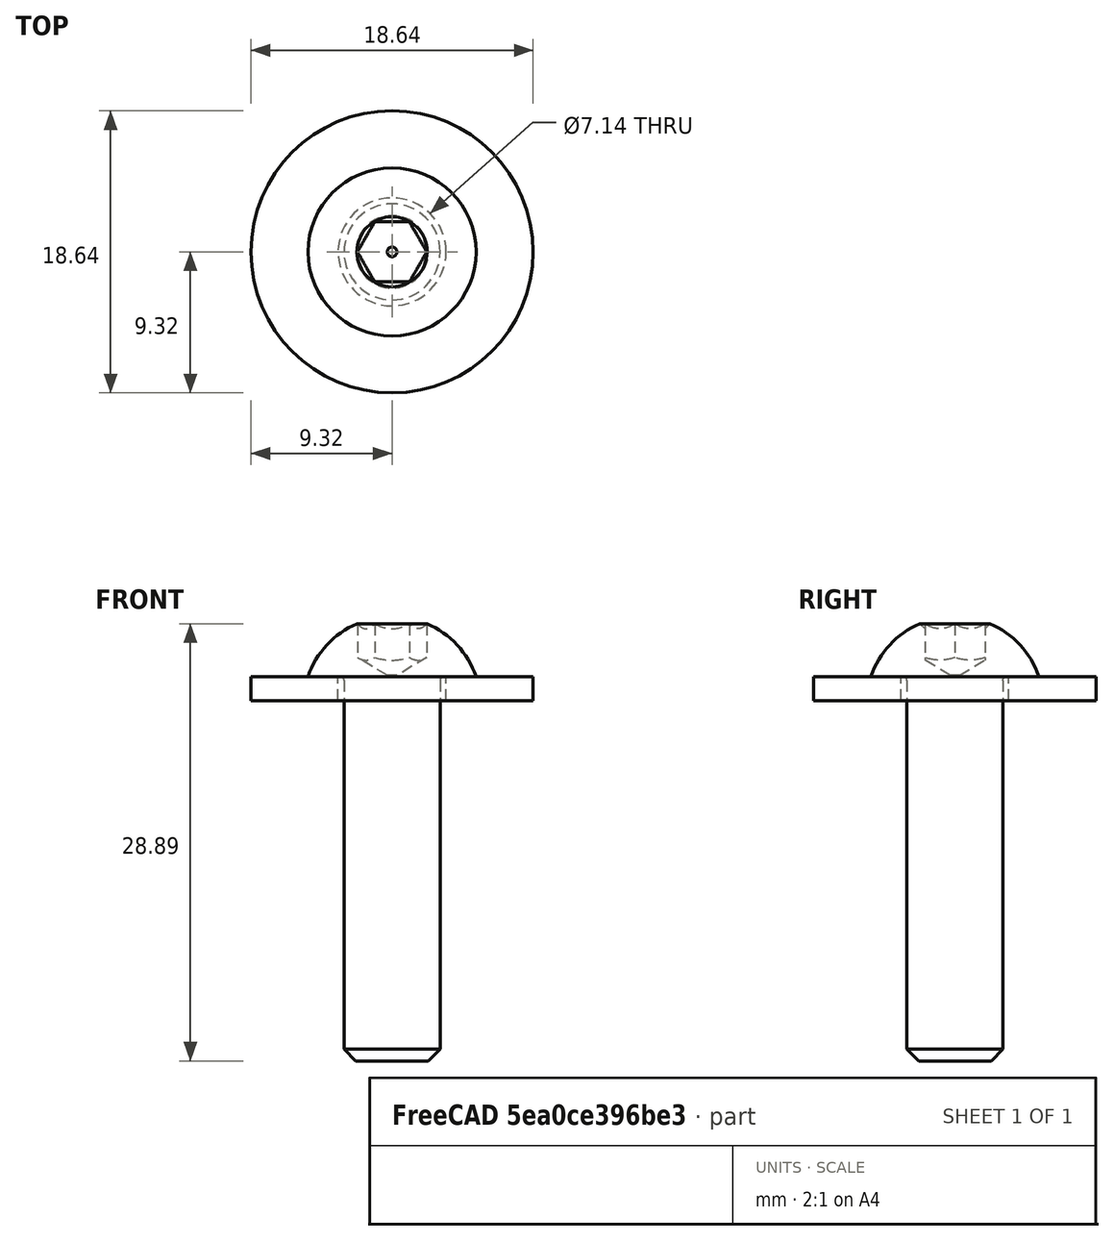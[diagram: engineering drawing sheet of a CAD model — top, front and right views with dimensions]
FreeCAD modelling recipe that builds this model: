
FCSTD DOCUMENT  (FreeCAD 2021.717R24301 +3842 (Git))
Label: Y-axis
License: Creative Commons Attribution
LicenseURL: http://creativecommons.org/licenses/by/4.0/
objects: App::FeaturePython×191, Part::FeaturePython×144, App::LinkElement×32, App::Link×30, App::DocumentObjectGroup×1
note: 139 computed .brp shape members not serialized (recipe doc carries the construction recipe); baked Part::Feature solids carry a one-line shape summary decoded from their .brp
EXTERNAL_REF file=parts/Extrusion.FCStd obj=Body003
EXTERNAL_REF file=parts/Extrusion.FCStd obj=Body005
EXTERNAL_REF file=parts/HGR20.FCStd obj=Assembly002
EXTERNAL_REF file=parts/Ballscrew.FCStd obj=Assembly004
EXTERNAL_REF file=parts/Y axis plates.FCStd obj=Assembly003
EXTERNAL_REF file=parts/Y axis plates.FCStd obj=Assembly002
EXTERNAL_REF file=parts/Y axis plates.FCStd obj=Assembly001
EXTERNAL_REF file=parts/Y axis plates.FCStd obj=Assembly
EXTERNAL_REF file=parts/NEMA23-76.FCStd obj=Assembly001
EXTERNAL_REF file=parts/NEMA23-76.FCStd obj=Assembly
EXTERNAL_REF file=parts/Y axis plates.FCStd obj=Assembly004
EXTERNAL_REF file=parts/Y axis plates.FCStd obj=Assembly005
EXTERNAL_REF file=parts/Table.FCStd obj=Assembly
EXTERNAL_REF file=parts/Y axis plates.FCStd obj=Assembly006
EXTERNAL_REF file=parts/Y axis plates.FCStd obj=Assembly007
EXTERNAL_REF file=parts/LimitSensor.FCStd obj=Assembly

FEATURE [App::Link] Link001  label="Link001(Cross member 2x2)"
  AutoLinkLabel = true
  AutoPlacement = true
  LinkPlacement = pos=(259,-5.77867e-05,-25) rot=(0,0,-1;1.5708rad)
  LinkedObject = -> <external parts/Extrusion.FCStd>#Body003
  Placement = pos=(259,-5.77867e-05,-25) rot=(0,0,-1;1.5708rad)
  SyncGroupVisibility = false
  _LinkVersion = 1
FEATURE [Part::FeaturePython] Parts002  # WARN: FeaturePython — macro-defined, semantics opaque (R4)
  Group = -> [Link001]
  GroupMode = 0
  _LinkVersion = 1
FEATURE [App::Link] Link003  label="Front"
  AutoLinkLabel = true
  AutoPlacement = true
  LinkPlacement = pos=(-9.60009,-389.6,-0.400015) rot=(0,0,1;0rad)
  LinkedObject = -> Assembly002
  Placement = pos=(-9.60009,-389.6,-0.400015) rot=(0,0,1;0rad)
  SyncGroupVisibility = false
  _LinkVersion = 1
FEATURE [App::Link] Link004  label="Cross1"
  AutoLinkLabel = true
  AutoPlacement = true
  LinkPlacement = pos=(-9.60009,-129.867,-0.400015) rot=(0,0,1;0rad)
  LinkedObject = -> Link003
  Placement = pos=(-9.60009,-129.867,-0.400015) rot=(0,0,1;0rad)
  SyncGroupVisibility = false
  _LinkVersion = 1
FEATURE [App::Link] Link005  label="Cross2"
  AutoLinkLabel = true
  AutoPlacement = true
  LinkPlacement = pos=(-9.60009,129.867,-0.400015) rot=(0,0,1;0rad)
  LinkedObject = -> Link003
  Placement = pos=(-9.60009,129.867,-0.400015) rot=(0,0,1;0rad)
  SyncGroupVisibility = false
  _LinkVersion = 1
FEATURE [App::Link] Link006  label="Back"
  AutoLinkLabel = true
  AutoPlacement = true
  LinkPlacement = pos=(-9.60009,389.6,-0.400015) rot=(0,0,1;0rad)
  LinkedObject = -> Link003
  Placement = pos=(-9.60009,389.6,-0.400015) rot=(0,0,1;0rad)
  SyncGroupVisibility = false
  _LinkVersion = 1
FEATURE [App::Link] Link  label="Link(Y-beam 2x4)"
  AutoLinkLabel = true
  AutoPlacement = true
  LinkedObject = -> <external parts/Extrusion.FCStd>#Body005
  SyncGroupVisibility = false
  _LinkVersion = 1
FEATURE [App::Link] Link008  label="Link008(Y-beam 2x4)"
  AutoLinkLabel = true
  AutoPlacement = true
  LinkPlacement = pos=(-9.58364e-05,49,0) rot=(0,0,1;3.14159rad)
  LinkedObject = -> <external parts/Extrusion.FCStd>#Body005
  Placement = pos=(-9.58364e-05,49,0) rot=(0,0,1;3.14159rad)
  SyncGroupVisibility = false
  _LinkVersion = 1
FEATURE [App::Link] Link009  label="Left beam"
  AutoLinkLabel = true
  AutoPlacement = true
  LinkedObject = -> Assembly001
  SyncGroupVisibility = false
  _LinkVersion = 1
FEATURE [App::Link] Link010  label="Right beam"
  AutoLinkLabel = true
  AutoPlacement = true
  LinkPlacement = pos=(498.8,-49,1.208e-13) rot=(0,0,1;6.28318rad)
  LinkedObject = -> Assembly003
  Placement = pos=(498.8,-49,1.208e-13) rot=(0,0,1;6.28318rad)
  SyncGroupVisibility = false
  _LinkVersion = 1
FEATURE [App::Link] Link011  label="HGR20 Left"
  AutoLinkLabel = true
  AutoPlacement = true
  LinkPlacement = pos=(-25.4,2.8e-15,38.1) rot=(-0.707107,0,0.707107;3.14159rad)
  LinkedObject = -> <external parts/HGR20.FCStd>#Assembly002
  Placement = pos=(-25.4,2.8e-15,38.1) rot=(-0.707107,0,0.707107;3.14159rad)
  SyncGroupVisibility = false
  _LinkVersion = 1
FEATURE [App::Link] Link012  label="HGR20 Right"
  AutoLinkLabel = true
  AutoPlacement = true
  LinkPlacement = pos=(524.2,-1.208e-13,38.1) rot=(0,-1,0;4.71239rad)
  LinkedObject = -> <external parts/HGR20.FCStd>#Assembly002
  Placement = pos=(524.2,-1.208e-13,38.1) rot=(0,-1,0;4.71239rad)
  SyncGroupVisibility = false
  _LinkVersion = 1
FEATURE [App::Link] Link013  label="Ballscrew Left"
  AutoLinkLabel = true
  AutoPlacement = true
  LinkPlacement = pos=(-30.1231,403.1,-15.0731) rot=(0,-1,0;1.5708rad)
  LinkedObject = -> <external parts/Ballscrew.FCStd>#Assembly004
  Placement = pos=(-30.1231,403.1,-15.0731) rot=(0,-1,0;1.5708rad)
  SyncGroupVisibility = false
  _LinkVersion = 1
FEATURE [App::Link] Link014  label="Ballscrew Right"
  AutoLinkLabel = true
  AutoPlacement = true
  LinkPlacement = pos=(528.923,403.1,-15.1269) rot=(0,1,0;1.5708rad)
  LinkedObject = -> <external parts/Ballscrew.FCStd>#Assembly004
  Placement = pos=(528.923,403.1,-15.1269) rot=(0,1,0;1.5708rad)
  SyncGroupVisibility = false
  _LinkVersion = 1
FEATURE [App::Link] Link015  label="BF12R plate"
  AutoLinkLabel = true
  AutoPlacement = true
  LinkPlacement = pos=(524.2,-445,-15.1) rot=(0,0,1;0rad)
  LinkedObject = -> <external parts/Y axis plates.FCStd>#Assembly003
  Placement = pos=(524.2,-445,-15.1) rot=(0,0,1;0rad)
  SyncGroupVisibility = false
  _LinkVersion = 1
FEATURE [App::Link] Link016  label="BF12L plate"
  AutoLinkLabel = true
  AutoPlacement = true
  LinkPlacement = pos=(-30.4,-445,-15.1) rot=(0,0,1;0rad)
  LinkedObject = -> <external parts/Y axis plates.FCStd>#Assembly002
  Placement = pos=(-30.4,-445,-15.1) rot=(0,0,1;0rad)
  SyncGroupVisibility = false
  _LinkVersion = 1
FEATURE [App::Link] Link017  label="BK12L plate"
  AutoLinkLabel = true
  AutoPlacement = true
  LinkPlacement = pos=(-30.4,347.1,-15.1) rot=(0,0,1;0rad)
  LinkedObject = -> <external parts/Y axis plates.FCStd>#Assembly001
  Placement = pos=(-30.4,347.1,-15.1) rot=(0,0,1;0rad)
  SyncGroupVisibility = false
  _LinkVersion = 1
FEATURE [App::Link] Link018  label="BK12R plate"
  AutoLinkLabel = true
  AutoPlacement = true
  LinkPlacement = pos=(524.2,347.1,-15.1) rot=(0,0,1;0rad)
  LinkedObject = -> <external parts/Y axis plates.FCStd>#Assembly
  Placement = pos=(524.2,347.1,-15.1) rot=(0,0,1;0rad)
  SyncGroupVisibility = false
  _LinkVersion = 1
FEATURE [App::Link] Link019  label="Coupling-L"
  AutoLinkLabel = true
  AutoPlacement = true
  LinkPlacement = pos=(-55.4,393.45,-15.1) rot=(0.57735,-0.57735,0.57735;2.0944rad)
  LinkedObject = -> <external parts/NEMA23-76.FCStd>#Assembly001
  Placement = pos=(-55.4,393.45,-15.1) rot=(0.57735,-0.57735,0.57735;2.0944rad)
  SyncGroupVisibility = false
  _LinkVersion = 1
FEATURE [App::Link] Link020  label="Coupling-R"
  AutoLinkLabel = true
  AutoPlacement = true
  LinkPlacement = pos=(554.2,393.45,-15.1) rot=(0.57735,0.57735,-0.57735;2.0944rad)
  LinkedObject = -> <external parts/NEMA23-76.FCStd>#Assembly001
  Placement = pos=(554.2,393.45,-15.1) rot=(0.57735,0.57735,-0.57735;2.0944rad)
  SyncGroupVisibility = false
  _LinkVersion = 1
FEATURE [App::Link] Link021  label="NEMA23-L"
  AutoLinkLabel = true
  AutoPlacement = true
  LinkPlacement = pos=(-55.4,421.35,-15.1) rot=(-0.57735,-0.57735,-0.57735;2.0944rad)
  LinkedObject = -> <external parts/NEMA23-76.FCStd>#Assembly
  Placement = pos=(-55.4,421.35,-15.1) rot=(-0.57735,-0.57735,-0.57735;2.0944rad)
  SyncGroupVisibility = false
  _LinkVersion = 1
FEATURE [App::Link] Link022  label="NEMA23-R"
  AutoLinkLabel = true
  AutoPlacement = true
  LinkPlacement = pos=(554.2,421.35,-15.1) rot=(0.57735,-0.57735,-0.57735;4.18879rad)
  LinkedObject = -> <external parts/NEMA23-76.FCStd>#Assembly
  Placement = pos=(554.2,421.35,-15.1) rot=(0.57735,-0.57735,-0.57735;4.18879rad)
  SyncGroupVisibility = false
  _LinkVersion = 1
FEATURE [App::Link] Link023  label="Motor plate R"
  AutoLinkLabel = true
  AutoPlacement = true
  LinkPlacement = pos=(530.9,415,-2.167e-13) rot=(0,0,-1;3.14159rad)
  LinkedObject = -> <external parts/Y axis plates.FCStd>#Assembly004
  Placement = pos=(530.9,415,-2.167e-13) rot=(0,0,-1;3.14159rad)
  SyncGroupVisibility = false
  _LinkVersion = 1
FEATURE [App::Link] Link024  label="Motor plate L"
  AutoLinkLabel = true
  AutoPlacement = true
  LinkPlacement = pos=(-32.1,414.35,1.5117e-12) rot=(0,0,1;3.14159rad)
  LinkedObject = -> <external parts/Y axis plates.FCStd>#Assembly005
  Placement = pos=(-32.1,414.35,1.5117e-12) rot=(0,0,1;3.14159rad)
  SyncGroupVisibility = false
  _LinkVersion = 1
FEATURE [App::Link] Link025  label="PP Table"
  AutoLinkLabel = true
  AutoPlacement = true
  LinkPlacement = pos=(249.4,-1.137e-13,-2.013e-13) rot=(0,0,1;0rad)
  LinkedObject = -> <external parts/Table.FCStd>#Assembly
  Placement = pos=(249.4,-1.137e-13,-2.013e-13) rot=(0,0,1;0rad)
  SyncGroupVisibility = false
  _LinkVersion = 1
FEATURE [Part::FeaturePython] Screw  label="1/4inx1in-Screw"  # Fasteners workbench fastener (typed FeaturePython)
  diameter = 11
  invert = false
  length = 6
  lengthCustom = 25.4
  matchOuter = false
  offset = 0
  thread = false
  type = 4
FEATURE [Part::FeaturePython] Washer  label="1/4in-Washer"  # Fasteners workbench fastener (typed FeaturePython)
  Placement = pos=(0,0,-1.6002) rot=(0,0,1;0rad)
  diameter = 11
  invert = false
  matchOuter = false
  offset = 0
  type = 1
FEATURE [Part::FeaturePython] Parts004  # WARN: FeaturePython — macro-defined, semantics opaque (R4)
  Group = -> [Washer,Screw]
  GroupMode = 0
  _LinkVersion = 1
FEATURE [App::LinkElement] Link026_i0
  LinkPlacement = pos=(21.5898,-402.3,-12.7) rot=(0,-1,0;1.5708rad)
  LinkedObject = -> Assembly004
  Placement = pos=(21.5898,-402.3,-12.7) rot=(0,-1,0;1.5708rad)
  _LinkVersion = 1
FEATURE [App::LinkElement] Link026_i1
  LinkPlacement = pos=(21.5898,-376.9,-12.7) rot=(0,-1,0;1.5708rad)
  LinkedObject = -> Assembly004
  Placement = pos=(21.5898,-376.9,-12.7) rot=(0,-1,0;1.5708rad)
  _LinkVersion = 1
FEATURE [App::LinkElement] Link026_i2
  LinkPlacement = pos=(21.5898,-402.3,-38.1) rot=(0,-1,0;1.5708rad)
  LinkedObject = -> Assembly004
  Placement = pos=(21.5898,-402.3,-38.1) rot=(0,-1,0;1.5708rad)
  _LinkVersion = 1
FEATURE [App::LinkElement] Link026_i3
  LinkPlacement = pos=(21.5898,-376.9,-38.1) rot=(0,-1,0;1.5708rad)
  LinkedObject = -> Assembly004
  Placement = pos=(21.5898,-376.9,-38.1) rot=(0,-1,0;1.5708rad)
  _LinkVersion = 1
FEATURE [App::LinkElement] Link026_i4
  LinkPlacement = pos=(21.5898,-142.567,-12.7) rot=(0,-1,0;1.5708rad)
  LinkedObject = -> Assembly004
  Placement = pos=(21.5898,-142.567,-12.7) rot=(0,-1,0;1.5708rad)
  _LinkVersion = 1
FEATURE [App::LinkElement] Link026_i5
  LinkPlacement = pos=(21.5898,-117.167,-12.7) rot=(0,-1,0;1.5708rad)
  LinkedObject = -> Assembly004
  Placement = pos=(21.5898,-117.167,-12.7) rot=(0,-1,0;1.5708rad)
  _LinkVersion = 1
FEATURE [App::LinkElement] Link026_i6
  LinkPlacement = pos=(21.5898,-142.567,-38.1) rot=(0,-1,0;1.5708rad)
  LinkedObject = -> Assembly004
  Placement = pos=(21.5898,-142.567,-38.1) rot=(0,-1,0;1.5708rad)
  _LinkVersion = 1
FEATURE [App::LinkElement] Link026_i7
  LinkPlacement = pos=(21.5898,-117.167,-38.1) rot=(0,-1,0;1.5708rad)
  LinkedObject = -> Assembly004
  Placement = pos=(21.5898,-117.167,-38.1) rot=(0,-1,0;1.5708rad)
  _LinkVersion = 1
FEATURE [App::LinkElement] Link026_i8
  LinkPlacement = pos=(21.5898,142.567,-12.7) rot=(0,-1,0;1.5708rad)
  LinkedObject = -> Assembly004
  Placement = pos=(21.5898,142.567,-12.7) rot=(0,-1,0;1.5708rad)
  _LinkVersion = 1
FEATURE [App::LinkElement] Link026_i9
  LinkPlacement = pos=(21.5898,117.167,-12.7) rot=(0,-1,0;1.5708rad)
  LinkedObject = -> Assembly004
  Placement = pos=(21.5898,117.167,-12.7) rot=(0,-1,0;1.5708rad)
  _LinkVersion = 1
FEATURE [App::LinkElement] Link026_i10
  LinkPlacement = pos=(21.5898,117.167,-38.1) rot=(0,-1,0;1.5708rad)
  LinkedObject = -> Assembly004
  Placement = pos=(21.5898,117.167,-38.1) rot=(0,-1,0;1.5708rad)
  _LinkVersion = 1
FEATURE [App::LinkElement] Link026_i11
  LinkPlacement = pos=(21.5898,142.567,-38.1) rot=(0,-1,0;1.5708rad)
  LinkedObject = -> Assembly004
  Placement = pos=(21.5898,142.567,-38.1) rot=(0,-1,0;1.5708rad)
  _LinkVersion = 1
FEATURE [App::LinkElement] Link026_i12
  LinkPlacement = pos=(21.5898,376.9,-12.7) rot=(0,-1,0;1.5708rad)
  LinkedObject = -> Assembly004
  Placement = pos=(21.5898,376.9,-12.7) rot=(0,-1,0;1.5708rad)
  _LinkVersion = 1
FEATURE [App::LinkElement] Link026_i13
  LinkPlacement = pos=(21.5898,402.3,-12.7) rot=(0,-1,0;1.5708rad)
  LinkedObject = -> Assembly004
  Placement = pos=(21.5898,402.3,-12.7) rot=(0,-1,0;1.5708rad)
  _LinkVersion = 1
FEATURE [App::LinkElement] Link026_i14
  LinkPlacement = pos=(21.5898,376.9,-38.1) rot=(0,-1,0;1.5708rad)
  LinkedObject = -> Assembly004
  Placement = pos=(21.5898,376.9,-38.1) rot=(0,-1,0;1.5708rad)
  _LinkVersion = 1
FEATURE [App::LinkElement] Link026_i15
  LinkPlacement = pos=(21.5898,402.3,-38.1) rot=(0,-1,0;1.5708rad)
  LinkedObject = -> Assembly004
  Placement = pos=(21.5898,402.3,-38.1) rot=(0,-1,0;1.5708rad)
  _LinkVersion = 1
FEATURE [App::Link] Link026  label="1/4x1 screw and washer 16ct"
  AutoLinkLabel = true
  AutoPlacement = true
  ElementCount = 16
  ElementList = -> [Link026_i0,Link026_i1,Link026_i2,Link026_i3,Link026_i4,Link026_i5,Link026_i6,Link026_i7,Link026_i8,Link026_i9,Link026_i10,Link026_i11,Link026_i12,Link026_i13,Link026_i14,Link026_i15]
  LinkedObject = -> Assembly004
  SyncGroupVisibility = false
  _LinkVersion = 1
FEATURE [Part::FeaturePython] Parts001  # WARN: FeaturePython — macro-defined, semantics opaque (R4)
  Group = -> [Link,Link026]
  GroupMode = 0
  _LinkVersion = 1
FEATURE [App::LinkElement] Link027_i0
  LinkPlacement = pos=(200.7,-55.4102,-38.1) rot=(0.57735,-0.57735,0.57735;2.0944rad)
  LinkedObject = -> Assembly004
  Placement = pos=(200.7,-55.4102,-38.1) rot=(0.57735,-0.57735,0.57735;2.0944rad)
  _LinkVersion = 1
FEATURE [App::LinkElement] Link027_i1
  LinkPlacement = pos=(226.1,-55.4103,-38.1) rot=(0.57735,-0.57735,0.57735;2.0944rad)
  LinkedObject = -> Assembly004
  Placement = pos=(226.1,-55.4103,-38.1) rot=(0.57735,-0.57735,0.57735;2.0944rad)
  _LinkVersion = 1
FEATURE [App::LinkElement] Link027_i2
  LinkPlacement = pos=(200.7,-55.4102,-12.7) rot=(0.57735,-0.57735,0.57735;2.0944rad)
  LinkedObject = -> Assembly004
  Placement = pos=(200.7,-55.4102,-12.7) rot=(0.57735,-0.57735,0.57735;2.0944rad)
  _LinkVersion = 1
FEATURE [App::LinkElement] Link027_i3
  LinkPlacement = pos=(226.1,-55.4103,-12.7) rot=(0.57735,-0.57735,0.57735;2.0944rad)
  LinkedObject = -> Assembly004
  Placement = pos=(226.1,-55.4103,-12.7) rot=(0.57735,-0.57735,0.57735;2.0944rad)
  _LinkVersion = 1
FEATURE [App::LinkElement] Link027_i4
  LinkPlacement = pos=(460.433,-55.4103,-38.1) rot=(0.57735,-0.57735,0.57735;2.0944rad)
  LinkedObject = -> Assembly004
  Placement = pos=(460.433,-55.4103,-38.1) rot=(0.57735,-0.57735,0.57735;2.0944rad)
  _LinkVersion = 1
FEATURE [App::LinkElement] Link027_i5
  LinkPlacement = pos=(485.833,-55.4103,-38.1) rot=(0.57735,-0.57735,0.57735;2.0944rad)
  LinkedObject = -> Assembly004
  Placement = pos=(485.833,-55.4103,-38.1) rot=(0.57735,-0.57735,0.57735;2.0944rad)
  _LinkVersion = 1
FEATURE [App::LinkElement] Link027_i6
  LinkPlacement = pos=(460.433,-55.4103,-12.7) rot=(0.57735,-0.57735,0.57735;2.0944rad)
  LinkedObject = -> Assembly004
  Placement = pos=(460.433,-55.4103,-12.7) rot=(0.57735,-0.57735,0.57735;2.0944rad)
  _LinkVersion = 1
FEATURE [App::LinkElement] Link027_i7
  LinkPlacement = pos=(485.833,-55.4103,-12.7) rot=(0.57735,-0.57735,0.57735;2.0944rad)
  LinkedObject = -> Assembly004
  Placement = pos=(485.833,-55.4103,-12.7) rot=(0.57735,-0.57735,0.57735;2.0944rad)
  _LinkVersion = 1
FEATURE [App::LinkElement] Link027_i8
  LinkPlacement = pos=(720.166,-55.4103,-38.1) rot=(0.57735,-0.57735,0.57735;2.0944rad)
  LinkedObject = -> Assembly004
  Placement = pos=(720.166,-55.4103,-38.1) rot=(0.57735,-0.57735,0.57735;2.0944rad)
  _LinkVersion = 1
FEATURE [App::LinkElement] Link027_i9
  LinkPlacement = pos=(745.566,-55.4103,-38.1) rot=(0.57735,-0.57735,0.57735;2.0944rad)
  LinkedObject = -> Assembly004
  Placement = pos=(745.566,-55.4103,-38.1) rot=(0.57735,-0.57735,0.57735;2.0944rad)
  _LinkVersion = 1
FEATURE [App::LinkElement] Link027_i10
  LinkPlacement = pos=(720.166,-55.4103,-12.7) rot=(0.57735,-0.57735,0.57735;2.0944rad)
  LinkedObject = -> Assembly004
  Placement = pos=(720.166,-55.4103,-12.7) rot=(0.57735,-0.57735,0.57735;2.0944rad)
  _LinkVersion = 1
FEATURE [App::LinkElement] Link027_i11
  LinkPlacement = pos=(745.566,-55.4103,-12.7) rot=(0.57735,-0.57735,0.57735;2.0944rad)
  LinkedObject = -> Assembly004
  Placement = pos=(745.566,-55.4103,-12.7) rot=(0.57735,-0.57735,0.57735;2.0944rad)
  _LinkVersion = 1
FEATURE [App::LinkElement] Link027_i12
  LinkPlacement = pos=(979.9,-55.4103,-38.1) rot=(0.57735,-0.57735,0.57735;2.0944rad)
  LinkedObject = -> Assembly004
  Placement = pos=(979.9,-55.4103,-38.1) rot=(0.57735,-0.57735,0.57735;2.0944rad)
  _LinkVersion = 1
FEATURE [App::LinkElement] Link027_i13
  LinkPlacement = pos=(1005.3,-55.4103,-38.1) rot=(0.57735,-0.57735,0.57735;2.0944rad)
  LinkedObject = -> Assembly004
  Placement = pos=(1005.3,-55.4103,-38.1) rot=(0.57735,-0.57735,0.57735;2.0944rad)
  _LinkVersion = 1
FEATURE [App::LinkElement] Link027_i14
  LinkPlacement = pos=(979.9,-55.4103,-12.7) rot=(0.57735,-0.57735,0.57735;2.0944rad)
  LinkedObject = -> Assembly004
  Placement = pos=(979.9,-55.4103,-12.7) rot=(0.57735,-0.57735,0.57735;2.0944rad)
  _LinkVersion = 1
FEATURE [App::LinkElement] Link027_i15
  LinkPlacement = pos=(1005.3,-55.4103,-12.7) rot=(0.57735,-0.57735,0.57735;2.0944rad)
  LinkedObject = -> Assembly004
  Placement = pos=(1005.3,-55.4103,-12.7) rot=(0.57735,-0.57735,0.57735;2.0944rad)
  _LinkVersion = 1
FEATURE [App::Link] Link027  label="1/4x1 screw and washer 16ct "
  AutoLinkLabel = true
  AutoPlacement = true
  ElementCount = 16
  ElementList = -> [Link027_i0,Link027_i1,Link027_i2,Link027_i3,Link027_i4,Link027_i5,Link027_i6,Link027_i7,Link027_i8,Link027_i9,Link027_i10,Link027_i11,Link027_i12,Link027_i13,Link027_i14,Link027_i15]
  LinkPlacement = pos=(-77.0001,-554,0) rot=(0,0,1;1.5708rad)
  LinkedObject = -> Assembly004
  Placement = pos=(-77.0001,-554,0) rot=(0,0,1;1.5708rad)
  SyncGroupVisibility = false
  _LinkVersion = 1
FEATURE [Part::FeaturePython] Parts003  # WARN: FeaturePython — macro-defined, semantics opaque (R4)
  Group = -> [Link008,Link027]
  GroupMode = 0
  _LinkVersion = 1
FEATURE [App::Link] Link028  label="Front plate L"
  AutoLinkLabel = true
  AutoPlacement = true
  LinkPlacement = pos=(-32.1,-415,3.855e-13) rot=(0,0,1;0rad)
  LinkedObject = -> <external parts/Y axis plates.FCStd>#Assembly006
  Placement = pos=(-32.1,-415,3.855e-13) rot=(0,0,1;0rad)
  SyncGroupVisibility = false
  _LinkVersion = 1
FEATURE [App::Link] Link029  label="Front plate R"
  AutoLinkLabel = true
  AutoPlacement = true
  LinkPlacement = pos=(530.9,-421.35,-4.388e-13) rot=(0,0,-1;3.14159rad)
  LinkedObject = -> <external parts/Y axis plates.FCStd>#Assembly007
  Placement = pos=(530.9,-421.35,-4.388e-13) rot=(0,0,-1;3.14159rad)
  SyncGroupVisibility = false
  _LinkVersion = 1
FEATURE [App::Link] Link030  label="Limit sensor R"
  AutoLinkLabel = true
  AutoPlacement = true
  LinkPlacement = pos=(555.9,415,38.1) rot=(0,-1,0;1.5708rad)
  LinkedObject = -> <external parts/LimitSensor.FCStd>#Assembly
  Placement = pos=(555.9,415,38.1) rot=(0,-1,0;1.5708rad)
  SyncGroupVisibility = false
  _LinkVersion = 1
FEATURE [App::Link] Link031  label="Limit sensor L"
  AutoLinkLabel = true
  AutoPlacement = true
  LinkPlacement = pos=(-57.1,415,38.1) rot=(0,1,0;1.5708rad)
  LinkedObject = -> <external parts/LimitSensor.FCStd>#Assembly
  Placement = pos=(-57.1,415,38.1) rot=(0,1,0;1.5708rad)
  SyncGroupVisibility = false
  _LinkVersion = 1
FEATURE [Part::FeaturePython] Parts  # WARN: FeaturePython — macro-defined, semantics opaque (R4)
  Group = -> [Link003,Link004,Link005,Link006,Link009,Link010,Link011,Link012,Link013,Link014,Link016,Link015,Link017,Link018,Link019,Link020,Link021,Link022,Link024,Link023,Link025,Link028,Link029,Link030,Link031]
  GroupMode = 0
  _LinkVersion = 1
FEATURE [Part::FeaturePython] Assembly  label="Base Assembly"  # WARN: FeaturePython — macro-defined, semantics opaque (R4)
  AutoRelax = true
  BuildShape = 0
  Freeze = false
  Group = -> [Constraints,Elements,Parts]
  Verbose = false
  _LinkVersion = 1
  _SolverType = 1
  _Version = 1
FEATURE [App::FeaturePython] Constraints  # WARN: FeaturePython — macro-defined, semantics opaque (R4)
  Group = -> [Constraint002,Constraint003,Constraint004,Constraint005,Constraint006,Constraint007,Constraint009,Constraint010,Constraint011,Constraint012,Constraint013,Constraint014,Constraint015,Constraint016,Constraint017,Constraint018,Constraint019,Constraint020,Constraint021,Constraint022,Constraint023,Constraint058,Constraint059,Constraint060,Constraint061]
  _LinkVersion = 1
  _Version = 1
FEATURE [App::FeaturePython] Elements  # WARN: FeaturePython — macro-defined, semantics opaque (R4)
  Group = -> [Element010,Element011,Element012,Element013,Element018,Element020,Element021,Element022,Element023,Element024,Element025,Element026,Element029,Element030,Element031,Element032,Element033,Element036,Element037,Element038,Element039,Element040,Element041,Element042,Element043,Element044,Element045,Element046,Element047,Element048,Element049,Element050,Element051,Element052,Element053,Element054,+15 more]
  _LinkVersion = 1
FEATURE [Part::FeaturePython] Assembly001  label="Left beam Assembly"  # WARN: FeaturePython — macro-defined, semantics opaque (R4)
  AutoRelax = true
  BuildShape = 0
  Freeze = false
  Group = -> [Constraints001,Elements001,Parts001]
  Verbose = false
  _LinkVersion = 1
  _SolverType = 1
  _Version = 1
FEATURE [App::FeaturePython] Constraints001  # WARN: FeaturePython — macro-defined, semantics opaque (R4)
  Group = -> [Constraint001,Constraint026,Constraint027,Constraint028,Constraint029,Constraint030,Constraint031,Constraint032,Constraint033,Constraint034,Constraint035,Constraint036,Constraint037,Constraint038,Constraint039,Constraint040,Constraint041]
  _LinkVersion = 1
  _Version = 1
FEATURE [App::FeaturePython] Elements001  # WARN: FeaturePython — macro-defined, semantics opaque (R4)
  Group = -> [Element,Element001,Element002,Element003,Element027,Element035,_Element002,_Element003,_Element004,_Element005,_Element006,_Element007,_Element008,_Element009,_Element010,_Element011,_Element012,_Element013,_Element014,_Element015,_Element016,_Element017,_Element018,_Element019,_Element020,_Element021,_Element022,_Element023,_Element024,_Element025,_Element026,_Element027,_Element028,_Element029,+5 more]
  _LinkVersion = 1
FEATURE [Part::FeaturePython] Element  label="1"  # link proxy (typed FeaturePython)
  Detach = false
  LinkTransform = true
  LinkedObject = -> Link [Pocket005.Sketch009.Edge13]
  _LinkVersion = 1
  _Parent = -> Elements001
FEATURE [Part::FeaturePython] Element001  label="2"  # link proxy (typed FeaturePython)
  Detach = false
  LinkTransform = true
  LinkedObject = -> Link [Pocket005.Sketch009.Edge12]
  _LinkVersion = 1
  _Parent = -> Elements001
FEATURE [Part::FeaturePython] Element002  label="3"  # link proxy (typed FeaturePython)
  Detach = false
  LinkTransform = true
  LinkedObject = -> Link [Pocket005.Sketch009.Edge6]
  _LinkVersion = 1
  _Parent = -> Elements001
FEATURE [Part::FeaturePython] Element003  label="4"  # link proxy (typed FeaturePython)
  Detach = false
  LinkTransform = true
  LinkedObject = -> Link [Pocket005.Sketch009.Edge2]
  _LinkVersion = 1
  _Parent = -> Elements001
FEATURE [Part::FeaturePython] Assembly002  label="Cross beam Assembly"  # WARN: FeaturePython — macro-defined, semantics opaque (R4)
  AutoRelax = true
  BuildShape = 0
  Freeze = false
  Group = -> [Constraints002,Elements002,Parts002]
  Verbose = false
  _LinkVersion = 1
  _SolverType = 1
  _Version = 1
FEATURE [App::FeaturePython] Constraints002  # WARN: FeaturePython — macro-defined, semantics opaque (R4)
  Group = -> [Constraint]
  _LinkVersion = 1
  _Version = 1
FEATURE [App::FeaturePython] Elements002  # WARN: FeaturePython — macro-defined, semantics opaque (R4)
  Group = -> [Element004,Element005,Element063]
  _LinkVersion = 1
FEATURE [Part::FeaturePython] Element004  label="right"  # link proxy (typed FeaturePython)
  Detach = false
  LinkTransform = true
  LinkedObject = -> Link001 [Pad003.Edge512]
  _LinkVersion = 1
  _Parent = -> Elements002
FEATURE [Part::FeaturePython] Element005  label="left"  # link proxy (typed FeaturePython)
  Detach = false
  LinkTransform = true
  LinkedObject = -> Link001 [Pad003.Edge513]
  _LinkVersion = 1
  _Parent = -> Elements002
FEATURE [App::FeaturePython] Constraint  label="Locked"  # WARN: FeaturePython — macro-defined, semantics opaque (R4)
  Disabled = false
  Group = -> [ElementLink]
  _ConstraintType = 0
  _LinkVersion = 1
  _Parent = -> Constraints002
FEATURE [App::FeaturePython] ElementLink  label="left"  # link proxy (typed FeaturePython)
  LinkTransform = true
  LinkedObject = -> Element005
  _LinkVersion = 1
  _Parent = -> Constraint
FEATURE [App::FeaturePython] Constraint001  label="Locked001"  # WARN: FeaturePython — macro-defined, semantics opaque (R4)
  Disabled = false
  Group = -> [ElementLink001]
  _ConstraintType = 0
  _LinkVersion = 1
  _Parent = -> Constraints001
FEATURE [App::FeaturePython] ElementLink001  label="1"  # link proxy (typed FeaturePython)
  LinkTransform = true
  LinkedObject = -> Element
  _LinkVersion = 1
  _Parent = -> Constraint001
FEATURE [Part::FeaturePython] Element010  label="F-L@Cross beam Assembly"  # link proxy (typed FeaturePython)
  Detach = false
  LinkTransform = true
  LinkedObject = -> Link003 [1.$left.]
  _LinkVersion = 1
  _Parent = -> Elements
FEATURE [App::FeaturePython] Constraint002  label="Locked002"  # WARN: FeaturePython — macro-defined, semantics opaque (R4)
  Disabled = false
  Group = -> [ElementLink002]
  _ConstraintType = 0
  _LinkVersion = 1
  _Parent = -> Constraints
FEATURE [App::FeaturePython] ElementLink002  label="1@Left beam Assembly"  # link proxy (typed FeaturePython)
  LinkTransform = true
  LinkedObject = -> Element020
  _LinkVersion = 1
  _Parent = -> Constraint002
FEATURE [App::FeaturePython] Constraint003  label="Attachment-F-L"  # WARN: FeaturePython — macro-defined, semantics opaque (R4)
  Cascade = false
  Disabled = false
  Group = -> [ElementLink003,ElementLink004]
  Multiply = false
  _ConstraintType = 45
  _LinkVersion = 1
  _Parent = -> Constraints
FEATURE [App::FeaturePython] ElementLink003  label="1@Left beam Assembly"  # link proxy (typed FeaturePython)
  LinkTransform = true
  LinkedObject = -> Element020
  Offset = pos=(0,0,0) rot=(1,0,0;3.14159rad)
  Placement = pos=(46.38,-804.6,-1.688e-13) rot=(0,0,1;3.14159rad)
  _LinkVersion = 1
  _Parent = -> Constraint003
FEATURE [App::FeaturePython] ElementLink004  label="F-L@Cross beam Assembly"  # link proxy (typed FeaturePython)
  LinkTransform = true
  LinkedObject = -> Element010
  Offset = pos=(0,0,2.21) rot=(0,0,1;1.5708rad)
  Placement = pos=(-2.21,-389.6,-415) rot=(-1,0,0;1.5708rad)
  _LinkVersion = 1
  _Parent = -> Constraint003
FEATURE [App::DocumentObjectGroup] Group001  label="Sub Assemblies"
  ExportMode = 1
  Group = -> [Assembly001,Assembly002,Assembly003,Assembly004]
  _GroupVersion = 1
FEATURE [Part::FeaturePython] Element011  label="C1-L@Cross beam Assembly"  # link proxy (typed FeaturePython)
  Detach = false
  LinkTransform = true
  LinkedObject = -> Link004 [1.$left.]
  _LinkVersion = 1
  _Parent = -> Elements
FEATURE [Part::FeaturePython] Element012  label="C2-L@Cross beam Assembly"  # link proxy (typed FeaturePython)
  Detach = false
  LinkTransform = true
  LinkedObject = -> Link005 [1.$left.]
  _LinkVersion = 1
  _Parent = -> Elements
FEATURE [Part::FeaturePython] Element013  label="B-L@Cross beam Assembly"  # link proxy (typed FeaturePython)
  Detach = false
  LinkTransform = true
  LinkedObject = -> Link006 [1.$left.]
  _LinkVersion = 1
  _Parent = -> Elements
FEATURE [App::FeaturePython] Constraint004  label="Attachment-C1-L"  # WARN: FeaturePython — macro-defined, semantics opaque (R4)
  Cascade = false
  Disabled = false
  Group = -> [ElementLink005,ElementLink006]
  Multiply = false
  _ConstraintType = 45
  _LinkVersion = 1
  _Parent = -> Constraints
FEATURE [App::FeaturePython] ElementLink005  label="2@Left beam Assembly"  # link proxy (typed FeaturePython)
  LinkTransform = true
  LinkedObject = -> Element021
  Offset = pos=(0,0,0) rot=(0,0,1;1.5708rad)
  Placement = pos=(0,-155.267,129.867) rot=(1,0,0;1.5708rad)
  _LinkVersion = 1
  _Parent = -> Constraint004
FEATURE [App::FeaturePython] ElementLink006  label="C1-L@Cross beam Assembly"  # link proxy (typed FeaturePython)
  LinkTransform = true
  LinkedObject = -> Element011
  Offset = pos=(0,0,2.21) rot=(1,0,0;3.14159rad)
  Placement = pos=(48.59,0,-25.4) rot=(0,1,0;3.14159rad)
  _LinkVersion = 1
  _Parent = -> Constraint004
FEATURE [App::FeaturePython] Constraint005  label="Attachment-C2-L"  # WARN: FeaturePython — macro-defined, semantics opaque (R4)
  Cascade = false
  Disabled = false
  Group = -> [ElementLink007,ElementLink008]
  Multiply = false
  _ConstraintType = 45
  _LinkVersion = 1
  _Parent = -> Constraints
FEATURE [App::FeaturePython] ElementLink007  label="C2-L@Cross beam Assembly"  # link proxy (typed FeaturePython)
  LinkTransform = true
  LinkedObject = -> Element012
  Offset = pos=(0,0,0) rot=(0,0,1;1.5708rad)
  Placement = pos=(5.68e-14,129.867,104.467) rot=(-1,0,0;1.5708rad)
  _LinkVersion = 1
  _Parent = -> Constraint005
FEATURE [App::FeaturePython] ElementLink008  label="3@Left beam Assembly"  # link proxy (typed FeaturePython)
  LinkTransform = true
  LinkedObject = -> Element022
  Offset = pos=(0,0,2.21) rot=(1,0,0;3.14159rad)
  Placement = pos=(48.59,234.333,6.22e-14) rot=(0,0,1;3.14159rad)
  _LinkVersion = 1
  _Parent = -> Constraint005
FEATURE [App::FeaturePython] Constraint006  label="Attachment-B-L"  # WARN: FeaturePython — macro-defined, semantics opaque (R4)
  Cascade = false
  Disabled = false
  Group = -> [ElementLink009,ElementLink010]
  Multiply = false
  _ConstraintType = 45
  _LinkVersion = 1
  _Parent = -> Constraints
FEATURE [App::FeaturePython] ElementLink009  label="B-L@Cross beam Assembly"  # link proxy (typed FeaturePython)
  LinkTransform = true
  LinkedObject = -> Element013
  Offset = pos=(0,0,0) rot=(0,0,1;1.5708rad)
  Placement = pos=(5.68e-14,389.6,364.2) rot=(-1,0,0;1.5708rad)
  _LinkVersion = 1
  _Parent = -> Constraint006
FEATURE [App::FeaturePython] ElementLink010  label="4@Left beam Assembly"  # link proxy (typed FeaturePython)
  LinkTransform = true
  LinkedObject = -> Element023
  Offset = pos=(0,0,2.21) rot=(1,0,0;3.14159rad)
  Placement = pos=(48.59,753.8,1.776e-13) rot=(0,0,1;3.14159rad)
  _LinkVersion = 1
  _Parent = -> Constraint006
FEATURE [Part::FeaturePython] Element018  label="F-R@Cross beam Assembly"  # link proxy (typed FeaturePython)
  Detach = false
  LinkTransform = true
  LinkedObject = -> Link003 [1.$right.]
  _LinkVersion = 1
  _Parent = -> Elements
FEATURE [App::FeaturePython] Constraint007  label="Attachment-F-R"  # WARN: FeaturePython — macro-defined, semantics opaque (R4)
  Cascade = false
  Disabled = false
  Group = -> [ElementLink011,ElementLink012]
  Multiply = false
  _ConstraintType = 45
  _LinkVersion = 1
  _Parent = -> Constraints
FEATURE [App::FeaturePython] ElementLink011  label="F-R@Cross beam Assembly"  # link proxy (typed FeaturePython)
  LinkTransform = true
  LinkedObject = -> Element018
  Offset = pos=(0,0,-2.21) rot=(0,0,1;0rad)
  Placement = pos=(2.21,-5.68e-14,1.8e-15) rot=(0,0,1;0rad)
  _LinkVersion = 1
  _Parent = -> Constraint007
FEATURE [App::FeaturePython] ElementLink012  label="1@Right beam Assembly"  # link proxy (typed FeaturePython)
  LinkTransform = true
  LinkedObject = -> Element024
  Offset = pos=(0,0,0) rot=(0,0,1;4.71239rad)
  Placement = pos=(1.29857e-06,-415,389.6) rot=(1,0,0;1.5708rad)
  _LinkVersion = 1
  _Parent = -> Constraint007
FEATURE [Part::FeaturePython] Assembly003  label="Right beam Assembly"  # WARN: FeaturePython — macro-defined, semantics opaque (R4)
  AutoRelax = true
  BuildShape = 0
  Freeze = false
  Group = -> [Constraints003,Elements003,Parts003]
  Placement = pos=(423,-5.04255e-05,0) rot=(0,0,1;0rad)
  Verbose = false
  _LinkVersion = 1
  _SolverType = 1
  _Version = 1
FEATURE [App::FeaturePython] Constraints003  # WARN: FeaturePython — macro-defined, semantics opaque (R4)
  Group = -> [Constraint008,Constraint042,Constraint043,Constraint044,Constraint045,Constraint046,Constraint047,Constraint048,Constraint049,Constraint050,Constraint051,Constraint052,Constraint053,Constraint054,Constraint055,Constraint056,Constraint057]
  _LinkVersion = 1
  _Version = 1
FEATURE [App::FeaturePython] Elements003  # WARN: FeaturePython — macro-defined, semantics opaque (R4)
  Group = -> [Element019,Element028,Element034,_Element034,_Element035,_Element036,_Element037,_Element038,_Element039,_Element040,_Element041,_Element042,_Element043,_Element044,_Element045,_Element046,_Element047,_Element048,_Element049,_Element050,_Element051,_Element052,_Element053,_Element054,_Element055,_Element056,_Element057,_Element058,_Element059,_Element060,_Element061,_Element062,_Element063,+3 more]
  _LinkVersion = 1
FEATURE [Part::FeaturePython] Element019  label="1"  # link proxy (typed FeaturePython)
  Detach = false
  LinkTransform = true
  LinkedObject = -> Link008 [Pocket005.Sketch009.Edge1]
  _LinkVersion = 1
  _Parent = -> Elements003
FEATURE [App::FeaturePython] Constraint008  label="Locked003"  # WARN: FeaturePython — macro-defined, semantics opaque (R4)
  Disabled = false
  Group = -> [ElementLink013]
  _ConstraintType = 0
  _LinkVersion = 1
  _Parent = -> Constraints003
FEATURE [App::FeaturePython] ElementLink013  label="1"  # link proxy (typed FeaturePython)
  LinkTransform = true
  LinkedObject = -> Element019
  _LinkVersion = 1
  _Parent = -> Constraint008
FEATURE [Part::FeaturePython] Element020  label="1@Left beam Assembly"  # link proxy (typed FeaturePython)
  Detach = false
  LinkTransform = true
  LinkedObject = -> Link009 [1.$1.]
  _LinkVersion = 1
  _Parent = -> Elements
FEATURE [Part::FeaturePython] Element021  label="2@Left beam Assembly"  # link proxy (typed FeaturePython)
  Detach = false
  LinkTransform = true
  LinkedObject = -> Link009 [1.$2.]
  _LinkVersion = 1
  _Parent = -> Elements
FEATURE [Part::FeaturePython] Element022  label="3@Left beam Assembly"  # link proxy (typed FeaturePython)
  Detach = false
  LinkTransform = true
  LinkedObject = -> Link009 [1.$3.]
  _LinkVersion = 1
  _Parent = -> Elements
FEATURE [Part::FeaturePython] Element023  label="4@Left beam Assembly"  # link proxy (typed FeaturePython)
  Detach = false
  LinkTransform = true
  LinkedObject = -> Link009 [1.$4.]
  _LinkVersion = 1
  _Parent = -> Elements
FEATURE [Part::FeaturePython] Element024  label="1@Right beam Assembly"  # link proxy (typed FeaturePython)
  Detach = false
  LinkTransform = true
  LinkedObject = -> Link010 [1.$1.]
  _LinkVersion = 1
  _Parent = -> Elements
FEATURE [Part::FeaturePython] Element025  label="center-mate-L@HGR20-800 Assembly"  # link proxy (typed FeaturePython)
  Detach = false
  LinkTransform = true
  LinkedObject = -> Link011 [1.$center-mate.]
  _LinkVersion = 1
  _Parent = -> Elements
FEATURE [Part::FeaturePython] Element026  label="center-mate-R@HGR20-800 Assembly"  # link proxy (typed FeaturePython)
  Detach = false
  LinkTransform = true
  LinkedObject = -> Link012 [1.$center-mate.]
  _LinkVersion = 1
  _Parent = -> Elements
FEATURE [Part::FeaturePython] Element027  label="rail-mate"  # link proxy (typed FeaturePython)
  Detach = false
  LinkTransform = true
  LinkedObject = -> Link [Sketch008.Edge1]
  _LinkVersion = 1
  _Parent = -> Elements001
FEATURE [Part::FeaturePython] Element028  label="rail-mate"  # link proxy (typed FeaturePython)
  Detach = false
  LinkTransform = true
  LinkedObject = -> Link008 [Sketch008.Edge1]
  _LinkVersion = 1
  _Parent = -> Elements003
FEATURE [Part::FeaturePython] Element029  label="rail-mate@Left beam Assembly"  # link proxy (typed FeaturePython)
  Detach = false
  LinkTransform = true
  LinkedObject = -> Link009 [1.$rail-mate.]
  _LinkVersion = 1
  _Parent = -> Elements
FEATURE [Part::FeaturePython] Element030  label="rail-mate@Right beam Assembly"  # link proxy (typed FeaturePython)
  Detach = false
  LinkTransform = true
  LinkedObject = -> Link010 [1.$rail-mate.]
  _LinkVersion = 1
  _Parent = -> Elements
FEATURE [App::FeaturePython] Constraint009  label="Attachment-Rail-R"  # WARN: FeaturePython — macro-defined, semantics opaque (R4)
  Cascade = false
  Disabled = false
  Group = -> [ElementLink014,ElementLink015]
  Multiply = false
  _ConstraintType = 45
  _LinkVersion = 1
  _Parent = -> Constraints
FEATURE [App::FeaturePython] ElementLink014  label="rail-mate@Right beam Assembly"  # link proxy (typed FeaturePython)
  LinkTransform = true
  LinkedObject = -> Element030
  _LinkVersion = 1
  _Parent = -> Constraint009
FEATURE [App::FeaturePython] ElementLink015  label="center-mate-R@HGR20-800 Assembly"  # link proxy (typed FeaturePython)
  LinkTransform = true
  LinkedObject = -> Element026
  _LinkVersion = 1
  _Parent = -> Constraint009
FEATURE [App::FeaturePython] Constraint010  label="Attachment-Rail-L"  # WARN: FeaturePython — macro-defined, semantics opaque (R4)
  Cascade = false
  Disabled = false
  Group = -> [ElementLink016,ElementLink017]
  Multiply = false
  _ConstraintType = 45
  _LinkVersion = 1
  _Parent = -> Constraints
FEATURE [App::FeaturePython] ElementLink016  label="rail-mate@Left beam Assembly"  # link proxy (typed FeaturePython)
  LinkTransform = true
  LinkedObject = -> Element029
  _LinkVersion = 1
  _Parent = -> Constraint010
FEATURE [App::FeaturePython] ElementLink017  label="center-mate-L@HGR20-800 Assembly"  # link proxy (typed FeaturePython)
  LinkTransform = true
  LinkedObject = -> Element025
  _LinkVersion = 1
  _Parent = -> Constraint010
FEATURE [Part::FeaturePython] Element031  label="side@HGR20-800 Assembly"  # link proxy (typed FeaturePython)
  Detach = false
  LinkTransform = true
  LinkedObject = -> Link012 [1.$side2.]
  _LinkVersion = 1
  _Parent = -> Elements
FEATURE [Part::FeaturePython] Element032  label="top-mate@HGR20-800 Assembly"  # link proxy (typed FeaturePython)
  Detach = false
  LinkTransform = true
  LinkedObject = -> Link012 [1.$top-mate.]
  _LinkVersion = 1
  _Parent = -> Elements
FEATURE [Part::FeaturePython] Element033  label="point@HGR20-800 Assembly"  # link proxy (typed FeaturePython)
  Detach = false
  LinkTransform = true
  LinkedObject = -> Link012 [1.$point.]
  _LinkVersion = 1
  _Parent = -> Elements
FEATURE [Part::FeaturePython] Element034  label="bf12-mate"  # link proxy (typed FeaturePython)
  Detach = false
  LinkTransform = true
  LinkedObject = -> Link008 [Sketch010.Edge1]
  _LinkVersion = 1
  _Parent = -> Elements003
FEATURE [Part::FeaturePython] Element035  label="bf12-mate"  # link proxy (typed FeaturePython)
  Detach = false
  LinkTransform = true
  LinkedObject = -> Link [Sketch010.Edge2]
  _LinkVersion = 1
  _Parent = -> Elements001
FEATURE [Part::FeaturePython] Element036  label="bf12-plate-mate@Left beam Assembly"  # link proxy (typed FeaturePython)
  Detach = false
  LinkTransform = true
  LinkedObject = -> Link009 [1.$bf12-mate.]
  _LinkVersion = 1
  _Parent = -> Elements
FEATURE [Part::FeaturePython] Element037  label="bf12-plate-mate@Right beam Assembly"  # link proxy (typed FeaturePython)
  Detach = false
  LinkTransform = true
  LinkedObject = -> Link010 [1.$bf12-mate.]
  _LinkVersion = 1
  _Parent = -> Elements
FEATURE [Part::FeaturePython] Element038  label="beam-bottom-mate@BF12L Assembly"  # link proxy (typed FeaturePython)
  Detach = false
  LinkTransform = true
  LinkedObject = -> Link016 [1.$beam-bottom-mate.]
  _LinkVersion = 1
  _Parent = -> Elements
FEATURE [Part::FeaturePython] Element039  label="beam-bottom-mate@BF12R Assembly"  # link proxy (typed FeaturePython)
  Detach = false
  LinkTransform = true
  LinkedObject = -> Link015 [1.$beam-bottom-mate.]
  _LinkVersion = 1
  _Parent = -> Elements
FEATURE [App::FeaturePython] Constraint011  label="Attachment-bf-plate-R"  # WARN: FeaturePython — macro-defined, semantics opaque (R4)
  Cascade = false
  Disabled = false
  Group = -> [ElementLink018,ElementLink019]
  Multiply = false
  _ConstraintType = 45
  _LinkVersion = 1
  _Parent = -> Constraints
FEATURE [App::FeaturePython] ElementLink018  label="beam-bottom-mate@BF12R Assembly"  # link proxy (typed FeaturePython)
  LinkTransform = true
  LinkedObject = -> Element039
  Offset = pos=(0,0,0) rot=(0,0,1;4.71239rad)
  Placement = pos=(0,-366.9,-443.1) rot=(-1,0,0;1.5708rad)
  _LinkVersion = 1
  _Parent = -> Constraint011
FEATURE [App::FeaturePython] ElementLink019  label="bf12-plate-mate@Right beam Assembly"  # link proxy (typed FeaturePython)
  LinkTransform = true
  LinkedObject = -> Element037
  _LinkVersion = 1
  _Parent = -> Constraint011
FEATURE [App::FeaturePython] Constraint012  label="Attachment-bf-plate-L"  # WARN: FeaturePython — macro-defined, semantics opaque (R4)
  Cascade = false
  Disabled = false
  Group = -> [ElementLink020,ElementLink021]
  Multiply = false
  _ConstraintType = 45
  _LinkVersion = 1
  _Parent = -> Constraints
FEATURE [App::FeaturePython] ElementLink020  label="beam-bottom-mate@BF12L Assembly"  # link proxy (typed FeaturePython)
  LinkTransform = true
  LinkedObject = -> Element038
  Offset = pos=(0,0,0) rot=(0,0,1;4.71239rad)
  Placement = pos=(1.78e-14,-366.9,-443.1) rot=(-1,0,0;1.5708rad)
  _LinkVersion = 1
  _Parent = -> Constraint012
FEATURE [App::FeaturePython] ElementLink021  label="bf12-plate-mate@Left beam Assembly"  # link proxy (typed FeaturePython)
  LinkTransform = true
  LinkedObject = -> Element036
  Offset = pos=(0,0,0) rot=(1,0,0;3.14159rad)
  Placement = pos=(-50.8,-810,-1.705e-13) rot=(0,0,1;3.14159rad)
  _LinkVersion = 1
  _Parent = -> Constraint012
FEATURE [Part::FeaturePython] Element040  label="bf12-mount@Ballscrew-800-Assembly"  # link proxy (typed FeaturePython)
  Detach = false
  LinkTransform = true
  LinkedObject = -> Link014 [1.$mount2@BF12-Assembly.]
  _LinkVersion = 1
  _Parent = -> Elements
FEATURE [Part::FeaturePython] Element041  label="BF-top-mate@BF12R Assembly"  # link proxy (typed FeaturePython)
  Detach = false
  LinkTransform = true
  LinkedObject = -> Link015 [1.$BF-top-mate.]
  _LinkVersion = 1
  _Parent = -> Elements
FEATURE [App::FeaturePython] Constraint013  label="Attachment-screw-R"  # WARN: FeaturePython — macro-defined, semantics opaque (R4)
  Cascade = false
  Disabled = false
  Group = -> [ElementLink022,ElementLink023]
  Multiply = false
  _ConstraintType = 45
  _LinkVersion = 1
  _Parent = -> Constraints
FEATURE [App::FeaturePython] ElementLink022  label="BF-top-mate@BF12R Assembly"  # link proxy (typed FeaturePython)
  LinkTransform = true
  LinkedObject = -> Element041
  Offset = pos=(0,0,0) rot=(1,0,0;3.14159rad)
  Placement = pos=(1058.4,-3.979e-13,15.8) rot=(0,1,0;3.14159rad)
  _LinkVersion = 1
  _Parent = -> Constraint013
FEATURE [App::FeaturePython] ElementLink023  label="bf12-mount@Ballscrew-800-Assembly"  # link proxy (typed FeaturePython)
  LinkTransform = true
  LinkedObject = -> Element040
  Offset = pos=(0,0,0) rot=(0,0,1;-1.5708rad)
  Placement = pos=(1.24256e-06,-397.1,412.9) rot=(1,0,0;1.5708rad)
  _LinkVersion = 1
  _Parent = -> Constraint013
FEATURE [Part::FeaturePython] Element042  label="BF-top-mate@BF12L Assembly"  # link proxy (typed FeaturePython)
  Detach = false
  LinkTransform = true
  LinkedObject = -> Link016 [1.$BF-top-mate.]
  _LinkVersion = 1
  _Parent = -> Elements
FEATURE [Part::FeaturePython] Element043  label="bf12-mount@Ballscrew-800-Assembly001"  # link proxy (typed FeaturePython)
  Detach = false
  LinkTransform = true
  LinkedObject = -> Link013 [1.$mount1@BF12-Assembly.]
  _LinkVersion = 1
  _Parent = -> Elements
FEATURE [App::FeaturePython] Constraint014  label="Attachment-screw-L"  # WARN: FeaturePython — macro-defined, semantics opaque (R4)
  Cascade = false
  Disabled = false
  Group = -> [ElementLink024,ElementLink025]
  Multiply = false
  _ConstraintType = 45
  _LinkVersion = 1
  _Parent = -> Constraints
FEATURE [App::FeaturePython] ElementLink024  label="bf12-mount@Ballscrew-800-Assembly001"  # link proxy (typed FeaturePython)
  LinkTransform = true
  LinkedObject = -> Element043
  _LinkVersion = 1
  _Parent = -> Constraint014
FEATURE [App::FeaturePython] ElementLink025  label="BF-top-mate@BF12L Assembly"  # link proxy (typed FeaturePython)
  LinkTransform = true
  LinkedObject = -> Element042
  Offset = pos=(0,0,0) rot=(0,0,1;-1.5708rad)
  Placement = pos=(2.84e-14,-412.9,-397.1) rot=(-1,0,0;1.5708rad)
  _LinkVersion = 1
  _Parent = -> Constraint014
FEATURE [Part::FeaturePython] Element044  label="BK-tr-mate@BK12R Assembly"  # link proxy (typed FeaturePython)
  Detach = false
  LinkTransform = true
  LinkedObject = -> Link018 [1.$BK-tr-mate.]
  _LinkVersion = 1
  _Parent = -> Elements
FEATURE [Part::FeaturePython] Element045  label="BK-tr-mate@BK12L Assembly"  # link proxy (typed FeaturePython)
  Detach = false
  LinkTransform = true
  LinkedObject = -> Link017 [1.$BK-tr-mate.]
  _LinkVersion = 1
  _Parent = -> Elements
FEATURE [Part::FeaturePython] Element046  label="bk12-mount@Ballscrew-800-Assembly"  # link proxy (typed FeaturePython)
  Detach = false
  LinkTransform = true
  LinkedObject = -> Link014 [1.$mount1@BK12-Assembly.]
  _LinkVersion = 1
  _Parent = -> Elements
FEATURE [App::FeaturePython] Constraint015  label="Attachment-BK-plate-R"  # WARN: FeaturePython — macro-defined, semantics opaque (R4)
  Cascade = false
  Disabled = false
  Group = -> [ElementLink026,ElementLink027]
  Multiply = false
  _ConstraintType = 45
  _LinkVersion = 1
  _Parent = -> Constraints
FEATURE [App::FeaturePython] ElementLink026  label="BK-tr-mate@BK12R Assembly"  # link proxy (typed FeaturePython)
  LinkTransform = true
  LinkedObject = -> Element044
  Offset = pos=(0,0,0) rot=(1,0,0;3.14159rad)
  Placement = pos=(1058.4,-3.31182e-06,15.8) rot=(0,1,0;3.14159rad)
  _LinkVersion = 1
  _Parent = -> Constraint015
FEATURE [App::FeaturePython] ElementLink027  label="bk12-mount@Ballscrew-800-Assembly"  # link proxy (typed FeaturePython)
  LinkTransform = true
  LinkedObject = -> Element046
  Offset = pos=(0,0,0) rot=(0,0,1;1.5708rad)
  Placement = pos=(-1.08172e-06,345.7,361.5) rot=(-1,0,0;1.5708rad)
  _LinkVersion = 1
  _Parent = -> Constraint015
FEATURE [Part::FeaturePython] Element047  label="bk12-mount@Ballscrew-800-Assembly001"  # link proxy (typed FeaturePython)
  Detach = false
  LinkTransform = true
  LinkedObject = -> Link013 [1.$mount2@BK12-Assembly.]
  _LinkVersion = 1
  _Parent = -> Elements
FEATURE [App::FeaturePython] Constraint016  label="Attachment-BK-plate-L"  # WARN: FeaturePython — macro-defined, semantics opaque (R4)
  Cascade = false
  Disabled = false
  Group = -> [ElementLink028,ElementLink029]
  Multiply = false
  _ConstraintType = 45
  _LinkVersion = 1
  _Parent = -> Constraints
FEATURE [App::FeaturePython] ElementLink028  label="BK-tr-mate@BK12L Assembly"  # link proxy (typed FeaturePython)
  LinkTransform = true
  LinkedObject = -> Element045
  _LinkVersion = 1
  _Parent = -> Constraint016
FEATURE [App::FeaturePython] ElementLink029  label="bk12-mount@Ballscrew-800-Assembly001"  # link proxy (typed FeaturePython)
  LinkTransform = true
  LinkedObject = -> Element047
  Offset = pos=(0,0,0) rot=(0,0,1;-1.5708rad)
  Placement = pos=(4.761e-13,332.7,348.5) rot=(-1,0,0;1.5708rad)
  _LinkVersion = 1
  _Parent = -> Constraint016
FEATURE [Part::FeaturePython] Element048  label="screw-mate@Coupling-Assembly"  # link proxy (typed FeaturePython)
  Detach = false
  LinkTransform = true
  LinkedObject = -> Link020 [1.$screw-mate.]
  _LinkVersion = 1
  _Parent = -> Elements
FEATURE [Part::FeaturePython] Element049  label="motor-mate@Coupling-Assembly"  # link proxy (typed FeaturePython)
  Detach = false
  LinkTransform = true
  LinkedObject = -> Link020 [1.$motor-mate.]
  _LinkVersion = 1
  _Parent = -> Elements
FEATURE [Part::FeaturePython] Element050  label="motor-mate@Coupling-Assembly-L"  # link proxy (typed FeaturePython)
  Detach = false
  LinkTransform = true
  LinkedObject = -> Link019 [1.$motor-mate.]
  _LinkVersion = 1
  _Parent = -> Elements
FEATURE [Part::FeaturePython] Element051  label="screw-mate@Coupling-Assembly-L"  # link proxy (typed FeaturePython)
  Detach = false
  LinkTransform = true
  LinkedObject = -> Link019 [1.$screw-mate.]
  _LinkVersion = 1
  _Parent = -> Elements
FEATURE [Part::FeaturePython] Element052  label="coupling-mate@Ballscrew-800-Assembly"  # link proxy (typed FeaturePython)
  Detach = false
  LinkTransform = true
  LinkedObject = -> Link014 [1.$coupling-mate.]
  _LinkVersion = 1
  _Parent = -> Elements
FEATURE [Part::FeaturePython] Element053  label="coupling-mate@Ballscrew-800-Assembly-L"  # link proxy (typed FeaturePython)
  Detach = false
  LinkTransform = true
  LinkedObject = -> Link013 [1.$coupling-mate.]
  _LinkVersion = 1
  _Parent = -> Elements
FEATURE [App::FeaturePython] Constraint017  label="Attachment-screw-coupling-R"  # WARN: FeaturePython — macro-defined, semantics opaque (R4)
  Cascade = false
  Disabled = false
  Group = -> [ElementLink030,ElementLink031]
  Multiply = false
  _ConstraintType = 45
  _LinkVersion = 1
  _Parent = -> Constraints
FEATURE [App::FeaturePython] ElementLink030  label="coupling-mate@Ballscrew-800-Assembly"  # link proxy (typed FeaturePython)
  LinkTransform = true
  LinkedObject = -> Element052
  Offset = pos=(0,0,0.35) rot=(1,0,0;3.14159rad)
  Placement = pos=(1108.4,776.55,-2.8493e-12) rot=(0,0,1;3.14159rad)
  _LinkVersion = 1
  _Parent = -> Constraint017
FEATURE [App::FeaturePython] ElementLink031  label="screw-mate@Coupling-Assembly"  # link proxy (typed FeaturePython)
  LinkTransform = true
  LinkedObject = -> Element048
  _LinkVersion = 1
  _Parent = -> Constraint017
FEATURE [App::FeaturePython] Constraint018  label="Attachment-screw-coupling-L"  # WARN: FeaturePython — macro-defined, semantics opaque (R4)
  Cascade = false
  Disabled = false
  Group = -> [ElementLink032,ElementLink033]
  Multiply = false
  _ConstraintType = 45
  _LinkVersion = 1
  _Parent = -> Constraints
FEATURE [App::FeaturePython] ElementLink032  label="coupling-mate@Ballscrew-800-Assembly-L"  # link proxy (typed FeaturePython)
  LinkTransform = true
  LinkedObject = -> Element053
  Offset = pos=(0,0,0.35) rot=(1,0,0;3.14159rad)
  Placement = pos=(-110.8,776.55,2.2435e-12) rot=(0,0,1;3.14159rad)
  _LinkVersion = 1
  _Parent = -> Constraint018
FEATURE [App::FeaturePython] ElementLink033  label="screw-mate@Coupling-Assembly-L"  # link proxy (typed FeaturePython)
  LinkTransform = true
  LinkedObject = -> Element051
  _LinkVersion = 1
  _Parent = -> Constraint018
FEATURE [Part::FeaturePython] Element054  label="coupling-mate@NEMA23-76-Assembly-L"  # link proxy (typed FeaturePython)
  Detach = false
  LinkTransform = true
  LinkedObject = -> Link021 [1.$coupling-mate.]
  _LinkVersion = 1
  _Parent = -> Elements
FEATURE [Part::FeaturePython] Element055  label="coupling-mate@NEMA23-76-Assembly-R"  # link proxy (typed FeaturePython)
  Detach = false
  LinkTransform = true
  LinkedObject = -> Link022 [1.$coupling-mate.]
  _LinkVersion = 1
  _Parent = -> Elements
FEATURE [App::FeaturePython] Constraint019  label="Attachment-motor-L"  # WARN: FeaturePython — macro-defined, semantics opaque (R4)
  Cascade = false
  Disabled = false
  Group = -> [ElementLink034,ElementLink035]
  Multiply = false
  _ConstraintType = 45
  _LinkVersion = 1
  _Parent = -> Constraints
FEATURE [App::FeaturePython] ElementLink034  label="coupling-mate@NEMA23-76-Assembly-L"  # link proxy (typed FeaturePython)
  LinkTransform = true
  LinkedObject = -> Element054
  Offset = pos=(0,0,0.3) rot=(0,0,1;0rad)
  Placement = pos=(-7.1e-15,-0.3,-1.8e-15) rot=(0,0,1;0rad)
  _LinkVersion = 1
  _Parent = -> Constraint019
FEATURE [App::FeaturePython] ElementLink035  label="motor-mate@Coupling-Assembly-L"  # link proxy (typed FeaturePython)
  LinkTransform = true
  LinkedObject = -> Element050
  _LinkVersion = 1
  _Parent = -> Constraint019
FEATURE [App::FeaturePython] Constraint020  label="Attachment-motor-R"  # WARN: FeaturePython — macro-defined, semantics opaque (R4)
  Cascade = false
  Disabled = false
  Group = -> [ElementLink036,ElementLink037]
  Multiply = false
  _ConstraintType = 45
  _LinkVersion = 1
  _Parent = -> Constraints
FEATURE [App::FeaturePython] ElementLink036  label="coupling-mate@NEMA23-76-Assembly-R"  # link proxy (typed FeaturePython)
  LinkTransform = true
  LinkedObject = -> Element055
  Offset = pos=(0,0,0.3) rot=(0,0,1;0rad)
  Placement = pos=(0,-0.3,3.6e-15) rot=(0,0,1;0rad)
  _LinkVersion = 1
  _Parent = -> Constraint020
FEATURE [App::FeaturePython] ElementLink037  label="motor-mate@Coupling-Assembly"  # link proxy (typed FeaturePython)
  LinkTransform = true
  LinkedObject = -> Element049
  _LinkVersion = 1
  _Parent = -> Constraint020
FEATURE [Part::FeaturePython] Element058  label="bracket-mate-L@NEMA23-76-Assembly"  # link proxy (typed FeaturePython)
  Detach = false
  LinkTransform = true
  LinkedObject = -> Link021 [1.$bracket-mate.]
  _LinkVersion = 1
  _Parent = -> Elements
FEATURE [Part::FeaturePython] Element059  label="bracket-mate-R@NEMA23-76-Assembly"  # link proxy (typed FeaturePython)
  Detach = false
  LinkTransform = true
  LinkedObject = -> Link022 [1.$bracket-mate.]
  _LinkVersion = 1
  _Parent = -> Elements
FEATURE [Part::FeaturePython] Element060  label="motor mate@Motor plate L Assembly"  # link proxy (typed FeaturePython)
  Detach = false
  LinkTransform = true
  LinkedObject = -> Link024 [1.$motor mate.]
  _LinkVersion = 1
  _Parent = -> Elements
FEATURE [Part::FeaturePython] Element061  label="motor mate@Motor plate R Assembly"  # link proxy (typed FeaturePython)
  Detach = false
  LinkTransform = true
  LinkedObject = -> Link023 [1.$motor mate.]
  _LinkVersion = 1
  _Parent = -> Elements
FEATURE [App::FeaturePython] Constraint021  label="Attachment-motor Right"  # WARN: FeaturePython — macro-defined, semantics opaque (R4)
  Cascade = false
  Disabled = false
  Group = -> [ElementLink038,ElementLink039]
  Multiply = false
  _ConstraintType = 45
  _LinkVersion = 1
  _Parent = -> Constraints
FEATURE [App::FeaturePython] ElementLink038  label="motor mate@Motor plate R Assembly"  # link proxy (typed FeaturePython)
  LinkTransform = true
  LinkedObject = -> Element061
  Offset = pos=(0,0,0) rot=(0,0,1;4.71239rad)
  Placement = pos=(539.1,1.68689e-06,-569.3) rot=(0,-1,0;1.5708rad)
  _LinkVersion = 1
  _Parent = -> Constraint021
FEATURE [App::FeaturePython] ElementLink039  label="bracket-mate-R@NEMA23-76-Assembly"  # link proxy (typed FeaturePython)
  LinkTransform = true
  LinkedObject = -> Element059
  Offset = pos=(0,0,0) rot=(1,0,0;3.14159rad)
  Placement = pos=(1108.4,842.7,-4.782e-12) rot=(0,0,1;3.14159rad)
  _LinkVersion = 1
  _Parent = -> Constraint021
FEATURE [App::FeaturePython] Constraint022  label="Attachment-motor Left"  # WARN: FeaturePython — macro-defined, semantics opaque (R4)
  Cascade = false
  Disabled = false
  Group = -> [ElementLink040,ElementLink041]
  Multiply = false
  _ConstraintType = 45
  _LinkVersion = 1
  _Parent = -> Constraints
FEATURE [App::FeaturePython] ElementLink040  label="motor mate@Motor plate L Assembly"  # link proxy (typed FeaturePython)
  LinkTransform = true
  LinkedObject = -> Element060
  Offset = pos=(0,0,0) rot=(0,0,1;1.5708rad)
  Placement = pos=(-70.5,-5.68e-14,40.3) rot=(0,-1,0;1.5708rad)
  _LinkVersion = 1
  _Parent = -> Constraint022
FEATURE [App::FeaturePython] ElementLink041  label="bracket-mate-L@NEMA23-76-Assembly"  # link proxy (typed FeaturePython)
  LinkTransform = true
  LinkedObject = -> Element058
  _LinkVersion = 1
  _Parent = -> Constraint022
FEATURE [Part::FeaturePython] Element062  label="frame mate@Table Assembly"  # link proxy (typed FeaturePython)
  Detach = false
  LinkTransform = true
  LinkedObject = -> Link025 [1.$frame mate.]
  _LinkVersion = 1
  _Parent = -> Elements
FEATURE [Part::FeaturePython] Element063  # link proxy (typed FeaturePython)
  Detach = false
  LinkTransform = true
  LinkedObject = -> Link001 [Sketch011.Edge1]
  _LinkVersion = 1
  _Parent = -> Elements002
FEATURE [Part::FeaturePython] Element064  label="table-mate"  # link proxy (typed FeaturePython)
  Detach = false
  LinkTransform = true
  LinkedObject = -> Link003 [1.$Element063.]
  _LinkVersion = 1
  _Parent = -> Elements
FEATURE [App::FeaturePython] Constraint023  label="Attachment-table"  # WARN: FeaturePython — macro-defined, semantics opaque (R4)
  Cascade = false
  Disabled = false
  Group = -> [ElementLink042,ElementLink043]
  Multiply = false
  _ConstraintType = 45
  _LinkVersion = 1
  _Parent = -> Constraints
FEATURE [App::FeaturePython] ElementLink042  label="table-mate"  # link proxy (typed FeaturePython)
  LinkTransform = true
  LinkedObject = -> Element064
  Offset = pos=(0,0,0) rot=(0.707107,-0.707107,0;3.14159rad)
  Placement = pos=(438.8,-438.8,-6.687e-13) rot=(0.707107,0.707107,0;3.14159rad)
  _LinkVersion = 1
  _Parent = -> Constraint023
FEATURE [App::FeaturePython] ElementLink043  label="frame mate@Table Assembly"  # link proxy (typed FeaturePython)
  LinkTransform = true
  LinkedObject = -> Element062
  Offset = pos=(0,0,0) rot=(0,0,1;3.14159rad)
  Placement = pos=(123.8,-753.8,2.202e-13) rot=(0,0,1;3.14159rad)
  _LinkVersion = 1
  _Parent = -> Constraint023
FEATURE [Part::FeaturePython] Assembly004  label="1/4x1 screw and washer Assembly"  # WARN: FeaturePython — macro-defined, semantics opaque (R4)
  AutoRelax = true
  BuildShape = 0
  Freeze = false
  Group = -> [Constraints004,Elements004,Parts004]
  Verbose = false
  _LinkVersion = 1
  _SolverType = 1
  _Version = 1
FEATURE [App::FeaturePython] Constraints004  # WARN: FeaturePython — macro-defined, semantics opaque (R4)
  Group = -> [Constraint024,Constraint025]
  _LinkVersion = 1
  _Version = 1
FEATURE [App::FeaturePython] Elements004  # WARN: FeaturePython — macro-defined, semantics opaque (R4)
  Group = -> [_Element,_Element001,Element065]
  _LinkVersion = 1
FEATURE [App::FeaturePython] Constraint024  label="Locked004"  # WARN: FeaturePython — macro-defined, semantics opaque (R4)
  Disabled = false
  Group = -> [ElementLink044]
  _ConstraintType = 0
  _LinkVersion = 1
  _Parent = -> Constraints004
FEATURE [App::FeaturePython] ElementLink044  label="_Element"  # link proxy (typed FeaturePython)
  LinkTransform = true
  LinkedObject = -> _Element
  _LinkVersion = 1
  _Parent = -> Constraint024
FEATURE [Part::FeaturePython] _Element  # link proxy (typed FeaturePython)
  Detach = false
  LinkTransform = true
  LinkedObject = -> Screw [Edge4]
  _LinkVersion = 1
  _Parent = -> Elements004
FEATURE [App::FeaturePython] Constraint025  label="Attachment"  # WARN: FeaturePython — macro-defined, semantics opaque (R4)
  Cascade = false
  Disabled = false
  Group = -> [ElementLink045,ElementLink046]
  Multiply = false
  _ConstraintType = 45
  _LinkVersion = 1
  _Parent = -> Constraints004
FEATURE [App::FeaturePython] ElementLink045  label="_Element001"  # link proxy (typed FeaturePython)
  LinkTransform = true
  LinkedObject = -> _Element001
  _LinkVersion = 1
  _Parent = -> Constraint025
FEATURE [Part::FeaturePython] _Element001  # link proxy (typed FeaturePython)
  Detach = false
  LinkTransform = true
  LinkedObject = -> Washer [Edge1]
  _LinkVersion = 1
  _Parent = -> Elements004
FEATURE [App::FeaturePython] ElementLink046  label="_Element"  # link proxy (typed FeaturePython)
  LinkTransform = true
  LinkedObject = -> _Element
  _LinkVersion = 1
  _Parent = -> Constraint025
FEATURE [Part::FeaturePython] Element065  label="mate"  # link proxy (typed FeaturePython)
  Detach = false
  LinkTransform = true
  LinkedObject = -> Washer [Edge5]
  Offset = pos=(0,0,0) rot=(1,0,0;3.14159rad)
  Placement = pos=(0,-2e-16,-3.2004) rot=(1,0,0;3.14159rad)
  _LinkVersion = 1
  _Parent = -> Elements004
FEATURE [App::FeaturePython] Constraint026  label="Attachment001"  # WARN: FeaturePython — macro-defined, semantics opaque (R4)
  Cascade = false
  Disabled = false
  Group = -> [ElementLink047,ElementLink048]
  Multiply = false
  _ConstraintType = 45
  _LinkVersion = 1
  _Parent = -> Constraints001
FEATURE [App::FeaturePython] ElementLink047  label="_Element002"  # link proxy (typed FeaturePython)
  LinkTransform = true
  LinkedObject = -> _Element002
  Placement = pos=(9.95e-14,0,-1.8e-15) rot=(0,0,1;0rad)
  _LinkVersion = 1
  _Parent = -> Constraint026
FEATURE [Part::FeaturePython] _Element002  # link proxy (typed FeaturePython)
  Detach = false
  LinkTransform = true
  LinkedObject = -> Link [Sketch009.Edge13]
  _LinkVersion = 1
  _Parent = -> Elements001
FEATURE [App::FeaturePython] ElementLink048  label="_Element003"  # link proxy (typed FeaturePython)
  LinkTransform = true
  LinkedObject = -> _Element003
  _LinkVersion = 1
  _Parent = -> Constraint026
FEATURE [Part::FeaturePython] _Element003  # link proxy (typed FeaturePython)
  Detach = false
  LinkTransform = true
  LinkedObject = -> Link026 [Link026_i0.1.$mate.]
  _LinkVersion = 1
  _Parent = -> Elements001
FEATURE [App::FeaturePython] Constraint027  label="Attachment002"  # WARN: FeaturePython — macro-defined, semantics opaque (R4)
  Cascade = false
  Disabled = false
  Group = -> [ElementLink049,ElementLink050]
  Multiply = false
  _ConstraintType = 45
  _LinkVersion = 1
  _Parent = -> Constraints001
FEATURE [App::FeaturePython] ElementLink049  label="_Element004"  # link proxy (typed FeaturePython)
  LinkTransform = true
  LinkedObject = -> _Element004
  Placement = pos=(8.88e-14,5.68e-14,0) rot=(0,0,1;0rad)
  _LinkVersion = 1
  _Parent = -> Constraint027
FEATURE [Part::FeaturePython] _Element004  # link proxy (typed FeaturePython)
  Detach = false
  LinkTransform = true
  LinkedObject = -> Link026 [Link026_i1.1.$mate.]
  _LinkVersion = 1
  _Parent = -> Elements001
FEATURE [App::FeaturePython] ElementLink050  label="_Element005"  # link proxy (typed FeaturePython)
  LinkTransform = true
  LinkedObject = -> _Element005
  _LinkVersion = 1
  _Parent = -> Constraint027
FEATURE [Part::FeaturePython] _Element005  # link proxy (typed FeaturePython)
  Detach = false
  LinkTransform = true
  LinkedObject = -> Link [Sketch009.Edge15]
  _LinkVersion = 1
  _Parent = -> Elements001
FEATURE [App::FeaturePython] Constraint028  label="Attachment003"  # WARN: FeaturePython — macro-defined, semantics opaque (R4)
  Cascade = false
  Disabled = false
  Group = -> [ElementLink051,ElementLink052]
  Multiply = false
  _ConstraintType = 45
  _LinkVersion = 1
  _Parent = -> Constraints001
FEATURE [App::FeaturePython] ElementLink051  label="_Element006"  # link proxy (typed FeaturePython)
  LinkTransform = true
  LinkedObject = -> _Element006
  Placement = pos=(9.59e-14,0,0) rot=(0,0,1;0rad)
  _LinkVersion = 1
  _Parent = -> Constraint028
FEATURE [Part::FeaturePython] _Element006  # link proxy (typed FeaturePython)
  Detach = false
  LinkTransform = true
  LinkedObject = -> Link [Sketch009.Edge14]
  _LinkVersion = 1
  _Parent = -> Elements001
FEATURE [App::FeaturePython] ElementLink052  label="_Element007"  # link proxy (typed FeaturePython)
  LinkTransform = true
  LinkedObject = -> _Element007
  _LinkVersion = 1
  _Parent = -> Constraint028
FEATURE [Part::FeaturePython] _Element007  # link proxy (typed FeaturePython)
  Detach = false
  LinkTransform = true
  LinkedObject = -> Link026 [Link026_i2.1.$mate.]
  _LinkVersion = 1
  _Parent = -> Elements001
FEATURE [App::FeaturePython] Constraint029  label="Attachment004"  # WARN: FeaturePython — macro-defined, semantics opaque (R4)
  Cascade = false
  Disabled = false
  Group = -> [ElementLink053,ElementLink054]
  Multiply = false
  _ConstraintType = 45
  _LinkVersion = 1
  _Parent = -> Constraints001
FEATURE [App::FeaturePython] ElementLink053  label="_Element008"  # link proxy (typed FeaturePython)
  LinkTransform = true
  LinkedObject = -> _Element008
  Placement = pos=(8.88e-14,5.68e-14,0) rot=(0,0,1;0rad)
  _LinkVersion = 1
  _Parent = -> Constraint029
FEATURE [Part::FeaturePython] _Element008  # link proxy (typed FeaturePython)
  Detach = false
  LinkTransform = true
  LinkedObject = -> Link026 [Link026_i3.1.$mate.]
  _LinkVersion = 1
  _Parent = -> Elements001
FEATURE [App::FeaturePython] ElementLink054  label="_Element009"  # link proxy (typed FeaturePython)
  LinkTransform = true
  LinkedObject = -> _Element009
  _LinkVersion = 1
  _Parent = -> Constraint029
FEATURE [Part::FeaturePython] _Element009  # link proxy (typed FeaturePython)
  Detach = false
  LinkTransform = true
  LinkedObject = -> Link [Sketch009.Edge16]
  _LinkVersion = 1
  _Parent = -> Elements001
FEATURE [App::FeaturePython] Constraint030  label="Attachment005"  # WARN: FeaturePython — macro-defined, semantics opaque (R4)
  Cascade = false
  Disabled = false
  Group = -> [ElementLink055,ElementLink056]
  Multiply = false
  _ConstraintType = 45
  _LinkVersion = 1
  _Parent = -> Constraints001
FEATURE [App::FeaturePython] ElementLink055  label="_Element010"  # link proxy (typed FeaturePython)
  LinkTransform = true
  LinkedObject = -> _Element010
  Placement = pos=(3.55e-14,2.84e-14,1.8e-15) rot=(0,0,1;0rad)
  _LinkVersion = 1
  _Parent = -> Constraint030
FEATURE [Part::FeaturePython] _Element010  # link proxy (typed FeaturePython)
  Detach = false
  LinkTransform = true
  LinkedObject = -> Link026 [Link026_i4.1.$mate.]
  _LinkVersion = 1
  _Parent = -> Elements001
FEATURE [App::FeaturePython] ElementLink056  label="_Element011"  # link proxy (typed FeaturePython)
  LinkTransform = true
  LinkedObject = -> _Element011
  _LinkVersion = 1
  _Parent = -> Constraint030
FEATURE [Part::FeaturePython] _Element011  # link proxy (typed FeaturePython)
  Detach = false
  LinkTransform = true
  LinkedObject = -> Link [Sketch009.Edge12]
  _LinkVersion = 1
  _Parent = -> Elements001
FEATURE [App::FeaturePython] Constraint031  label="Attachment006"  # WARN: FeaturePython — macro-defined, semantics opaque (R4)
  Cascade = false
  Disabled = false
  Group = -> [ElementLink057,ElementLink058]
  Multiply = false
  _ConstraintType = 45
  _LinkVersion = 1
  _Parent = -> Constraints001
FEATURE [App::FeaturePython] ElementLink057  label="_Element012"  # link proxy (typed FeaturePython)
  LinkTransform = true
  LinkedObject = -> _Element012
  Placement = pos=(2.84e-14,1.42e-14,0) rot=(0,0,1;0rad)
  _LinkVersion = 1
  _Parent = -> Constraint031
FEATURE [Part::FeaturePython] _Element012  # link proxy (typed FeaturePython)
  Detach = false
  LinkTransform = true
  LinkedObject = -> Link026 [Link026_i5.1.$mate.]
  _LinkVersion = 1
  _Parent = -> Elements001
FEATURE [App::FeaturePython] ElementLink058  label="_Element013"  # link proxy (typed FeaturePython)
  LinkTransform = true
  LinkedObject = -> _Element013
  _LinkVersion = 1
  _Parent = -> Constraint031
FEATURE [Part::FeaturePython] _Element013  # link proxy (typed FeaturePython)
  Detach = false
  LinkTransform = true
  LinkedObject = -> Link [Sketch009.Edge10]
  _LinkVersion = 1
  _Parent = -> Elements001
FEATURE [App::FeaturePython] Constraint032  label="Attachment007"  # WARN: FeaturePython — macro-defined, semantics opaque (R4)
  Cascade = false
  Disabled = false
  Group = -> [ElementLink059,ElementLink060]
  Multiply = false
  _ConstraintType = 45
  _LinkVersion = 1
  _Parent = -> Constraints001
FEATURE [App::FeaturePython] ElementLink059  label="_Element014"  # link proxy (typed FeaturePython)
  LinkTransform = true
  LinkedObject = -> _Element014
  Placement = pos=(3.55e-14,2.84e-14,7.1e-15) rot=(0,0,1;0rad)
  _LinkVersion = 1
  _Parent = -> Constraint032
FEATURE [Part::FeaturePython] _Element014  # link proxy (typed FeaturePython)
  Detach = false
  LinkTransform = true
  LinkedObject = -> Link026 [Link026_i6.1.$mate.]
  _LinkVersion = 1
  _Parent = -> Elements001
FEATURE [App::FeaturePython] ElementLink060  label="_Element015"  # link proxy (typed FeaturePython)
  LinkTransform = true
  LinkedObject = -> _Element015
  _LinkVersion = 1
  _Parent = -> Constraint032
FEATURE [Part::FeaturePython] _Element015  # link proxy (typed FeaturePython)
  Detach = false
  LinkTransform = true
  LinkedObject = -> Link [Sketch009.Edge11]
  _LinkVersion = 1
  _Parent = -> Elements001
FEATURE [App::FeaturePython] Constraint033  label="Attachment008"  # WARN: FeaturePython — macro-defined, semantics opaque (R4)
  Cascade = false
  Disabled = false
  Group = -> [ElementLink061,ElementLink062]
  Multiply = false
  _ConstraintType = 45
  _LinkVersion = 1
  _Parent = -> Constraints001
FEATURE [App::FeaturePython] ElementLink061  label="_Element016"  # link proxy (typed FeaturePython)
  LinkTransform = true
  LinkedObject = -> _Element016
  Placement = pos=(2.84e-14,-1.42e-14,7.1e-15) rot=(0,0,1;0rad)
  _LinkVersion = 1
  _Parent = -> Constraint033
FEATURE [Part::FeaturePython] _Element016  # link proxy (typed FeaturePython)
  Detach = false
  LinkTransform = true
  LinkedObject = -> Link026 [Link026_i7.1.$mate.]
  _LinkVersion = 1
  _Parent = -> Elements001
FEATURE [App::FeaturePython] ElementLink062  label="_Element017"  # link proxy (typed FeaturePython)
  LinkTransform = true
  LinkedObject = -> _Element017
  _LinkVersion = 1
  _Parent = -> Constraint033
FEATURE [Part::FeaturePython] _Element017  # link proxy (typed FeaturePython)
  Detach = false
  LinkTransform = true
  LinkedObject = -> Link [Sketch009.Edge9]
  _LinkVersion = 1
  _Parent = -> Elements001
FEATURE [App::FeaturePython] Constraint034  label="Attachment009"  # WARN: FeaturePython — macro-defined, semantics opaque (R4)
  Cascade = false
  Disabled = false
  Group = -> [ElementLink063,ElementLink064]
  Multiply = false
  _ConstraintType = 45
  _LinkVersion = 1
  _Parent = -> Constraints001
FEATURE [App::FeaturePython] ElementLink063  label="_Element018"  # link proxy (typed FeaturePython)
  LinkTransform = true
  LinkedObject = -> _Element018
  Placement = pos=(-3.55e-14,-2.84e-14,1.8e-15) rot=(0,0,1;0rad)
  _LinkVersion = 1
  _Parent = -> Constraint034
FEATURE [Part::FeaturePython] _Element018  # link proxy (typed FeaturePython)
  Detach = false
  LinkTransform = true
  LinkedObject = -> Link026 [Link026_i8.1.$mate.]
  _LinkVersion = 1
  _Parent = -> Elements001
FEATURE [App::FeaturePython] ElementLink064  label="_Element019"  # link proxy (typed FeaturePython)
  LinkTransform = true
  LinkedObject = -> _Element019
  _LinkVersion = 1
  _Parent = -> Constraint034
FEATURE [Part::FeaturePython] _Element019  # link proxy (typed FeaturePython)
  Detach = false
  LinkTransform = true
  LinkedObject = -> Link [Sketch009.Edge5]
  _LinkVersion = 1
  _Parent = -> Elements001
FEATURE [App::FeaturePython] Constraint035  label="Attachment010"  # WARN: FeaturePython — macro-defined, semantics opaque (R4)
  Cascade = false
  Disabled = false
  Group = -> [ElementLink065,ElementLink066]
  Multiply = false
  _ConstraintType = 45
  _LinkVersion = 1
  _Parent = -> Constraints001
FEATURE [App::FeaturePython] ElementLink065  label="_Element020"  # link proxy (typed FeaturePython)
  LinkTransform = true
  LinkedObject = -> _Element020
  Placement = pos=(-2.84e-14,1.42e-14,0) rot=(0,0,1;0rad)
  _LinkVersion = 1
  _Parent = -> Constraint035
FEATURE [Part::FeaturePython] _Element020  # link proxy (typed FeaturePython)
  Detach = false
  LinkTransform = true
  LinkedObject = -> Link026 [Link026_i9.1.$mate.]
  _LinkVersion = 1
  _Parent = -> Elements001
FEATURE [App::FeaturePython] ElementLink066  label="_Element021"  # link proxy (typed FeaturePython)
  LinkTransform = true
  LinkedObject = -> _Element021
  _LinkVersion = 1
  _Parent = -> Constraint035
FEATURE [Part::FeaturePython] _Element021  # link proxy (typed FeaturePython)
  Detach = false
  LinkTransform = true
  LinkedObject = -> Link [Sketch009.Edge6]
  _LinkVersion = 1
  _Parent = -> Elements001
FEATURE [App::FeaturePython] Constraint036  label="Attachment011"  # WARN: FeaturePython — macro-defined, semantics opaque (R4)
  Cascade = false
  Disabled = false
  Group = -> [ElementLink067,ElementLink068]
  Multiply = false
  _ConstraintType = 45
  _LinkVersion = 1
  _Parent = -> Constraints001
FEATURE [App::FeaturePython] ElementLink067  label="_Element022"  # link proxy (typed FeaturePython)
  LinkTransform = true
  LinkedObject = -> _Element022
  Placement = pos=(-3.2e-14,-1.42e-14,7.1e-15) rot=(0,0,1;0rad)
  _LinkVersion = 1
  _Parent = -> Constraint036
FEATURE [Part::FeaturePython] _Element022  # link proxy (typed FeaturePython)
  Detach = false
  LinkTransform = true
  LinkedObject = -> Link026 [Link026_i10.1.$mate.]
  _LinkVersion = 1
  _Parent = -> Elements001
FEATURE [App::FeaturePython] ElementLink068  label="_Element023"  # link proxy (typed FeaturePython)
  LinkTransform = true
  LinkedObject = -> _Element023
  _LinkVersion = 1
  _Parent = -> Constraint036
FEATURE [Part::FeaturePython] _Element023  # link proxy (typed FeaturePython)
  Detach = false
  LinkTransform = true
  LinkedObject = -> Link [Sketch009.Edge8]
  _LinkVersion = 1
  _Parent = -> Elements001
FEATURE [App::FeaturePython] Constraint037  label="Attachment012"  # WARN: FeaturePython — macro-defined, semantics opaque (R4)
  Cascade = false
  Disabled = false
  Group = -> [ElementLink069,ElementLink070]
  Multiply = false
  _ConstraintType = 45
  _LinkVersion = 1
  _Parent = -> Constraints001
FEATURE [App::FeaturePython] ElementLink069  label="_Element024"  # link proxy (typed FeaturePython)
  LinkTransform = true
  LinkedObject = -> _Element024
  Placement = pos=(-3.91e-14,0,0) rot=(0,0,1;0rad)
  _LinkVersion = 1
  _Parent = -> Constraint037
FEATURE [Part::FeaturePython] _Element024  # link proxy (typed FeaturePython)
  Detach = false
  LinkTransform = true
  LinkedObject = -> Link026 [Link026_i11.1.$mate.]
  _LinkVersion = 1
  _Parent = -> Elements001
FEATURE [App::FeaturePython] ElementLink070  label="_Element025"  # link proxy (typed FeaturePython)
  LinkTransform = true
  LinkedObject = -> _Element025
  _LinkVersion = 1
  _Parent = -> Constraint037
FEATURE [Part::FeaturePython] _Element025  # link proxy (typed FeaturePython)
  Detach = false
  LinkTransform = true
  LinkedObject = -> Link [Sketch009.Edge7]
  _LinkVersion = 1
  _Parent = -> Elements001
FEATURE [App::FeaturePython] Constraint038  label="Attachment013"  # WARN: FeaturePython — macro-defined, semantics opaque (R4)
  Cascade = false
  Disabled = false
  Group = -> [ElementLink071,ElementLink072]
  Multiply = false
  _ConstraintType = 45
  _LinkVersion = 1
  _Parent = -> Constraints001
FEATURE [App::FeaturePython] ElementLink071  label="_Element026"  # link proxy (typed FeaturePython)
  LinkTransform = true
  LinkedObject = -> _Element026
  Placement = pos=(-9.59e-14,-5.68e-14,1.8e-15) rot=(0,0,1;0rad)
  _LinkVersion = 1
  _Parent = -> Constraint038
FEATURE [Part::FeaturePython] _Element026  # link proxy (typed FeaturePython)
  Detach = false
  LinkTransform = true
  LinkedObject = -> Link026 [Link026_i12.1.$mate.]
  _LinkVersion = 1
  _Parent = -> Elements001
FEATURE [App::FeaturePython] ElementLink072  label="_Element027"  # link proxy (typed FeaturePython)
  LinkTransform = true
  LinkedObject = -> _Element027
  _LinkVersion = 1
  _Parent = -> Constraint038
FEATURE [Part::FeaturePython] _Element027  # link proxy (typed FeaturePython)
  Detach = false
  LinkTransform = true
  LinkedObject = -> Link [Sketch009.Edge2]
  _LinkVersion = 1
  _Parent = -> Elements001
FEATURE [App::FeaturePython] Constraint039  label="Attachment014"  # WARN: FeaturePython — macro-defined, semantics opaque (R4)
  Cascade = false
  Disabled = false
  Group = -> [ElementLink073,ElementLink074]
  Multiply = false
  _ConstraintType = 45
  _LinkVersion = 1
  _Parent = -> Constraints001
FEATURE [App::FeaturePython] ElementLink073  label="_Element028"  # link proxy (typed FeaturePython)
  LinkTransform = true
  LinkedObject = -> _Element028
  Placement = pos=(-9.95e-14,0,1.8e-15) rot=(0,0,1;0rad)
  _LinkVersion = 1
  _Parent = -> Constraint039
FEATURE [Part::FeaturePython] _Element028  # link proxy (typed FeaturePython)
  Detach = false
  LinkTransform = true
  LinkedObject = -> Link026 [Link026_i13.1.$mate.]
  _LinkVersion = 1
  _Parent = -> Elements001
FEATURE [App::FeaturePython] ElementLink074  label="_Element029"  # link proxy (typed FeaturePython)
  LinkTransform = true
  LinkedObject = -> _Element029
  _LinkVersion = 1
  _Parent = -> Constraint039
FEATURE [Part::FeaturePython] _Element029  # link proxy (typed FeaturePython)
  Detach = false
  LinkTransform = true
  LinkedObject = -> Link [Sketch009.Edge1]
  _LinkVersion = 1
  _Parent = -> Elements001
FEATURE [App::FeaturePython] Constraint040  label="Attachment015"  # WARN: FeaturePython — macro-defined, semantics opaque (R4)
  Cascade = false
  Disabled = false
  Group = -> [ElementLink075,ElementLink076]
  Multiply = false
  _ConstraintType = 45
  _LinkVersion = 1
  _Parent = -> Constraints001
FEATURE [App::FeaturePython] ElementLink075  label="_Element030"  # link proxy (typed FeaturePython)
  LinkTransform = true
  LinkedObject = -> _Element030
  Placement = pos=(-9.59e-14,-5.68e-14,0) rot=(0,0,1;0rad)
  _LinkVersion = 1
  _Parent = -> Constraint040
FEATURE [Part::FeaturePython] _Element030  # link proxy (typed FeaturePython)
  Detach = false
  LinkTransform = true
  LinkedObject = -> Link026 [Link026_i14.1.$mate.]
  _LinkVersion = 1
  _Parent = -> Elements001
FEATURE [App::FeaturePython] ElementLink076  label="_Element031"  # link proxy (typed FeaturePython)
  LinkTransform = true
  LinkedObject = -> _Element031
  _LinkVersion = 1
  _Parent = -> Constraint040
FEATURE [Part::FeaturePython] _Element031  # link proxy (typed FeaturePython)
  Detach = false
  LinkTransform = true
  LinkedObject = -> Link [Sketch009.Edge4]
  _LinkVersion = 1
  _Parent = -> Elements001
FEATURE [App::FeaturePython] Constraint041  label="Attachment016"  # WARN: FeaturePython — macro-defined, semantics opaque (R4)
  Cascade = false
  Disabled = false
  Group = -> [ElementLink077,ElementLink078]
  Multiply = false
  _ConstraintType = 45
  _LinkVersion = 1
  _Parent = -> Constraints001
FEATURE [App::FeaturePython] ElementLink077  label="_Element032"  # link proxy (typed FeaturePython)
  LinkTransform = true
  LinkedObject = -> _Element032
  Placement = pos=(-1.03e-13,0,-7.1e-15) rot=(0,0,1;0rad)
  _LinkVersion = 1
  _Parent = -> Constraint041
FEATURE [Part::FeaturePython] _Element032  # link proxy (typed FeaturePython)
  Detach = false
  LinkTransform = true
  LinkedObject = -> Link026 [Link026_i15.1.$mate.]
  _LinkVersion = 1
  _Parent = -> Elements001
FEATURE [App::FeaturePython] ElementLink078  label="_Element033"  # link proxy (typed FeaturePython)
  LinkTransform = true
  LinkedObject = -> _Element033
  _LinkVersion = 1
  _Parent = -> Constraint041
FEATURE [Part::FeaturePython] _Element033  # link proxy (typed FeaturePython)
  Detach = false
  LinkTransform = true
  LinkedObject = -> Link [Sketch009.Edge3]
  _LinkVersion = 1
  _Parent = -> Elements001
FEATURE [App::FeaturePython] Constraint042  label="Attachment017"  # WARN: FeaturePython — macro-defined, semantics opaque (R4)
  Cascade = false
  Disabled = false
  Group = -> [ElementLink079,ElementLink080]
  Multiply = false
  _ConstraintType = 45
  _LinkVersion = 1
  _Parent = -> Constraints003
FEATURE [App::FeaturePython] ElementLink079  label="_Element034"  # link proxy (typed FeaturePython)
  LinkTransform = true
  LinkedObject = -> _Element034
  _LinkVersion = 1
  _Parent = -> Constraint042
FEATURE [Part::FeaturePython] _Element034  # link proxy (typed FeaturePython)
  Detach = false
  LinkTransform = true
  LinkedObject = -> Link027 [Link027_i15.1.$mate.]
  _LinkVersion = 1
  _Parent = -> Elements003
FEATURE [App::FeaturePython] ElementLink080  label="_Element035"  # link proxy (typed FeaturePython)
  LinkTransform = true
  LinkedObject = -> _Element035
  _LinkVersion = 1
  _Parent = -> Constraint042
FEATURE [Part::FeaturePython] _Element035  # link proxy (typed FeaturePython)
  Detach = false
  LinkTransform = true
  LinkedObject = -> Link008 [Sketch009.Edge13]
  _LinkVersion = 1
  _Parent = -> Elements003
FEATURE [App::FeaturePython] Constraint043  label="Attachment018"  # WARN: FeaturePython — macro-defined, semantics opaque (R4)
  Cascade = false
  Disabled = false
  Group = -> [ElementLink081,ElementLink082]
  Multiply = false
  _ConstraintType = 45
  _LinkVersion = 1
  _Parent = -> Constraints003
FEATURE [App::FeaturePython] ElementLink081  label="_Element036"  # link proxy (typed FeaturePython)
  LinkTransform = true
  LinkedObject = -> _Element036
  _LinkVersion = 1
  _Parent = -> Constraint043
FEATURE [Part::FeaturePython] _Element036  # link proxy (typed FeaturePython)
  Detach = false
  LinkTransform = true
  LinkedObject = -> Link027 [Link027_i14.1.$mate.]
  _LinkVersion = 1
  _Parent = -> Elements003
FEATURE [App::FeaturePython] ElementLink082  label="_Element037"  # link proxy (typed FeaturePython)
  LinkTransform = true
  LinkedObject = -> _Element037
  _LinkVersion = 1
  _Parent = -> Constraint043
FEATURE [Part::FeaturePython] _Element037  # link proxy (typed FeaturePython)
  Detach = false
  LinkTransform = true
  LinkedObject = -> Link008 [Sketch009.Edge15]
  _LinkVersion = 1
  _Parent = -> Elements003
FEATURE [App::FeaturePython] Constraint044  label="Attachment019"  # WARN: FeaturePython — macro-defined, semantics opaque (R4)
  Cascade = false
  Disabled = false
  Group = -> [ElementLink083,ElementLink084]
  Multiply = false
  _ConstraintType = 45
  _LinkVersion = 1
  _Parent = -> Constraints003
FEATURE [App::FeaturePython] ElementLink083  label="_Element038"  # link proxy (typed FeaturePython)
  LinkTransform = true
  LinkedObject = -> _Element038
  _LinkVersion = 1
  _Parent = -> Constraint044
FEATURE [Part::FeaturePython] _Element038  # link proxy (typed FeaturePython)
  Detach = false
  LinkTransform = true
  LinkedObject = -> Link027 [Link027_i13.1.$mate.]
  _LinkVersion = 1
  _Parent = -> Elements003
FEATURE [App::FeaturePython] ElementLink084  label="_Element039"  # link proxy (typed FeaturePython)
  LinkTransform = true
  LinkedObject = -> _Element039
  _LinkVersion = 1
  _Parent = -> Constraint044
FEATURE [Part::FeaturePython] _Element039  # link proxy (typed FeaturePython)
  Detach = false
  LinkTransform = true
  LinkedObject = -> Link008 [Sketch009.Edge14]
  _LinkVersion = 1
  _Parent = -> Elements003
FEATURE [App::FeaturePython] Constraint045  label="Attachment020"  # WARN: FeaturePython — macro-defined, semantics opaque (R4)
  Cascade = false
  Disabled = false
  Group = -> [ElementLink085,ElementLink086]
  Multiply = false
  _ConstraintType = 45
  _LinkVersion = 1
  _Parent = -> Constraints003
FEATURE [App::FeaturePython] ElementLink085  label="_Element040"  # link proxy (typed FeaturePython)
  LinkTransform = true
  LinkedObject = -> _Element040
  _LinkVersion = 1
  _Parent = -> Constraint045
FEATURE [Part::FeaturePython] _Element040  # link proxy (typed FeaturePython)
  Detach = false
  LinkTransform = true
  LinkedObject = -> Link027 [Link027_i12.1.$mate.]
  _LinkVersion = 1
  _Parent = -> Elements003
FEATURE [App::FeaturePython] ElementLink086  label="_Element041"  # link proxy (typed FeaturePython)
  LinkTransform = true
  LinkedObject = -> _Element041
  _LinkVersion = 1
  _Parent = -> Constraint045
FEATURE [Part::FeaturePython] _Element041  # link proxy (typed FeaturePython)
  Detach = false
  LinkTransform = true
  LinkedObject = -> Link008 [Sketch009.Edge16]
  _LinkVersion = 1
  _Parent = -> Elements003
FEATURE [App::FeaturePython] Constraint046  label="Attachment021"  # WARN: FeaturePython — macro-defined, semantics opaque (R4)
  Cascade = false
  Disabled = false
  Group = -> [ElementLink087,ElementLink088]
  Multiply = false
  _ConstraintType = 45
  _LinkVersion = 1
  _Parent = -> Constraints003
FEATURE [App::FeaturePython] ElementLink087  label="_Element042"  # link proxy (typed FeaturePython)
  LinkTransform = true
  LinkedObject = -> _Element042
  _LinkVersion = 1
  _Parent = -> Constraint046
FEATURE [Part::FeaturePython] _Element042  # link proxy (typed FeaturePython)
  Detach = false
  LinkTransform = true
  LinkedObject = -> Link027 [Link027_i11.1.$mate.]
  _LinkVersion = 1
  _Parent = -> Elements003
FEATURE [App::FeaturePython] ElementLink088  label="_Element043"  # link proxy (typed FeaturePython)
  LinkTransform = true
  LinkedObject = -> _Element043
  _LinkVersion = 1
  _Parent = -> Constraint046
FEATURE [Part::FeaturePython] _Element043  # link proxy (typed FeaturePython)
  Detach = false
  LinkTransform = true
  LinkedObject = -> Link008 [Sketch009.Edge12]
  _LinkVersion = 1
  _Parent = -> Elements003
FEATURE [App::FeaturePython] Constraint047  label="Attachment022"  # WARN: FeaturePython — macro-defined, semantics opaque (R4)
  Cascade = false
  Disabled = false
  Group = -> [ElementLink089,ElementLink090]
  Multiply = false
  _ConstraintType = 45
  _LinkVersion = 1
  _Parent = -> Constraints003
FEATURE [App::FeaturePython] ElementLink089  label="_Element044"  # link proxy (typed FeaturePython)
  LinkTransform = true
  LinkedObject = -> _Element044
  _LinkVersion = 1
  _Parent = -> Constraint047
FEATURE [Part::FeaturePython] _Element044  # link proxy (typed FeaturePython)
  Detach = false
  LinkTransform = true
  LinkedObject = -> Link027 [Link027_i10.1.$mate.]
  _LinkVersion = 1
  _Parent = -> Elements003
FEATURE [App::FeaturePython] ElementLink090  label="_Element045"  # link proxy (typed FeaturePython)
  LinkTransform = true
  LinkedObject = -> _Element045
  _LinkVersion = 1
  _Parent = -> Constraint047
FEATURE [Part::FeaturePython] _Element045  # link proxy (typed FeaturePython)
  Detach = false
  LinkTransform = true
  LinkedObject = -> Link008 [Sketch009.Edge10]
  _LinkVersion = 1
  _Parent = -> Elements003
FEATURE [App::FeaturePython] Constraint048  label="Attachment023"  # WARN: FeaturePython — macro-defined, semantics opaque (R4)
  Cascade = false
  Disabled = false
  Group = -> [ElementLink091,ElementLink092]
  Multiply = false
  _ConstraintType = 45
  _LinkVersion = 1
  _Parent = -> Constraints003
FEATURE [App::FeaturePython] ElementLink091  label="_Element046"  # link proxy (typed FeaturePython)
  LinkTransform = true
  LinkedObject = -> _Element046
  _LinkVersion = 1
  _Parent = -> Constraint048
FEATURE [Part::FeaturePython] _Element046  # link proxy (typed FeaturePython)
  Detach = false
  LinkTransform = true
  LinkedObject = -> Link027 [Link027_i9.1.$mate.]
  _LinkVersion = 1
  _Parent = -> Elements003
FEATURE [App::FeaturePython] ElementLink092  label="_Element047"  # link proxy (typed FeaturePython)
  LinkTransform = true
  LinkedObject = -> _Element047
  _LinkVersion = 1
  _Parent = -> Constraint048
FEATURE [Part::FeaturePython] _Element047  # link proxy (typed FeaturePython)
  Detach = false
  LinkTransform = true
  LinkedObject = -> Link008 [Sketch009.Edge11]
  _LinkVersion = 1
  _Parent = -> Elements003
FEATURE [App::FeaturePython] Constraint049  label="Attachment024"  # WARN: FeaturePython — macro-defined, semantics opaque (R4)
  Cascade = false
  Disabled = false
  Group = -> [ElementLink093,ElementLink094]
  Multiply = false
  _ConstraintType = 45
  _LinkVersion = 1
  _Parent = -> Constraints003
FEATURE [App::FeaturePython] ElementLink093  label="_Element048"  # link proxy (typed FeaturePython)
  LinkTransform = true
  LinkedObject = -> _Element048
  _LinkVersion = 1
  _Parent = -> Constraint049
FEATURE [Part::FeaturePython] _Element048  # link proxy (typed FeaturePython)
  Detach = false
  LinkTransform = true
  LinkedObject = -> Link027 [Link027_i8.1.$mate.]
  _LinkVersion = 1
  _Parent = -> Elements003
FEATURE [App::FeaturePython] ElementLink094  label="_Element049"  # link proxy (typed FeaturePython)
  LinkTransform = true
  LinkedObject = -> _Element049
  _LinkVersion = 1
  _Parent = -> Constraint049
FEATURE [Part::FeaturePython] _Element049  # link proxy (typed FeaturePython)
  Detach = false
  LinkTransform = true
  LinkedObject = -> Link008 [Sketch009.Edge9]
  _LinkVersion = 1
  _Parent = -> Elements003
FEATURE [App::FeaturePython] Constraint050  label="Attachment025"  # WARN: FeaturePython — macro-defined, semantics opaque (R4)
  Cascade = false
  Disabled = false
  Group = -> [ElementLink095,ElementLink096]
  Multiply = false
  _ConstraintType = 45
  _LinkVersion = 1
  _Parent = -> Constraints003
FEATURE [App::FeaturePython] ElementLink095  label="_Element050"  # link proxy (typed FeaturePython)
  LinkTransform = true
  LinkedObject = -> _Element050
  _LinkVersion = 1
  _Parent = -> Constraint050
FEATURE [Part::FeaturePython] _Element050  # link proxy (typed FeaturePython)
  Detach = false
  LinkTransform = true
  LinkedObject = -> Link027 [Link027_i7.1.$mate.]
  _LinkVersion = 1
  _Parent = -> Elements003
FEATURE [App::FeaturePython] ElementLink096  label="_Element051"  # link proxy (typed FeaturePython)
  LinkTransform = true
  LinkedObject = -> _Element051
  _LinkVersion = 1
  _Parent = -> Constraint050
FEATURE [Part::FeaturePython] _Element051  # link proxy (typed FeaturePython)
  Detach = false
  LinkTransform = true
  LinkedObject = -> Link008 [Sketch009.Edge6]
  _LinkVersion = 1
  _Parent = -> Elements003
FEATURE [App::FeaturePython] Constraint051  label="Attachment026"  # WARN: FeaturePython — macro-defined, semantics opaque (R4)
  Cascade = false
  Disabled = false
  Group = -> [ElementLink097,ElementLink098]
  Multiply = false
  _ConstraintType = 45
  _LinkVersion = 1
  _Parent = -> Constraints003
FEATURE [App::FeaturePython] ElementLink097  label="_Element052"  # link proxy (typed FeaturePython)
  LinkTransform = true
  LinkedObject = -> _Element052
  _LinkVersion = 1
  _Parent = -> Constraint051
FEATURE [Part::FeaturePython] _Element052  # link proxy (typed FeaturePython)
  Detach = false
  LinkTransform = true
  LinkedObject = -> Link027 [Link027_i6.1.$mate.]
  _LinkVersion = 1
  _Parent = -> Elements003
FEATURE [App::FeaturePython] ElementLink098  label="_Element053"  # link proxy (typed FeaturePython)
  LinkTransform = true
  LinkedObject = -> _Element053
  _LinkVersion = 1
  _Parent = -> Constraint051
FEATURE [Part::FeaturePython] _Element053  # link proxy (typed FeaturePython)
  Detach = false
  LinkTransform = true
  LinkedObject = -> Link008 [Sketch009.Edge5]
  _LinkVersion = 1
  _Parent = -> Elements003
FEATURE [App::FeaturePython] Constraint052  label="Attachment027"  # WARN: FeaturePython — macro-defined, semantics opaque (R4)
  Cascade = false
  Disabled = false
  Group = -> [ElementLink099,ElementLink100]
  Multiply = false
  _ConstraintType = 45
  _LinkVersion = 1
  _Parent = -> Constraints003
FEATURE [App::FeaturePython] ElementLink099  label="_Element054"  # link proxy (typed FeaturePython)
  LinkTransform = true
  LinkedObject = -> _Element054
  _LinkVersion = 1
  _Parent = -> Constraint052
FEATURE [Part::FeaturePython] _Element054  # link proxy (typed FeaturePython)
  Detach = false
  LinkTransform = true
  LinkedObject = -> Link027 [Link027_i5.1.$mate.]
  _LinkVersion = 1
  _Parent = -> Elements003
FEATURE [App::FeaturePython] ElementLink100  label="_Element055"  # link proxy (typed FeaturePython)
  LinkTransform = true
  LinkedObject = -> _Element055
  _LinkVersion = 1
  _Parent = -> Constraint052
FEATURE [Part::FeaturePython] _Element055  # link proxy (typed FeaturePython)
  Detach = false
  LinkTransform = true
  LinkedObject = -> Link008 [Sketch009.Edge8]
  _LinkVersion = 1
  _Parent = -> Elements003
FEATURE [App::FeaturePython] Constraint053  label="Attachment028"  # WARN: FeaturePython — macro-defined, semantics opaque (R4)
  Cascade = false
  Disabled = false
  Group = -> [ElementLink101,ElementLink102]
  Multiply = false
  _ConstraintType = 45
  _LinkVersion = 1
  _Parent = -> Constraints003
FEATURE [App::FeaturePython] ElementLink101  label="_Element056"  # link proxy (typed FeaturePython)
  LinkTransform = true
  LinkedObject = -> _Element056
  _LinkVersion = 1
  _Parent = -> Constraint053
FEATURE [Part::FeaturePython] _Element056  # link proxy (typed FeaturePython)
  Detach = false
  LinkTransform = true
  LinkedObject = -> Link027 [Link027_i4.1.$mate.]
  _LinkVersion = 1
  _Parent = -> Elements003
FEATURE [App::FeaturePython] ElementLink102  label="_Element057"  # link proxy (typed FeaturePython)
  LinkTransform = true
  LinkedObject = -> _Element057
  _LinkVersion = 1
  _Parent = -> Constraint053
FEATURE [Part::FeaturePython] _Element057  # link proxy (typed FeaturePython)
  Detach = false
  LinkTransform = true
  LinkedObject = -> Link008 [Sketch009.Edge7]
  _LinkVersion = 1
  _Parent = -> Elements003
FEATURE [App::FeaturePython] Constraint054  label="Attachment029"  # WARN: FeaturePython — macro-defined, semantics opaque (R4)
  Cascade = false
  Disabled = false
  Group = -> [ElementLink103,ElementLink104]
  Multiply = false
  _ConstraintType = 45
  _LinkVersion = 1
  _Parent = -> Constraints003
FEATURE [App::FeaturePython] ElementLink103  label="_Element058"  # link proxy (typed FeaturePython)
  LinkTransform = true
  LinkedObject = -> _Element058
  _LinkVersion = 1
  _Parent = -> Constraint054
FEATURE [Part::FeaturePython] _Element058  # link proxy (typed FeaturePython)
  Detach = false
  LinkTransform = true
  LinkedObject = -> Link027 [Link027_i3.1.$mate.]
  _LinkVersion = 1
  _Parent = -> Elements003
FEATURE [App::FeaturePython] ElementLink104  label="_Element059"  # link proxy (typed FeaturePython)
  LinkTransform = true
  LinkedObject = -> _Element059
  _LinkVersion = 1
  _Parent = -> Constraint054
FEATURE [Part::FeaturePython] _Element059  # link proxy (typed FeaturePython)
  Detach = false
  LinkTransform = true
  LinkedObject = -> Link008 [Sketch009.Edge2]
  _LinkVersion = 1
  _Parent = -> Elements003
FEATURE [App::FeaturePython] Constraint055  label="Attachment030"  # WARN: FeaturePython — macro-defined, semantics opaque (R4)
  Cascade = false
  Disabled = false
  Group = -> [ElementLink105,ElementLink106]
  Multiply = false
  _ConstraintType = 45
  _LinkVersion = 1
  _Parent = -> Constraints003
FEATURE [App::FeaturePython] ElementLink105  label="_Element060"  # link proxy (typed FeaturePython)
  LinkTransform = true
  LinkedObject = -> _Element060
  _LinkVersion = 1
  _Parent = -> Constraint055
FEATURE [Part::FeaturePython] _Element060  # link proxy (typed FeaturePython)
  Detach = false
  LinkTransform = true
  LinkedObject = -> Link027 [Link027_i2.1.$mate.]
  _LinkVersion = 1
  _Parent = -> Elements003
FEATURE [App::FeaturePython] ElementLink106  label="_Element061"  # link proxy (typed FeaturePython)
  LinkTransform = true
  LinkedObject = -> _Element061
  _LinkVersion = 1
  _Parent = -> Constraint055
FEATURE [Part::FeaturePython] _Element061  # link proxy (typed FeaturePython)
  Detach = false
  LinkTransform = true
  LinkedObject = -> Link008 [Sketch009.Edge1]
  _LinkVersion = 1
  _Parent = -> Elements003
FEATURE [App::FeaturePython] Constraint056  label="Attachment031"  # WARN: FeaturePython — macro-defined, semantics opaque (R4)
  Cascade = false
  Disabled = false
  Group = -> [ElementLink107,ElementLink108]
  Multiply = false
  _ConstraintType = 45
  _LinkVersion = 1
  _Parent = -> Constraints003
FEATURE [App::FeaturePython] ElementLink107  label="_Element062"  # link proxy (typed FeaturePython)
  LinkTransform = true
  LinkedObject = -> _Element062
  _LinkVersion = 1
  _Parent = -> Constraint056
FEATURE [Part::FeaturePython] _Element062  # link proxy (typed FeaturePython)
  Detach = false
  LinkTransform = true
  LinkedObject = -> Link027 [Link027_i1.1.$mate.]
  _LinkVersion = 1
  _Parent = -> Elements003
FEATURE [App::FeaturePython] ElementLink108  label="_Element063"  # link proxy (typed FeaturePython)
  LinkTransform = true
  LinkedObject = -> _Element063
  _LinkVersion = 1
  _Parent = -> Constraint056
FEATURE [Part::FeaturePython] _Element063  # link proxy (typed FeaturePython)
  Detach = false
  LinkTransform = true
  LinkedObject = -> Link008 [Sketch009.Edge4]
  _LinkVersion = 1
  _Parent = -> Elements003
FEATURE [App::FeaturePython] Constraint057  label="Attachment032"  # WARN: FeaturePython — macro-defined, semantics opaque (R4)
  Cascade = false
  Disabled = false
  Group = -> [ElementLink109,ElementLink110]
  Multiply = false
  _ConstraintType = 45
  _LinkVersion = 1
  _Parent = -> Constraints003
FEATURE [App::FeaturePython] ElementLink109  label="_Element064"  # link proxy (typed FeaturePython)
  LinkTransform = true
  LinkedObject = -> _Element064
  _LinkVersion = 1
  _Parent = -> Constraint057
FEATURE [Part::FeaturePython] _Element064  # link proxy (typed FeaturePython)
  Detach = false
  LinkTransform = true
  LinkedObject = -> Link027 [Link027_i0.1.$mate.]
  _LinkVersion = 1
  _Parent = -> Elements003
FEATURE [App::FeaturePython] ElementLink110  label="_Element065"  # link proxy (typed FeaturePython)
  LinkTransform = true
  LinkedObject = -> _Element065
  _LinkVersion = 1
  _Parent = -> Constraint057
FEATURE [Part::FeaturePython] _Element065  # link proxy (typed FeaturePython)
  Detach = false
  LinkTransform = true
  LinkedObject = -> Link008 [Sketch009.Edge3]
  _LinkVersion = 1
  _Parent = -> Elements003
FEATURE [Part::FeaturePython] Element066  label="beam mate@Front plate Assembly L"  # link proxy (typed FeaturePython)
  Detach = false
  LinkTransform = true
  LinkedObject = -> Link028 [1.$beam mate.]
  _LinkVersion = 1
  _Parent = -> Elements
FEATURE [Part::FeaturePython] Element067  label="beam mate@Front plate Assemply R"  # link proxy (typed FeaturePython)
  Detach = false
  LinkTransform = true
  LinkedObject = -> Link029 [1.$beam mate.]
  _LinkVersion = 1
  _Parent = -> Elements
FEATURE [App::FeaturePython] Constraint058  label="Attachment-front-left"  # WARN: FeaturePython — macro-defined, semantics opaque (R4)
  Cascade = false
  Disabled = false
  Group = -> [ElementLink111,ElementLink112]
  Multiply = false
  _ConstraintType = 45
  _LinkVersion = 1
  _Parent = -> Constraints
FEATURE [App::FeaturePython] ElementLink111  label="beam mate@Front plate Assembly L"  # link proxy (typed FeaturePython)
  LinkTransform = true
  LinkedObject = -> Element066
  _LinkVersion = 1
  _Parent = -> Constraint058
FEATURE [App::FeaturePython] ElementLink112  label="front-mate@Left beam Assembly"  # link proxy (typed FeaturePython)
  LinkTransform = true
  LinkedObject = -> _Element066
  _LinkVersion = 1
  _Parent = -> Constraint058
FEATURE [Part::FeaturePython] Element068  # link proxy (typed FeaturePython)
  Detach = false
  LinkTransform = true
  LinkedObject = -> Link [Pocket005.Edge303]
  _LinkVersion = 1
  _Parent = -> Elements001
FEATURE [Part::FeaturePython] _Element066  label="front-mate@Left beam Assembly"  # link proxy (typed FeaturePython)
  Detach = false
  LinkTransform = true
  LinkedObject = -> Link009 [1.$Element068.]
  _LinkVersion = 1
  _Parent = -> Elements
FEATURE [App::FeaturePython] Constraint059  label="Attachment-front-right"  # WARN: FeaturePython — macro-defined, semantics opaque (R4)
  Cascade = false
  Disabled = false
  Group = -> [ElementLink113,ElementLink114]
  Multiply = false
  _ConstraintType = 45
  _LinkVersion = 1
  _Parent = -> Constraints
FEATURE [App::FeaturePython] ElementLink113  label="beam mate@Front plate Assemply R"  # link proxy (typed FeaturePython)
  LinkTransform = true
  LinkedObject = -> Element067
  _LinkVersion = 1
  _Parent = -> Constraint059
FEATURE [App::FeaturePython] ElementLink114  label="front-mate@Right beam Assembly"  # link proxy (typed FeaturePython)
  LinkTransform = true
  LinkedObject = -> _Element067
  _LinkVersion = 1
  _Parent = -> Constraint059
FEATURE [Part::FeaturePython] Element069  # link proxy (typed FeaturePython)
  Detach = false
  LinkTransform = true
  LinkedObject = -> Link008 [Pocket005.Edge596]
  _LinkVersion = 1
  _Parent = -> Elements003
FEATURE [Part::FeaturePython] _Element067  label="front-mate@Right beam Assembly"  # link proxy (typed FeaturePython)
  Detach = false
  LinkTransform = true
  LinkedObject = -> Link010 [1.$Element069.]
  _LinkVersion = 1
  _Parent = -> Elements
FEATURE [Part::FeaturePython] Element070  label="limit mate@Motor plate R Assembly"  # link proxy (typed FeaturePython)
  Detach = false
  LinkTransform = true
  LinkedObject = -> Link023 [1.$limit mate.]
  _LinkVersion = 1
  _Parent = -> Elements
FEATURE [Part::FeaturePython] Element071  label="mate r@Limit sensor Assembly"  # link proxy (typed FeaturePython)
  Detach = false
  LinkTransform = true
  LinkedObject = -> Link030 [1.$mate r.]
  _LinkVersion = 1
  _Parent = -> Elements
FEATURE [App::FeaturePython] Constraint060  label="Attachment-limit-sensor-right"  # WARN: FeaturePython — macro-defined, semantics opaque (R4)
  Cascade = false
  Disabled = false
  Group = -> [ElementLink115,ElementLink116]
  Multiply = false
  _ConstraintType = 45
  _LinkVersion = 1
  _Parent = -> Constraints
FEATURE [App::FeaturePython] ElementLink115  label="mate r@Limit sensor Assembly"  # link proxy (typed FeaturePython)
  LinkTransform = true
  LinkedObject = -> Element071
  Offset = pos=(0,0,0) rot=(1,0,0;3.14159rad)
  Placement = pos=(1090.8,830,-4.8885e-12) rot=(0,0,1;3.14159rad)
  _LinkVersion = 1
  _Parent = -> Constraint060
FEATURE [App::FeaturePython] ElementLink116  label="limit mate@Motor plate R Assembly"  # link proxy (typed FeaturePython)
  LinkTransform = true
  LinkedObject = -> Element070
  Offset = pos=(0,0,0) rot=(0,0,1;4.71239rad)
  Placement = pos=(501.3,1.56861e-06,589.5) rot=(0,1,0;1.5708rad)
  _LinkVersion = 1
  _Parent = -> Constraint060
FEATURE [Part::FeaturePython] Element072  label="limit mate@Motor plate L Assembly"  # link proxy (typed FeaturePython)
  Detach = false
  LinkTransform = true
  LinkedObject = -> Link024 [1.$limit mate.]
  _LinkVersion = 1
  _Parent = -> Elements
FEATURE [Part::FeaturePython] Element073  label="mate l@Limit sensor Assembly"  # link proxy (typed FeaturePython)
  Detach = false
  LinkTransform = true
  LinkedObject = -> Link031 [1.$mate l.]
  _LinkVersion = 1
  _Parent = -> Elements
FEATURE [App::FeaturePython] Constraint061  label="Attachment-limit-sensor-left"  # WARN: FeaturePython — macro-defined, semantics opaque (R4)
  Cascade = false
  Disabled = false
  Group = -> [ElementLink117,ElementLink118]
  Multiply = false
  _ConstraintType = 45
  _LinkVersion = 1
  _Parent = -> Constraints
FEATURE [App::FeaturePython] ElementLink117  label="mate l@Limit sensor Assembly"  # link proxy (typed FeaturePython)
  LinkTransform = true
  LinkedObject = -> Element073
  _LinkVersion = 1
  _Parent = -> Constraint061
FEATURE [App::FeaturePython] ElementLink118  label="limit mate@Motor plate L Assembly"  # link proxy (typed FeaturePython)
  LinkTransform = true
  LinkedObject = -> Element072
  Offset = pos=(0,0,0) rot=(0,0,1;1.5708rad)
  Placement = pos=(-90.7,5.68e-14,-2.5) rot=(0,1,0;1.5708rad)
  _LinkVersion = 1
  _Parent = -> Constraint061

RESOLVED EXTERNAL PARTS (link-assembly join: the EXTERNAL_REF files above that resolve inside this repo's crawl, each included once):
---- part parts/Ballscrew.FCStd = doc fcstd_904fc7d7aa5a (101767 chars; too large to inline — full recipe in that document) ----
---- part parts/Extrusion.FCStd = doc fcstd_ad510d6255d3 (60963 chars; too large to inline — full recipe in that document) ----
---- part parts/HGR20.FCStd = doc fcstd_98294569bf8e (65349 chars; too large to inline — full recipe in that document) ----
---- part parts/LimitSensor.FCStd = doc fcstd_3f7c24fee6a1 ----
FCSTD DOCUMENT  (FreeCAD 2021.717R24301 +3842 (Git))
Label: LimitSensor
License: Creative Commons Attribution
LicenseURL: http://creativecommons.org/licenses/by/4.0/
objects: App::FeaturePython×10, Part::FeaturePython×8, Sketcher::SketchObject×6, PartDesign::Pocket×4, App::Link×2, App::DocumentObjectGroup×2, App::LinkElement×2, PartDesign::Pad×1, PartDesign::Mirrored×1, PartDesign::Body×1
note: 32 computed .brp shape members not serialized (recipe doc carries the construction recipe); baked Part::Feature solids carry a one-line shape summary decoded from their .brp

FEATURE [Sketcher::SketchObject] Sketch
  FullyConstrained = true
  MapMode = 5
  Placement = pos=(0,0,0) rot=(1,0,0;1.5708rad)
  Support = -> [XZ_Plane]
  sketch-geometry (4):
    g0: LineSegment StartX=-9 StartY=15.25 StartZ=0 EndX=9 EndY=15.25 EndZ=0
    g1: LineSegment StartX=9 StartY=15.25 StartZ=0 EndX=9 EndY=-15.25 EndZ=0
    g2: LineSegment StartX=9 StartY=-15.25 StartZ=0 EndX=-9 EndY=-15.25 EndZ=0
    g3: LineSegment StartX=-9 StartY=-15.25 StartZ=0 EndX=-9 EndY=15.25 EndZ=0
  constraints (11):
    c: Coincident(g0,g1)
    c: Coincident(g1,g2)
    c: Coincident(g2,g3)
    c: Coincident(g3,g0)
    c: Horizontal(g0)
    c: Horizontal(g2)
    c: Vertical(g1)
    c: Vertical(g3)
    c: Symmetric(g1,g0,g-1)
    c: DistanceX(g0,g0) = 18
    c: DistanceY(g1,g1) = 30.5
FEATURE [PartDesign::Pad] Pad
  ClaimChildren = false
  Direction = (1,1,1)
  Fit = 0
  FitJoin = 0
  InnerFit = 0
  InnerFitJoin = 0
  InnerTaperAngle = 0
  InnerTaperAngleRev = 0
  Length = 10
  Length2 = 100
  Linearize = true
  NewSolid = false
  Placement = pos=(0,0,0) rot=(1,0,0;1.5708rad)
  Profile = -> Sketch
  Refine = true
  Suppress = false
  Type = 0
  _ProfileBasedVersion = 1
FEATURE [Sketcher::SketchObject] Sketch001
  FullyConstrained = true
  MapMode = 5
  Placement = pos=(0,-10,2.2e-15) rot=(1,0,0;1.5708rad)
  Support = -> [Pad]
  sketch-geometry (4):
    g0: LineSegment StartX=-9 StartY=15.25 StartZ=0 EndX=9 EndY=15.25 EndZ=0
    g1: LineSegment StartX=9 StartY=15.25 StartZ=0 EndX=9 EndY=7 EndZ=0
    g2: LineSegment StartX=9 StartY=7 StartZ=0 EndX=-9 EndY=7 EndZ=0
    g3: LineSegment StartX=-9 StartY=7 StartZ=0 EndX=-9 EndY=15.25 EndZ=0
  constraints (11):
    c: Coincident(g0,g1)
    c: Coincident(g1,g2)
    c: Coincident(g2,g3)
    c: Coincident(g3,g0)
    c: Horizontal(g0)
    c: Vertical(g1)
    c: Vertical(g3)
    c: Symmetric(g1,g2,g-2)
    c: DistanceX(g0,g0) = 18
    c: DistanceY(g1,g1) = 8.25
    c: DistanceY(g-1,g1) = 7
FEATURE [PartDesign::Pocket] Pocket
  BaseFeature = -> Pad
  ClaimChildren = false
  Fit = 0
  FitJoin = 0
  InnerFit = 0
  InnerFitJoin = 0
  InnerTaperAngle = 0
  InnerTaperAngleRev = 0
  Length = 2
  Length2 = 100
  Linearize = true
  NewSolid = false
  Placement = pos=(0,0,0) rot=(1,0,0;1.5708rad)
  Profile = -> Sketch001
  Refine = true
  Suppress = false
  Type = 0
  _ProfileBasedVersion = 1
FEATURE [Sketcher::SketchObject] Sketch002
  FullyConstrained = true
  MapMode = 5
  Placement = pos=(0,-8,6.9e-15) rot=(1,0,0;1.5708rad)
  Support = -> [Pocket]
  sketch-geometry (4):
    g0: ArcOfCircle CenterX=-6 CenterY=11.25 CenterZ=0 NormalX=0 NormalY=0 NormalZ=1 AngleXU=0 Radius=1.75 StartAngle=0 EndAngle=3.14159
    g1: ArcOfCircle CenterX=-6 CenterY=9.75 CenterZ=0 NormalX=0 NormalY=0 NormalZ=1 AngleXU=0 Radius=1.75 StartAngle=3.14159 EndAngle=6.28319
    g2: LineSegment StartX=-7.75 StartY=11.25 StartZ=0 EndX=-7.75 EndY=9.75 EndZ=0
    g3: LineSegment StartX=-4.25 StartY=11.25 StartZ=0 EndX=-4.25 EndY=9.75 EndZ=0
  constraints (10):
    c: Tangent(g0,g3) = 1.5708
    c: Tangent(g0,g2) = -1.5708
    c: Tangent(g2,g1) = -1.5708
    c: Tangent(g3,g1) = 1.5708
    c: Vertical(g2)
    c: Equal(g0,g1)
    c: DistanceY(g3,g3) = 1.5
    c: Diameter(g0) = 3.5
    c: DistanceY(g-1,g0) = 11.25
    c: DistanceX(g0,g-1) = 6
FEATURE [PartDesign::Pocket] Pocket001
  BaseFeature = -> Pocket
  ClaimChildren = false
  Fit = 0
  FitJoin = 0
  InnerFit = 0
  InnerFitJoin = 0
  InnerTaperAngle = 0
  InnerTaperAngleRev = 0
  Length = 5
  Length2 = 100
  Linearize = true
  NewSolid = false
  Placement = pos=(0,0,0) rot=(1,0,0;1.5708rad)
  Profile = -> Sketch002
  Refine = true
  Suppress = false
  Type = 1
  _ProfileBasedVersion = 1
FEATURE [Sketcher::SketchObject] Sketch003
  ExternalGeometry = -> [Pocket001]
  FullyConstrained = true
  MapMode = 5
  Placement = pos=(0,-8,6.9e-15) rot=(1,0,0;1.5708rad)
  Support = -> [Pocket001]
  sketch-geometry (6):
    g0: LineSegment StartX=-9 StartY=15.25 StartZ=0 EndX=-2 EndY=15.25 EndZ=0
    g1: LineSegment StartX=-2 StartY=15.25 StartZ=0 EndX=-2 EndY=9 EndZ=0
    g2: LineSegment StartX=-4 StartY=7 StartZ=0 EndX=-9 EndY=7 EndZ=0
    g3: LineSegment StartX=-9 StartY=7 StartZ=0 EndX=-9 EndY=15.25 EndZ=0
    g4: ArcOfCircle CenterX=-4 CenterY=9 CenterZ=0 NormalX=0 NormalY=0 NormalZ=1 AngleXU=0 Radius=2 StartAngle=4.71239 EndAngle=6.28319
    g5: GeomPoint [constr] X=-2 Y=7 Z=0
  constraints (16):
    c: Coincident(g0,g1)
    c: Coincident(g2,g3)
    c: Coincident(g3,g0)
    c: Horizontal(g0)
    c: Horizontal(g2)
    c: Vertical(g1)
    c: Vertical(g3)
    c: DistanceX(g2,g-1) = 9
    c: DistanceY(g-1,g0) = 15.25
    c: Horizontal(g-3,g2)
    c: DistanceX(g0,g0) = 7
    c: PointOnObject(g5,g1)
    c: PointOnObject(g5,g2)
    c: Tangent(g1,g4) = 1.5708
    c: Tangent(g2,g4) = 1.5708
    c: Radius(g4) = 2
FEATURE [PartDesign::Pocket] Pocket002
  BaseFeature = -> Pocket001
  ClaimChildren = false
  Fit = 0
  FitJoin = 0
  InnerFit = 0
  InnerFitJoin = 0
  InnerTaperAngle = 0
  InnerTaperAngleRev = 0
  Length = 1.5
  Length2 = 100
  Linearize = true
  NewSolid = false
  Placement = pos=(0,0,0) rot=(1,0,0;1.5708rad)
  Profile = -> Sketch003
  Refine = true
  Suppress = false
  Type = 0
  _ProfileBasedVersion = 1
FEATURE [PartDesign::Mirrored] Mirrored
  BaseFeature = -> Pocket002
  CopyShape = false
  MirrorPlane = -> Sketch003 [V_Axis]
  NewSolid = false
  OriginalSubs = -> [Pocket002,Pocket001]
  Originals = -> [Pocket002,Pocket001]
  ParallelTransform = true
  Placement = pos=(0,0,0) rot=(1,0,0;1.5708rad)
  Refine = true
  SubTransform = true
  Suppress = false
  _Version = 2
FEATURE [Sketcher::SketchObject] Sketch004
  FullyConstrained = false
  MapMode = 5
  Placement = pos=(0,-10,2.2e-15) rot=(1,0,0;1.5708rad)
  Support = -> [Mirrored]
  sketch-geometry (30):
    g0: LineSegment StartX=-7.75 StartY=5.75 StartZ=0 EndX=7.75 EndY=5.75 EndZ=0
    g1: LineSegment StartX=7.75 StartY=5.75 StartZ=0 EndX=7.75 EndY=0.25 EndZ=0
    g2: LineSegment StartX=7.75 StartY=0.25 StartZ=0 EndX=-7.75 EndY=0.25 EndZ=0
    g3: LineSegment StartX=-7.75 StartY=0.25 StartZ=0 EndX=-7.75 EndY=5.75 EndZ=0
    g4: Circle CenterX=0 CenterY=-7 CenterZ=0 NormalX=0 NormalY=0 NormalZ=1 AngleXU=0 Radius=6
    g5: ArcOfCircle CenterX=0 CenterY=-7 CenterZ=0 NormalX=0 NormalY=0 NormalZ=1 AngleXU=0 Radius=5.5 StartAngle=3.18706 EndAngle=4.66692
    g6: ArcOfCircle CenterX=0 CenterY=-7 CenterZ=0 NormalX=0 NormalY=0 NormalZ=1 AngleXU=0 Radius=3.175 StartAngle=3.22041 EndAngle=4.63357
    g7: ArcOfCircle CenterX=0 CenterY=-7 CenterZ=0 NormalX=0 NormalY=0 NormalZ=1 AngleXU=0 Radius=2.675 StartAngle=3.23519 EndAngle=4.61879
    g8: LineSegment StartX=-5.49432 StartY=-6.75 StartZ=0 EndX=-3.16514 EndY=-6.75 EndZ=0
    g9: LineSegment StartX=-5.49432 StartY=-7.25 StartZ=0 EndX=-3.16514 EndY=-7.25 EndZ=0
    g10: LineSegment StartX=0.25 StartY=-1.50568 StartZ=0 EndX=0.25 EndY=-3.83486 EndZ=0
    g11: LineSegment StartX=-0.25 StartY=-1.50568 StartZ=0 EndX=-0.25 EndY=-3.83486 EndZ=0
    g12: LineSegment [constr] StartX=-7.32001 StartY=-7 StartZ=0 EndX=7.24789 EndY=-7 EndZ=0
    g13: ArcOfCircle CenterX=0 CenterY=-7 CenterZ=0 NormalX=0 NormalY=0 NormalZ=1 AngleXU=0 Radius=2.675 StartAngle=0.0935945 EndAngle=1.4772
    g14: ArcOfCircle CenterX=0 CenterY=-7 CenterZ=0 NormalX=0 NormalY=0 NormalZ=1 AngleXU=0 Radius=3.175 StartAngle=0.0788218 EndAngle=1.49197
    g15: ArcOfCircle CenterX=0 CenterY=-7 CenterZ=0 NormalX=0 NormalY=0 NormalZ=1 AngleXU=0 Radius=5.5 StartAngle=0.0454702 EndAngle=1.52533
    g16: LineSegment StartX=3.16514 StartY=-7.25 StartZ=0 EndX=5.49432 EndY=-7.25 EndZ=0
    g17: LineSegment StartX=3.16514 StartY=-6.75 StartZ=0 EndX=5.49432 EndY=-6.75 EndZ=0
    g18: LineSegment StartX=-2.66329 StartY=-6.75 StartZ=0 EndX=2.66329 EndY=-6.75 EndZ=0
    g19: LineSegment StartX=-2.66329 StartY=-7.25 StartZ=0 EndX=2.66329 EndY=-7.25 EndZ=0
    g20: LineSegment StartX=-0.25 StartY=-4.33671 StartZ=0 EndX=-0.25 EndY=-9.66329 EndZ=0
    g21: LineSegment StartX=0.25 StartY=-4.33671 StartZ=0 EndX=0.25 EndY=-9.66329 EndZ=0
    g22: ArcOfCircle CenterX=0 CenterY=-7 CenterZ=0 NormalX=0 NormalY=0 NormalZ=1 AngleXU=0 Radius=2.675 StartAngle=1.66439 EndAngle=3.048
    g23: ArcOfCircle CenterX=0 CenterY=-7 CenterZ=0 NormalX=0 NormalY=0 NormalZ=1 AngleXU=0 Radius=2.675 StartAngle=4.80598 EndAngle=6.18959
    g24: ArcOfCircle CenterX=0 CenterY=-7 CenterZ=0 NormalX=0 NormalY=0 NormalZ=1 AngleXU=0 Radius=3.175 StartAngle=4.79121 EndAngle=6.20436
    g25: LineSegment StartX=0.25 StartY=-10.1651 StartZ=0 EndX=0.25 EndY=-12.4943 EndZ=0
    g26: LineSegment StartX=-0.25 StartY=-10.1651 StartZ=0 EndX=-0.25 EndY=-12.4943 EndZ=0
    g27: ArcOfCircle CenterX=0 CenterY=-7 CenterZ=0 NormalX=0 NormalY=0 NormalZ=1 AngleXU=0 Radius=5.5 StartAngle=4.75786 EndAngle=6.23772
    g28: ArcOfCircle CenterX=0 CenterY=-7 CenterZ=0 NormalX=0 NormalY=0 NormalZ=1 AngleXU=0 Radius=5.5 StartAngle=1.61627 EndAngle=3.09612
    g29: ArcOfCircle CenterX=0 CenterY=-7 CenterZ=0 NormalX=0 NormalY=0 NormalZ=1 AngleXU=0 Radius=3.175 StartAngle=1.64962 EndAngle=3.06277
  constraints (80):
    c: Coincident(g0,g1)
    c: Coincident(g1,g2)
    c: Coincident(g2,g3)
    c: Coincident(g3,g0)
    c: Horizontal(g2)
    c: Vertical(g1)
    c: Vertical(g3)
    c: Symmetric(g0,g0,g-2)
    c: DistanceX(g0,g0) = 15.5
    c: DistanceY(g1,g1) = 5.5
    c: PointOnObject(g4,g-2)
    c: Coincident(g5,g4)
    c: Coincident(g6,g4)
    c: Coincident(g7,g4)
    c: Diameter(g7) = 5.35
    c: Diameter(g6) = 6.35
    c: Diameter(g5) = 11
    c: Diameter(g4) = 12
    c: Horizontal(g8)
    c: Horizontal(g9)
    c: PointOnObject(g10,g5)
    c: Vertical(g10)
    c: Vertical(g11)
    c: Symmetric(g11,g10,g-2)
    c: DistanceX(g11,g10) = 0.5
    c: Horizontal(g12)
    c: Symmetric(g17,g16,g12)
    c: DistanceY(g16,g17) = 0.5
    c: Coincident(g28,g8)
    c: Coincident(g5,g9)
    c: Equal(g7,g13)
    c: Coincident(g7,g13)
    c: Equal(g6,g14)
    c: Coincident(g6,g14)
    c: Equal(g5,g15)
    c: Coincident(g15,g17)
    c: Coincident(g5,g15)
    c: Coincident(g27,g16)
    c: Coincident(g19,g23)
    c: Coincident(g16,g24)
    c: Tangent(g9,g16)
    c: Coincident(g18,g13)
    c: Coincident(g17,g14)
    c: Tangent(g8,g17)
    c: Coincident(g8,g29)
    c: Coincident(g18,g22)
    c: Tangent(g8,g18)
    c: Coincident(g9,g6)
    c: Coincident(g19,g7)
    c: Tangent(g9,g19)
    c: Tangent(g11,g20)
    c: Tangent(g10,g21)
    c: Equal(g13,g22)
    c: Coincident(g13,g21)
    c: Coincident(g22,g20)
    c: Coincident(g13,g22)
    c: Equal(g7,g23)
    c: Coincident(g7,g23)
    c: Equal(g6,g24)
    c: Coincident(g6,g24)
    c: Coincident(g21,g23)
    c: Coincident(g25,g24)
    c: Tangent(g21,g25)
    c: Coincident(g20,g7)
    c: Coincident(g26,g6)
    c: Tangent(g20,g26)
    c: Equal(g5,g27)
    c: Coincident(g5,g26)
    c: Coincident(g27,g25)
    c: Coincident(g5,g27)
    c: Equal(g15,g28)
    c: PointOnObject(g15,g10)
    c: PointOnObject(g28,g11)
    c: Coincident(g15,g28)
    c: DistanceY(g4,g-1) = 7
    c: DistanceY(g-1,g1) = 0.25
    c: Equal(g14,g29)
    c: Coincident(g14,g10)
    c: Coincident(g29,g11)
    c: Coincident(g14,g29)
FEATURE [PartDesign::Pocket] Pocket003
  BaseFeature = -> Mirrored
  ClaimChildren = false
  Fit = 0
  FitJoin = 0
  InnerFit = 0
  InnerFitJoin = 0
  InnerTaperAngle = 0
  InnerTaperAngleRev = 0
  Length = 0.2
  Length2 = 100
  Linearize = true
  NewSolid = false
  Placement = pos=(0,0,0) rot=(1,0,0;1.5708rad)
  Profile = -> Sketch004
  Refine = true
  Suppress = false
  Type = 0
  _ProfileBasedVersion = 1
FEATURE [App::Link] Link  label="Link(Limit sensor)"
  AutoLinkLabel = true
  AutoPlacement = true
  LinkedObject = -> Body
  SyncGroupVisibility = false
  _LinkVersion = 1
FEATURE [Sketcher::SketchObject] Sketch005
  ExternalGeometry = -> [Pocket003]
  FullyConstrained = true
  MapMode = 5
  Placement = pos=(0,0,0) rot=(-1,0,0;1.5708rad)
  Support = -> [Pocket003]
  sketch-geometry (2):
    g0: Circle CenterX=-6 CenterY=-10.5 CenterZ=0 NormalX=0 NormalY=0 NormalZ=1 AngleXU=0 Radius=1.5
    g1: Circle CenterX=6 CenterY=-10.5 CenterZ=0 NormalX=0 NormalY=0 NormalZ=1 AngleXU=0 Radius=1.5
  constraints (4):
    c: Symmetric(g-3,g-4,g0)
    c: Symmetric(g-5,g-6,g1)
    c: Equal(g1,g0)
    c: Diameter(g1) = 3
FEATURE [PartDesign::Body] Body  label="Limit sensor"
  AutoGroupSolids = false
  ExportMode = 0
  Group = -> [Sketch,Pad,Sketch001,Pocket,Sketch002,Pocket001,Sketch003,Pocket002,Mirrored,Sketch004,Pocket003,Sketch005]
  Origin = -> Origin
  Tip = -> Pocket003
  _ExportChildren = -> [Pad,Pocket,Pocket001,Pocket002,Mirrored,Pocket003,Sketch005]
  _GroupVersion = 1
FEATURE [Part::FeaturePython] Screw  label="M3x12-Screw"  # Fasteners workbench fastener (typed FeaturePython)
  Placement = pos=(15,-17,-3.8e-15) rot=(1,0,0;1.5708rad)
  diameter = 4
  invert = false
  length = 10
  lengthCustom = 12
  matchOuter = false
  offset = 0
  thread = false
  type = 33
FEATURE [App::DocumentObjectGroup] Group  label="Components"
  ExportMode = 1
  Group = -> [Body,Screw]
  _GroupVersion = 1
FEATURE [App::LinkElement] Link001_i0
  LinkPlacement = pos=(-9,10.5,-10.5) rot=(0,0,1;0rad)
  LinkedObject = -> Screw
  Placement = pos=(-9,10.5,-10.5) rot=(0,0,1;0rad)
  _LinkVersion = 0
FEATURE [App::LinkElement] Link001_i1
  LinkPlacement = pos=(-21,10.5,-10.5) rot=(0,0,1;0rad)
  LinkedObject = -> Screw
  Placement = pos=(-21,10.5,-10.5) rot=(0,0,1;0rad)
  _LinkVersion = 0
FEATURE [App::Link] Link001  label="M3x12-Screw 2pc"
  AutoLinkLabel = true
  AutoPlacement = true
  ElementCount = 2
  ElementList = -> [Link001_i0,Link001_i1]
  LinkPlacement = pos=(15,-17,-3.8e-15) rot=(1,0,0;1.5708rad)
  LinkedObject = -> Screw
  Placement = pos=(15,-17,-3.8e-15) rot=(1,0,0;1.5708rad)
  SyncGroupVisibility = false
  _LinkVersion = 1
FEATURE [Part::FeaturePython] Parts  # WARN: FeaturePython — macro-defined, semantics opaque (R4)
  Group = -> [Link,Link001]
  GroupMode = 0
  _LinkVersion = 1
FEATURE [App::DocumentObjectGroup] Group001  label="Assemblies"
  ExportMode = 1
  Group = -> [Assembly]
  _GroupVersion = 1
FEATURE [Part::FeaturePython] Assembly  label="Limit sensor Assembly"  # WARN: FeaturePython — macro-defined, semantics opaque (R4)
  AutoRelax = true
  BuildShape = 0
  Freeze = false
  Group = -> [Constraints,Elements,Parts]
  Verbose = false
  _LinkVersion = 1
  _SolverType = 1
  _Version = 1
FEATURE [App::FeaturePython] Constraints  # WARN: FeaturePython — macro-defined, semantics opaque (R4)
  Group = -> [Constraint,Constraint001,Constraint002]
  _LinkVersion = 1
  _Version = 1
FEATURE [App::FeaturePython] Elements  # WARN: FeaturePython — macro-defined, semantics opaque (R4)
  Group = -> [_Element,Element,Element001,_Element001,_Element002]
  _LinkVersion = 1
FEATURE [App::FeaturePython] Constraint  label="Locked"  # WARN: FeaturePython — macro-defined, semantics opaque (R4)
  Disabled = false
  Group = -> [ElementLink]
  _ConstraintType = 0
  _LinkVersion = 1
  _Parent = -> Constraints
FEATURE [App::FeaturePython] ElementLink  label="_Element"  # link proxy (typed FeaturePython)
  LinkTransform = true
  LinkedObject = -> _Element
  _LinkVersion = 1
  _Parent = -> Constraint
FEATURE [Part::FeaturePython] _Element  # link proxy (typed FeaturePython)
  Detach = false
  LinkTransform = true
  LinkedObject = -> Link [Pocket003.Face2]
  _LinkVersion = 1
  _Parent = -> Elements
FEATURE [Part::FeaturePython] Element  label="mate l"  # link proxy (typed FeaturePython)
  Detach = false
  LinkTransform = true
  LinkedObject = -> Link [Sketch005.Edge1]
  _LinkVersion = 1
  _Parent = -> Elements
FEATURE [Part::FeaturePython] Element001  label="mate r"  # link proxy (typed FeaturePython)
  Detach = false
  LinkTransform = true
  LinkedObject = -> Link [Sketch005.Edge2]
  _LinkVersion = 1
  _Parent = -> Elements
FEATURE [App::FeaturePython] Constraint001  label="Attachment"  # WARN: FeaturePython — macro-defined, semantics opaque (R4)
  Cascade = false
  Disabled = false
  Group = -> [ElementLink001,ElementLink002]
  Multiply = false
  _ConstraintType = 45
  _LinkVersion = 0
  _Parent = -> Constraints
FEATURE [App::FeaturePython] ElementLink001  label="_Element001"  # link proxy (typed FeaturePython)
  LinkTransform = true
  LinkedObject = -> _Element001
  Offset = pos=(0,0,-6.5) rot=(1,0,0;3.14159rad)
  Placement = pos=(-9e-16,-6.5,21) rot=(1,0,0;3.14159rad)
  _LinkVersion = 0
  _Parent = -> Constraint001
FEATURE [Part::FeaturePython] _Element001  # link proxy (typed FeaturePython)
  Detach = false
  LinkTransform = true
  LinkedObject = -> Link001 [0.Edge9]
  _LinkVersion = 0
  _Parent = -> Elements
FEATURE [App::FeaturePython] ElementLink002  label="mate r"  # link proxy (typed FeaturePython)
  LinkTransform = true
  LinkedObject = -> Element001
  _LinkVersion = 0
  _Parent = -> Constraint001
FEATURE [App::FeaturePython] Constraint002  label="Attachment001"  # WARN: FeaturePython — macro-defined, semantics opaque (R4)
  Cascade = false
  Disabled = false
  Group = -> [ElementLink003,ElementLink004]
  Multiply = false
  _ConstraintType = 45
  _LinkVersion = 0
  _Parent = -> Constraints
FEATURE [App::FeaturePython] ElementLink003  label="_Element002"  # link proxy (typed FeaturePython)
  LinkTransform = true
  LinkedObject = -> _Element002
  Offset = pos=(0,0,-6.5) rot=(1,0,0;3.14159rad)
  Placement = pos=(9e-16,-6.5,21) rot=(1,0,0;3.14159rad)
  _LinkVersion = 0
  _Parent = -> Constraint002
FEATURE [Part::FeaturePython] _Element002  # link proxy (typed FeaturePython)
  Detach = false
  LinkTransform = true
  LinkedObject = -> Link001 [1.Edge9]
  _LinkVersion = 0
  _Parent = -> Elements
FEATURE [App::FeaturePython] ElementLink004  label="mate l"  # link proxy (typed FeaturePython)
  LinkTransform = true
  LinkedObject = -> Element
  _LinkVersion = 0
  _Parent = -> Constraint002
---- part parts/NEMA23-76.FCStd = doc fcstd_c19784181319 ----
FCSTD DOCUMENT  (FreeCAD 2021.614R24301 +3747 (Git))
Label: NEMA23-76
License: Creative Commons Attribution
LicenseURL: http://creativecommons.org/licenses/by/4.0/
objects: App::FeaturePython×32, Part::FeaturePython×28, Sketcher::SketchObject×14, PartDesign::Pad×5, App::Link×5, PartDesign::Pocket×4, PartDesign::Hole×4, App::LinkElement×4, PartDesign::Body×2, PartDesign::Fillet×1, PartDesign::Line×1, PartDesign::SubtractiveHelix×1, PartDesign::Chamfer×1, App::DocumentObjectGroup×1
note: 91 computed .brp shape members not serialized (recipe doc carries the construction recipe); baked Part::Feature solids carry a one-line shape summary decoded from their .brp

FEATURE [Sketcher::SketchObject] Sketch
  FullyConstrained = true
  MapMode = 5
  Support = -> [XY_Plane]
  sketch-geometry (16):
    g0: LineSegment StartX=-23.55 StartY=28.2 StartZ=0 EndX=23.55 EndY=28.2 EndZ=0
    g1: LineSegment StartX=28.2 StartY=23.55 StartZ=0 EndX=28.2 EndY=-23.55 EndZ=0
    g2: LineSegment StartX=23.55 StartY=-28.2 StartZ=0 EndX=-23.55 EndY=-28.2 EndZ=0
    g3: LineSegment StartX=-28.2 StartY=-23.55 StartZ=0 EndX=-28.2 EndY=23.55 EndZ=0
    g4: ArcOfCircle CenterX=-23.55 CenterY=23.55 CenterZ=0 NormalX=0 NormalY=0 NormalZ=1 AngleXU=0 Radius=4.65 StartAngle=1.5708 EndAngle=3.14159
    g5: GeomPoint [constr] X=-28.2 Y=28.2 Z=0
    g6: ArcOfCircle CenterX=23.55 CenterY=23.55 CenterZ=0 NormalX=0 NormalY=0 NormalZ=1 AngleXU=0 Radius=4.65 StartAngle=0 EndAngle=1.5708
    g7: GeomPoint [constr] X=28.2 Y=28.2 Z=0
    g8: ArcOfCircle CenterX=23.55 CenterY=-23.55 CenterZ=0 NormalX=0 NormalY=0 NormalZ=1 AngleXU=0 Radius=4.65 StartAngle=4.71239 EndAngle=6.28319
    g9: GeomPoint [constr] X=28.2 Y=-28.2 Z=0
    g10: ArcOfCircle CenterX=-23.55 CenterY=-23.55 CenterZ=0 NormalX=0 NormalY=0 NormalZ=1 AngleXU=0 Radius=4.65 StartAngle=3.14159 EndAngle=4.71239
    g11: GeomPoint [constr] X=-28.2 Y=-28.2 Z=0
    g12: Circle CenterX=-23.55 CenterY=23.55 CenterZ=0 NormalX=0 NormalY=0 NormalZ=1 AngleXU=0 Radius=2.55
    g13: Circle CenterX=23.55 CenterY=23.55 CenterZ=0 NormalX=0 NormalY=0 NormalZ=1 AngleXU=0 Radius=2.55
    g14: Circle CenterX=23.55 CenterY=-23.55 CenterZ=0 NormalX=0 NormalY=0 NormalZ=1 AngleXU=0 Radius=2.55
    g15: Circle CenterX=-23.55 CenterY=-23.55 CenterZ=0 NormalX=0 NormalY=0 NormalZ=1 AngleXU=0 Radius=2.55
  constraints (35):
    c: Horizontal(g0)
    c: Horizontal(g2)
    c: Vertical(g1)
    c: Vertical(g3)
    c: Symmetric(g9,g5,g-1)
    c: PointOnObject(g5,g0)
    c: PointOnObject(g5,g3)
    c: Tangent(g0,g4) = 1.5708
    c: Tangent(g3,g4) = 1.5708
    c: PointOnObject(g7,g0)
    c: PointOnObject(g7,g1)
    c: Tangent(g0,g6) = 1.5708
    c: Tangent(g1,g6) = 1.5708
    c: PointOnObject(g9,g1)
    c: PointOnObject(g9,g2)
    c: Tangent(g1,g8) = 1.5708
    c: Tangent(g2,g8) = 1.5708
    c: PointOnObject(g11,g2)
    c: PointOnObject(g11,g3)
    c: Tangent(g2,g10) = 1.5708
    c: Tangent(g3,g10) = 1.5708
    c: Equal(g10,g8)
    c: Equal(g8,g6)
    c: Equal(g6,g4)
    c: Equal(g0,g1)
    c: DistanceX(g3,g1) = 56.4
    c: Coincident(g12,g4)
    c: Coincident(g13,g6)
    c: Coincident(g14,g8)
    c: Coincident(g15,g10)
    c: Equal(g15,g14)
    c: Equal(g14,g13)
    c: Equal(g13,g12)
    c: Diameter(g12) = 5.1
    c: DistanceX(g4,g6) = 47.1
FEATURE [PartDesign::Pad] Pad
  ClaimChildren = false
  Direction = (1,1,1)
  Fit = 0
  FitJoin = 0
  InnerFit = 0
  InnerFitJoin = 0
  InnerTaperAngle = 0
  InnerTaperAngleRev = 0
  Length = 6
  Length2 = 100
  Linearize = true
  NewSolid = false
  Profile = -> Sketch
  Refine = true
  Suppress = false
  Type = 0
FEATURE [Sketcher::SketchObject] Sketch001
  ExternalGeometry = -> [Pad]
  FullyConstrained = true
  MapMode = 5
  Placement = pos=(0,0,6) rot=(0,0,1;0rad)
  Support = -> [Pad]
  sketch-geometry (16):
    g0: LineSegment StartX=-18.55 StartY=28.2 StartZ=0 EndX=18.55 EndY=28.2 EndZ=0
    g1: LineSegment StartX=28.2 StartY=18.55 StartZ=0 EndX=28.2 EndY=-18.55 EndZ=0
    g2: LineSegment StartX=18.55 StartY=-28.2 StartZ=0 EndX=-18.55 EndY=-28.2 EndZ=0
    g3: LineSegment StartX=-28.2 StartY=-18.55 StartZ=0 EndX=-28.2 EndY=18.55 EndZ=0
    g4: ArcOfCircle CenterX=-23.55 CenterY=23.55 CenterZ=0 NormalX=0 NormalY=0 NormalZ=1 AngleXU=0 Radius=5 StartAngle=4.71239 EndAngle=6.28319
    g5: ArcOfCircle CenterX=23.55 CenterY=23.55 CenterZ=0 NormalX=0 NormalY=0 NormalZ=1 AngleXU=0 Radius=5 StartAngle=3.14159 EndAngle=4.71239
    g6: ArcOfCircle CenterX=23.55 CenterY=-23.55 CenterZ=0 NormalX=0 NormalY=0 NormalZ=1 AngleXU=0 Radius=5 StartAngle=1.5708 EndAngle=3.14159
    g7: ArcOfCircle CenterX=-23.55 CenterY=-23.55 CenterZ=0 NormalX=0 NormalY=0 NormalZ=1 AngleXU=0 Radius=5 StartAngle=1e-16 EndAngle=1.5708
    g8: LineSegment StartX=-18.55 StartY=28.2 StartZ=0 EndX=-18.55 EndY=23.55 EndZ=0
    g9: LineSegment StartX=-23.55 StartY=18.55 StartZ=0 EndX=-28.2 EndY=18.55 EndZ=0
    g10: LineSegment StartX=18.55 StartY=23.55 StartZ=0 EndX=18.55 EndY=28.2 EndZ=0
    g11: LineSegment StartX=23.55 StartY=18.55 StartZ=0 EndX=28.2 EndY=18.55 EndZ=0
    g12: LineSegment StartX=23.55 StartY=-18.55 StartZ=0 EndX=28.2 EndY=-18.55 EndZ=0
    g13: LineSegment StartX=18.55 StartY=-23.55 StartZ=0 EndX=18.55 EndY=-28.2 EndZ=0
    g14: LineSegment StartX=-18.55 StartY=-23.55 StartZ=0 EndX=-18.55 EndY=-28.2 EndZ=0
    g15: LineSegment StartX=-23.55 StartY=-18.55 StartZ=0 EndX=-28.2 EndY=-18.55 EndZ=0
  constraints (40):
    c: Horizontal(g0)
    c: Horizontal(g2)
    c: Vertical(g1)
    c: Vertical(g3)
    c: Coincident(g4,g-4)
    c: Vertical(g7,g4)
    c: Horizontal(g4,g5)
    c: Vertical(g5,g6)
    c: Horizontal(g7,g6)
    c: Symmetric(g6,g4,g-1)
    c: Equal(g5,g4)
    c: Equal(g4,g7)
    c: Equal(g7,g6)
    c: Diameter(g4) = 10
    c: Vertical(g10)
    c: Horizontal(g11)
    c: Horizontal(g12)
    c: Vertical(g14)
    c: Vertical(g8)
    c: Horizontal(g9)
    c: Coincident(g0,g8)
    c: Coincident(g3,g9)
    c: Coincident(g0,g10)
    c: Coincident(g1,g11)
    c: Coincident(g1,g12)
    c: Coincident(g2,g13)
    c: Tangent(g6,g13) = -1.5708
    c: Coincident(g3,g15)
    c: Tangent(g7,g14) = 1.5708
    c: Coincident(g2,g14)
    c: Tangent(g7,g15) = -1.5708
    c: Tangent(g6,g12) = 1.5708
    c: Tangent(g5,g10) = 1.5708
    c: Tangent(g5,g11) = -1.5708
    c: Tangent(g4,g8) = 1.5708
    c: Tangent(g4,g9) = 1.5708
    c: Horizontal(g0,g-4)
    c: Vertical(g3,g-4)
    c: Symmetric(g2,g0,g-1)
    c: Symmetric(g1,g3,g-2)
FEATURE [PartDesign::Pad] Pad001
  BaseFeature = -> Pad
  ClaimChildren = false
  Direction = (1,1,1)
  Fit = 0
  FitJoin = 0
  InnerFit = 0
  InnerFitJoin = 0
  InnerTaperAngle = 0
  InnerTaperAngleRev = 0
  Length = 70
  Length2 = 100
  Linearize = true
  NewSolid = false
  Profile = -> Sketch001
  Refine = true
  Suppress = false
  Type = 0
FEATURE [Sketcher::SketchObject] Sketch002
  FullyConstrained = true
  MapMode = 5
  Placement = pos=(0,0,0) rot=(1,0,0;3.14159rad)
  Support = -> [Pad001]
  sketch-geometry (1):
    g0: Circle CenterX=0 CenterY=0 CenterZ=0 NormalX=0 NormalY=0 NormalZ=1 AngleXU=0 Radius=19.05
  constraints (2):
    c: Coincident(g0,g-1)
    c: Diameter(g0) = 38.1
FEATURE [PartDesign::Pad] Pad002
  BaseFeature = -> Pad001
  ClaimChildren = false
  Direction = (1,1,1)
  Fit = 0
  FitJoin = 0
  InnerFit = 0
  InnerFitJoin = 0
  InnerTaperAngle = 0
  InnerTaperAngleRev = 0
  Length = 1.6
  Length2 = 100
  Linearize = true
  NewSolid = false
  Profile = -> Sketch002
  Refine = true
  Suppress = false
  Type = 0
FEATURE [Sketcher::SketchObject] Sketch003
  FullyConstrained = true
  MapMode = 5
  Placement = pos=(0,0,-1.6) rot=(1,0,0;3.14159rad)
  Support = -> [Pad002]
  sketch-geometry (1):
    g0: Circle CenterX=0 CenterY=0 CenterZ=0 NormalX=0 NormalY=0 NormalZ=1 AngleXU=0 Radius=3.175
  constraints (2):
    c: Coincident(g0,g-1)
    c: Diameter(g0) = 6.35
FEATURE [PartDesign::Pad] Pad003
  BaseFeature = -> Pad002
  ClaimChildren = false
  Direction = (1,1,1)
  Fit = 0
  FitJoin = 0
  InnerFit = 0
  InnerFitJoin = 0
  InnerTaperAngle = 0
  InnerTaperAngleRev = 0
  Length = 20
  Length2 = 100
  Linearize = true
  NewSolid = false
  Profile = -> Sketch003
  Refine = true
  Suppress = false
  Type = 0
FEATURE [PartDesign::Fillet] Fillet
  Base = -> Pad003 [Edge71,Edge8,Edge6,Edge16,Edge14,Edge68,Edge67,Edge72,Edge39,Edge40,Edge43,Edge44,Edge15,Edge47,Edge7,Edge36]
  BaseFeature = -> Pad003
  NewSolid = false
  Radius = 1.5
  Refine = true
  SupportTransform = false
  Suppress = false
FEATURE [App::Link] Link  label="Link(Nema23)"
  AutoLinkLabel = true
  LinkedObject = -> Body
  SyncGroupVisibility = false
  _LinkVersion = 1
FEATURE [PartDesign::Line] DatumLine
  AttacherType = Attacher::AttachEngineLine
  Length = 97.6
  MapMode = 19
  MinimumLength = 10
  Placement = pos=(0,0,-21.6) rot=(-1,0,0;3.14159rad)
  ResizeMode = 0
  Support = -> [Fillet]
FEATURE [PartDesign::Body] Body  label="Nema23"
  AutoGroupSolids = false
  ExportMode = 0
  Group = -> [Sketch,Pad,Sketch001,Pad001,Sketch002,Pad002,Sketch003,Pad003,Fillet,DatumLine]
  Origin = -> Origin
  Tip = -> Fillet
  _ExportChildren = -> [Pad,Pad001,Pad002,Pad003,Fillet,DatumLine]
  _GroupVersion = 1
FEATURE [Sketcher::SketchObject] Sketch004
  FullyConstrained = true
  MapMode = 5
  Support = -> [XY_Plane001]
  sketch-geometry (1):
    g0: Circle CenterX=0 CenterY=0 CenterZ=0 NormalX=0 NormalY=0 NormalZ=1 AngleXU=0 Radius=12.5
  constraints (2):
    c: Coincident(g0,g-1)
    c: Diameter(g0) = 25
FEATURE [PartDesign::Pad] Pad004
  ClaimChildren = false
  Direction = (1,1,1)
  Fit = 0
  FitJoin = 0
  InnerFit = 0
  InnerFitJoin = 0
  InnerTaperAngle = 0
  InnerTaperAngleRev = 0
  Length = 30
  Length2 = 100
  Linearize = true
  Midplane = true
  NewSolid = false
  Profile = -> Sketch004
  Refine = true
  Suppress = false
  Type = 0
FEATURE [Sketcher::SketchObject] Sketch005
  FullyConstrained = true
  MapMode = 5
  Placement = pos=(0,0,15) rot=(0,0,1;0rad)
  Support = -> [Pad004]
  sketch-geometry (1):
    g0: Circle CenterX=0 CenterY=0 CenterZ=0 NormalX=0 NormalY=0 NormalZ=1 AngleXU=0 Radius=3.175
  constraints (2):
    c: Coincident(g0,g-1)
    c: Diameter(g0) = 6.35
FEATURE [PartDesign::Pocket] Pocket
  BaseFeature = -> Pad004
  ClaimChildren = false
  Fit = 0
  FitJoin = 0
  InnerFit = 0
  InnerFitJoin = 0
  InnerTaperAngle = 0
  InnerTaperAngleRev = 0
  Length = 5
  Length2 = 100
  Linearize = true
  NewSolid = false
  Profile = -> Sketch005
  Refine = true
  Suppress = false
  Type = 1
FEATURE [Sketcher::SketchObject] Sketch006
  FullyConstrained = true
  MapMode = 5
  Placement = pos=(0,0,15) rot=(0,0,1;0rad)
  Support = -> [Pocket]
  sketch-geometry (1):
    g0: Circle CenterX=0 CenterY=0 CenterZ=0 NormalX=0 NormalY=0 NormalZ=1 AngleXU=0 Radius=5
  constraints (2):
    c: Coincident(g0,g-1)
    c: Diameter(g0) = 10
FEATURE [PartDesign::Pocket] Pocket001
  BaseFeature = -> Pocket
  ClaimChildren = false
  Fit = 0
  FitJoin = 0
  InnerFit = 0
  InnerFitJoin = 0
  InnerTaperAngle = 0
  InnerTaperAngleRev = 0
  Length = 21.5
  Length2 = 100
  Linearize = true
  NewSolid = false
  Profile = -> Sketch006
  Refine = true
  Suppress = false
  Type = 0
FEATURE [Sketcher::SketchObject] Sketch007
  FullyConstrained = true
  MapMode = 5
  Placement = pos=(0,0,15) rot=(0,0,1;0rad)
  Support = -> [Pocket001]
  sketch-geometry (4):
    g0: LineSegment StartX=-11.5 StartY=0.5 StartZ=0 EndX=13.5 EndY=0.5 EndZ=0
    g1: LineSegment StartX=13.5 StartY=0.5 StartZ=0 EndX=13.5 EndY=-0.5 EndZ=0
    g2: LineSegment StartX=13.5 StartY=-0.5 StartZ=0 EndX=-11.5 EndY=-0.5 EndZ=0
    g3: LineSegment StartX=-11.5 StartY=-0.5 StartZ=0 EndX=-11.5 EndY=0.5 EndZ=0
  constraints (11):
    c: Coincident(g0,g1)
    c: Coincident(g1,g2)
    c: Coincident(g2,g3)
    c: Coincident(g3,g0)
    c: Horizontal(g0)
    c: Horizontal(g2)
    c: DistanceY(g1,g1) = 1
    c: Symmetric(g1,g0,g-1)
    c: DistanceX(g2,g2) = 25
    c: Vertical(g3)
    c: DistanceX(g2,g-1) = 11.5
FEATURE [Sketcher::SketchObject] Sketch008
  FullyConstrained = true
  MapMode = 5
  Placement = pos=(0,0,0) rot=(1,0,0;1.5708rad)
  Support = -> [XZ_Plane001]
  sketch-geometry (2):
    g0: Circle CenterX=0 CenterY=10 CenterZ=0 NormalX=0 NormalY=0 NormalZ=1 AngleXU=0 Radius=1.75
    g1: Circle CenterX=0 CenterY=-10 CenterZ=0 NormalX=0 NormalY=0 NormalZ=1 AngleXU=0 Radius=1.75
  constraints (5):
    c: PointOnObject(g0,g-2)
    c: Equal(g1,g0)
    c: Symmetric(g0,g1,g-1)
    c: DistanceY(g1,g0) = 20
    c: Diameter(g0) = 3.5
FEATURE [PartDesign::Hole] Hole
  BaseFeature = -> Pocket001
  ClaimChildren = false
  CustomThreadClearance = 0
  Depth = 25
  DepthType = 1
  Diameter = 4.5
  DrillForDepth = false
  DrillPoint = 1
  DrillPointAngle = 118
  Fit = 0
  FitJoin = 0
  HoleCutCountersinkAngle = 90
  HoleCutCustomValues = false
  HoleCutDepth = 0
  HoleCutDiameter = 6.1
  HoleCutType = 0
  InnerFit = 0
  InnerFitJoin = 0
  ModelThread = false
  NewSolid = false
  Profile = -> Sketch008
  Refine = true
  Reversed = true
  Suppress = false
  Tapered = false
  TaperedAngle = 90
  ThreadClass = 0
  ThreadDepth = 93.5288
  ThreadDepthType = 0
  ThreadDirection = 0
  ThreadFit = 0
  ThreadSize = 0
  ThreadType = 0
  Threaded = false
  UseCustomThreadClearance = false
FEATURE [Sketcher::SketchObject] Sketch009
  FullyConstrained = true
  MapMode = 5
  Placement = pos=(0,0,0) rot=(1,0,0;1.5708rad)
  Support = -> [XZ_Plane001]
  sketch-geometry (2):
    g0: Circle CenterX=8 CenterY=10 CenterZ=0 NormalX=0 NormalY=0 NormalZ=1 AngleXU=0 Radius=1.25
    g1: Circle CenterX=8 CenterY=-10 CenterZ=0 NormalX=0 NormalY=0 NormalZ=1 AngleXU=0 Radius=1.25
  constraints (5):
    c: Symmetric(g0,g1,g-1)
    c: DistanceX(g-1,g0) = 8
    c: DistanceY(g1,g0) = 20
    c: Equal(g0,g1)
    c: Diameter(g0) = 2.5
FEATURE [Sketcher::SketchObject] Sketch010
  FullyConstrained = true
  MapMode = 5
  Placement = pos=(0,0,0) rot=(1,0,0;1.5708rad)
  Support = -> [XZ_Plane001]
  sketch-geometry (2):
    g0: Circle CenterX=8 CenterY=10 CenterZ=0 NormalX=0 NormalY=0 NormalZ=1 AngleXU=0 Radius=1.25
    g1: Circle CenterX=8 CenterY=-10 CenterZ=0 NormalX=0 NormalY=0 NormalZ=1 AngleXU=0 Radius=1.25
  constraints (5):
    c: Symmetric(g0,g1,g-1)
    c: DistanceX(g-1,g0) = 8
    c: DistanceY(g1,g0) = 20
    c: Equal(g0,g1)
    c: Diameter(g0) = 2.5
FEATURE [Sketcher::SketchObject] Sketch011
  AttachmentOffset = pos=(0,0,-4) rot=(0,0,1;0rad)
  FullyConstrained = true
  MapMode = 5
  Placement = pos=(0,4,9e-16) rot=(1,0,0;1.5708rad)
  Support = -> [XZ_Plane001]
  sketch-geometry (2):
    g0: Circle CenterX=8 CenterY=10 CenterZ=0 NormalX=0 NormalY=0 NormalZ=1 AngleXU=0 Radius=1.25
    g1: Circle CenterX=8 CenterY=-10 CenterZ=0 NormalX=0 NormalY=0 NormalZ=1 AngleXU=0 Radius=1.25
  constraints (5):
    c: Symmetric(g0,g1,g-1)
    c: DistanceX(g-1,g0) = 8
    c: DistanceY(g1,g0) = 20
    c: Equal(g0,g1)
    c: Diameter(g0) = 2.5
FEATURE [PartDesign::Hole] Hole001
  BaseFeature = -> Hole
  ClaimChildren = false
  CustomThreadClearance = 0
  Depth = 25
  DepthType = 1
  Diameter = 2.5
  DrillForDepth = false
  DrillPoint = 1
  DrillPointAngle = 118
  Fit = 0
  FitJoin = 0
  HoleCutCountersinkAngle = 90
  HoleCutCustomValues = false
  HoleCutDepth = 0
  HoleCutDiameter = 6.1
  HoleCutType = 0
  InnerFit = 0
  InnerFitJoin = 0
  ModelThread = false
  NewSolid = false
  Profile = -> Sketch009
  Refine = true
  Reversed = true
  Suppress = false
  Tapered = false
  TaperedAngle = 90
  ThreadClass = 0
  ThreadDepth = 93.5621
  ThreadDepthType = 0
  ThreadDirection = 0
  ThreadFit = 0
  ThreadSize = 0
  ThreadType = 0
  Threaded = false
  UseCustomThreadClearance = false
FEATURE [PartDesign::Hole] Hole002
  BaseFeature = -> Hole001
  ClaimChildren = false
  CustomThreadClearance = 0
  Depth = 25
  DepthType = 1
  Diameter = 3.1
  DrillForDepth = false
  DrillPoint = 1
  DrillPointAngle = 118
  Fit = 0
  FitJoin = 0
  HoleCutCountersinkAngle = 90
  HoleCutCustomValues = false
  HoleCutDepth = 0
  HoleCutDiameter = 6.1
  HoleCutType = 0
  InnerFit = 0
  InnerFitJoin = 0
  ModelThread = false
  NewSolid = false
  Profile = -> Sketch010
  Refine = true
  Suppress = false
  Tapered = false
  TaperedAngle = 90
  ThreadClass = 0
  ThreadDepth = 93.56
  ThreadDepthType = 0
  ThreadDirection = 0
  ThreadFit = 0
  ThreadSize = 0
  ThreadType = 0
  Threaded = false
  UseCustomThreadClearance = false
FEATURE [PartDesign::Hole] Hole003
  BaseFeature = -> Hole002
  ClaimChildren = false
  CustomThreadClearance = 0
  Depth = 25
  DepthType = 1
  Diameter = 6
  DrillForDepth = false
  DrillPoint = 1
  DrillPointAngle = 118
  Fit = 0
  FitJoin = 0
  HoleCutCountersinkAngle = 90
  HoleCutCustomValues = false
  HoleCutDepth = 0
  HoleCutDiameter = 6.1
  HoleCutType = 0
  InnerFit = 0
  InnerFitJoin = 0
  ModelThread = false
  NewSolid = false
  Profile = -> Sketch011
  Refine = true
  Suppress = false
  Tapered = false
  TaperedAngle = 90
  ThreadClass = 0
  ThreadDepth = 93.56
  ThreadDepthType = 0
  ThreadDirection = 0
  ThreadFit = 0
  ThreadSize = 0
  ThreadType = 0
  Threaded = false
  UseCustomThreadClearance = false
FEATURE [Sketcher::SketchObject] Sketch012
  AttachmentOffset = pos=(0,0,0) rot=(0,1,0;0.349066rad)
  ExternalGeometry = -> [Hole003]
  FullyConstrained = true
  MapMode = 5
  Placement = pos=(0,0,0) rot=(0.443713,0.633687,0.633687;2.30637rad)
  Support = -> [YZ_Plane001]
  sketch-geometry (4):
    g0: LineSegment StartX=4 StartY=-6.25 StartZ=0 EndX=14 EndY=-6.25 EndZ=0
    g1: LineSegment StartX=14 StartY=-6.25 StartZ=0 EndX=14 EndY=-6.75 EndZ=0
    g2: LineSegment StartX=14 StartY=-6.75 StartZ=0 EndX=4 EndY=-6.75 EndZ=0
    g3: LineSegment StartX=4 StartY=-6.75 StartZ=0 EndX=4 EndY=-6.25 EndZ=0
  constraints (12):
    c: Coincident(g0,g1)
    c: Coincident(g1,g2)
    c: Coincident(g2,g3)
    c: Coincident(g3,g0)
    c: Horizontal(g0)
    c: Horizontal(g2)
    c: Vertical(g1)
    c: Vertical(g3)
    c: DistanceY(g1,g1) = 0.5
    c: DistanceX(g2,g2) = 10
    c: DistanceX(g-1,g0) = 4
    c: DistanceY(g-3,g2) = 8.25
FEATURE [PartDesign::SubtractiveHelix] SubtractiveHelix
  Angle = 0
  Axis = (-2e-16,2e-16,1)
  Base = (0,0,0)
  BaseFeature = -> Hole003
  ClaimChildren = false
  Fit = 0
  FitJoin = 0
  HasBeenEdited = true
  Height = 13
  InnerFit = 0
  InnerFitJoin = 0
  LeftHanded = false
  Mode = 0
  NewSolid = false
  Outside = false
  Pitch = 3
  Profile = -> Sketch012
  ReferenceAxis = -> Sketch012 [V_Axis]
  Refine = true
  Suppress = false
  Turns = 3
FEATURE [PartDesign::Pocket] Pocket002
  BaseFeature = -> SubtractiveHelix
  ClaimChildren = false
  Fit = 0
  FitJoin = 0
  InnerFit = 0
  InnerFitJoin = 0
  InnerTaperAngle = 0
  InnerTaperAngleRev = 0
  Length = 10.5
  Length2 = 100
  Linearize = true
  NewSolid = false
  Profile = -> Sketch007
  Refine = true
  Suppress = false
  Type = 0
FEATURE [Sketcher::SketchObject] Sketch013
  FullyConstrained = true
  MapMode = 5
  Placement = pos=(0,0,-15) rot=(1,0,0;3.14159rad)
  Support = -> [Pocket002]
  sketch-geometry (4):
    g0: LineSegment StartX=-11.5 StartY=0.5 StartZ=0 EndX=13.5 EndY=0.5 EndZ=0
    g1: LineSegment StartX=13.5 StartY=0.5 StartZ=0 EndX=13.5 EndY=-0.5 EndZ=0
    g2: LineSegment StartX=13.5 StartY=-0.5 StartZ=0 EndX=-11.5 EndY=-0.5 EndZ=0
    g3: LineSegment StartX=-11.5 StartY=-0.5 StartZ=0 EndX=-11.5 EndY=0.5 EndZ=0
  constraints (11):
    c: Coincident(g0,g1)
    c: Coincident(g1,g2)
    c: Coincident(g2,g3)
    c: Coincident(g3,g0)
    c: Horizontal(g0)
    c: Horizontal(g2)
    c: Vertical(g3)
    c: DistanceY(g1,g1) = 1
    c: Symmetric(g1,g0,g-1)
    c: DistanceX(g2,g2) = 25
    c: DistanceX(g2,g-1) = 11.5
FEATURE [PartDesign::Pocket] Pocket003
  BaseFeature = -> Pocket002
  ClaimChildren = false
  Fit = 0
  FitJoin = 0
  InnerFit = 0
  InnerFitJoin = 0
  InnerTaperAngle = 0
  InnerTaperAngleRev = 0
  Length = 10
  Length2 = 100
  Linearize = true
  NewSolid = false
  Profile = -> Sketch013
  Refine = true
  Suppress = false
  Type = 0
FEATURE [App::Link] Link001  label="Link001(Coupling)"
  AutoLinkLabel = true
  LinkedObject = -> Body001
  SyncGroupVisibility = false
  _LinkVersion = 1
FEATURE [Part::FeaturePython] Screw  label="M3x12-Screw"  # Fasteners workbench fastener (typed FeaturePython)
  Placement = pos=(8,4,-10) rot=(0,0.707107,0.707107;3.14159rad)
  diameter = 4
  invert = false
  length = 4
  lengthCustom = 12
  matchOuter = false
  offset = 0
  thread = false
  type = 33
FEATURE [Part::FeaturePython] Screw001  label="M4x8-Screw"  # Fasteners workbench fastener (typed FeaturePython)
  Placement = pos=(0,-10.23,-10) rot=(1,0,0;1.5708rad)
  diameter = 7
  invert = false
  length = 3
  lengthCustom = 8
  matchOuter = false
  offset = 0
  thread = false
  type = 29
FEATURE [App::Link] Link002  label="Link002(M4x8-Screw)"
  AutoLinkLabel = true
  LinkPlacement = pos=(0,-12.23,10) rot=(1,0,0;1.5708rad)
  LinkedObject = -> Screw001
  Placement = pos=(0,-12.23,10) rot=(1,0,0;1.5708rad)
  SyncGroupVisibility = false
  _LinkVersion = 1
FEATURE [App::Link] Link003  label="Link003(M3x12-Screw)"
  AutoLinkLabel = true
  LinkPlacement = pos=(8,4,10) rot=(0,0.707107,0.707107;3.14159rad)
  LinkedObject = -> Screw
  Placement = pos=(8,4,10) rot=(0,0.707107,0.707107;3.14159rad)
  SyncGroupVisibility = false
  _LinkVersion = 1
FEATURE [Part::FeaturePython] Parts001  # WARN: FeaturePython — macro-defined, semantics opaque (R4)
  Group = -> [Link001,Screw,Screw001,Link002,Link003]
  GroupMode = 0
  _LinkVersion = 1
FEATURE [PartDesign::Chamfer] Chamfer
  Angle = 45
  Base = -> Pocket003 [Edge115,Edge1,Edge17,Edge21,Edge138,Edge143]
  BaseFeature = -> Pocket003
  ChamferType = 0
  FlipDirection = false
  NewSolid = false
  Refine = true
  Size = 0.5
  Size2 = 1
  SupportTransform = false
  Suppress = false
FEATURE [PartDesign::Body] Body001  label="Coupling"
  AutoGroupSolids = false
  ExportMode = 0
  Group = -> [Sketch004,Pad004,Sketch005,Pocket,Sketch006,Pocket001,Sketch007,Sketch008,Hole,Sketch009,Sketch010,Sketch011,Hole001,Hole002,Hole003,Sketch012,SubtractiveHelix,Pocket002,Sketch013,Pocket003,Chamfer]
  Origin = -> Origin001
  Placement = pos=(0,0,-51) rot=(0,0,1;0rad)
  Tip = -> Chamfer
  _ExportChildren = -> [Pad004,Pocket,Pocket001,Hole,Hole001,Hole002,Hole003,SubtractiveHelix,Pocket002,Pocket003,Chamfer]
  _GroupVersion = 1
FEATURE [Part::FeaturePython] Screw002  label="M5x16-Screw"  # Fasteners workbench fastener (typed FeaturePython)
  diameter = 6
  invert = false
  length = 4
  lengthCustom = 16
  matchOuter = false
  offset = 0
  thread = false
  type = 33
FEATURE [App::DocumentObjectGroup] Group  label="Components"
  ExportMode = 1
  Group = -> [Body001,Body,Screw002]
  _GroupVersion = 1
FEATURE [App::LinkElement] Link004_i0
  LinkPlacement = pos=(23.55,67.55,6) rot=(0,0,1;0rad)
  LinkedObject = -> Screw002
  Placement = pos=(23.55,67.55,6) rot=(0,0,1;0rad)
  _LinkVersion = 1
FEATURE [App::LinkElement] Link004_i1
  LinkPlacement = pos=(-23.55,67.55,6) rot=(0,0,1;0rad)
  LinkedObject = -> Screw002
  Placement = pos=(-23.55,67.55,6) rot=(0,0,1;0rad)
  _LinkVersion = 1
FEATURE [App::LinkElement] Link004_i2
  LinkPlacement = pos=(-23.55,20.45,6) rot=(0,0,1;0rad)
  LinkedObject = -> Screw002
  Placement = pos=(-23.55,20.45,6) rot=(0,0,1;0rad)
  _LinkVersion = 1
FEATURE [App::LinkElement] Link004_i3
  LinkPlacement = pos=(23.55,20.45,6) rot=(0,0,1;0rad)
  LinkedObject = -> Screw002
  Placement = pos=(23.55,20.45,6) rot=(0,0,1;0rad)
  _LinkVersion = 1
FEATURE [App::Link] Link004  label="M5x16-Screw 4ct"
  AutoLinkLabel = true
  ElementCount = 4
  ElementList = -> [Link004_i0,Link004_i1,Link004_i2,Link004_i3]
  LinkPlacement = pos=(0,-44,0) rot=(0,0,1;0rad)
  LinkedObject = -> Screw002
  Placement = pos=(0,-44,0) rot=(0,0,1;0rad)
  SyncGroupVisibility = false
  _LinkVersion = 1
FEATURE [Part::FeaturePython] Parts  # WARN: FeaturePython — macro-defined, semantics opaque (R4)
  Group = -> [Link,Link004]
  GroupMode = 0
  _LinkVersion = 1
FEATURE [Part::FeaturePython] Assembly  label="NEMA23-76-Assembly"  # WARN: FeaturePython — macro-defined, semantics opaque (R4)
  AutoRelax = true
  BuildShape = 0
  Freeze = false
  Group = -> [Constraints,Elements,Parts]
  Verbose = false
  _LinkVersion = 1
  _SolverType = 1
  _Version = 1
FEATURE [App::FeaturePython] Constraints  # WARN: FeaturePython — macro-defined, semantics opaque (R4)
  Group = -> [Constraint004,Constraint006,Constraint007,Constraint008,Constraint009]
  _LinkVersion = 1
  _Version = 1
FEATURE [App::FeaturePython] Elements  # WARN: FeaturePython — macro-defined, semantics opaque (R4)
  Group = -> [Element,Element001,Element002,Element003,Element004,Element005,Element010,_Element006,_Element007,_Element008,_Element009]
  _LinkVersion = 1
FEATURE [Part::FeaturePython] Element  # link proxy (typed FeaturePython)
  Detach = false
  LinkTransform = true
  LinkedObject = -> Link [Fillet.Edge19]
  _LinkVersion = 1
  _Parent = -> Elements
FEATURE [Part::FeaturePython] Element001  # link proxy (typed FeaturePython)
  Detach = false
  LinkTransform = true
  LinkedObject = -> Link [Fillet.Edge49]
  _LinkVersion = 1
  _Parent = -> Elements
FEATURE [Part::FeaturePython] Element002  # link proxy (typed FeaturePython)
  Detach = false
  LinkTransform = true
  LinkedObject = -> Link [Fillet.Edge101]
  _LinkVersion = 1
  _Parent = -> Elements
FEATURE [Part::FeaturePython] Element003  # link proxy (typed FeaturePython)
  Detach = false
  LinkTransform = true
  LinkedObject = -> Link [Fillet.Edge103]
  _LinkVersion = 1
  _Parent = -> Elements
FEATURE [Part::FeaturePython] Element004  label="bracket-mate"  # link proxy (typed FeaturePython)
  Detach = false
  LinkTransform = true
  LinkedObject = -> Link [Fillet.Edge36]
  _LinkVersion = 1
  _Parent = -> Elements
FEATURE [Part::FeaturePython] Element005  label="Axis"  # link proxy (typed FeaturePython)
  Detach = false
  LinkTransform = true
  LinkedObject = -> Link [DatumLine.]
  _LinkVersion = 1
  _Parent = -> Elements
FEATURE [Part::FeaturePython] Assembly001  label="Coupling-Assembly"  # WARN: FeaturePython — macro-defined, semantics opaque (R4)
  AutoRelax = true
  BuildShape = 0
  Freeze = false
  Group = -> [Constraints001,Elements001,Parts001]
  Placement = pos=(0,5.84137e-06,-49) rot=(0,0,1;0rad)
  Verbose = false
  _LinkVersion = 1
  _SolverType = 1
  _Version = 1
FEATURE [App::FeaturePython] Constraints001  # WARN: FeaturePython — macro-defined, semantics opaque (R4)
  Group = -> [Constraint,Constraint001,Constraint002,Constraint003,Constraint005]
  _LinkVersion = 1
  _Version = 1
FEATURE [App::FeaturePython] Elements001  # WARN: FeaturePython — macro-defined, semantics opaque (R4)
  Group = -> [Element006,Element007,_Element,_Element001,_Element002,_Element003,_Element004,_Element005,Element008,Element009]
  _LinkVersion = 1
FEATURE [Part::FeaturePython] Element006  # link proxy (typed FeaturePython)
  Detach = false
  LinkTransform = true
  LinkedObject = -> Link001 [Hole.Sketch008.Edge2]
  Offset = pos=(0,0,3) rot=(0,0,1;0rad)
  Placement = pos=(0,-3,0) rot=(0,0,1;0rad)
  _LinkVersion = 1
  _Parent = -> Elements001
FEATURE [Part::FeaturePython] Element007  # link proxy (typed FeaturePython)
  Detach = false
  LinkTransform = true
  LinkedObject = -> Link001 [Hole.Sketch008.Edge1]
  Offset = pos=(0,0,5) rot=(0,0,1;0rad)
  Placement = pos=(0,-5,1.8e-15) rot=(0,0,1;0rad)
  _LinkVersion = 1
  _Parent = -> Elements001
FEATURE [App::FeaturePython] Constraint  label="Attachment"  # WARN: FeaturePython — macro-defined, semantics opaque (R4)
  Cascade = false
  Disabled = false
  Group = -> [ElementLink,ElementLink001]
  Multiply = false
  _ConstraintType = 45
  _LinkVersion = 1
  _Parent = -> Constraints001
FEATURE [App::FeaturePython] ElementLink  label="_Element"  # link proxy (typed FeaturePython)
  LinkTransform = true
  LinkedObject = -> _Element
  _LinkVersion = 1
  _Parent = -> Constraint
FEATURE [Part::FeaturePython] _Element  # link proxy (typed FeaturePython)
  Detach = false
  LinkTransform = true
  LinkedObject = -> Link001 [Pocket003.Edge106]
  _LinkVersion = 1
  _Parent = -> Elements001
FEATURE [App::FeaturePython] ElementLink001  label="_Element001"  # link proxy (typed FeaturePython)
  LinkTransform = true
  LinkedObject = -> _Element001
  _LinkVersion = 1
  _Parent = -> Constraint
FEATURE [Part::FeaturePython] _Element001  # link proxy (typed FeaturePython)
  Detach = false
  LinkTransform = true
  LinkedObject = -> Screw [Edge9]
  _LinkVersion = 1
  _Parent = -> Elements001
FEATURE [App::FeaturePython] Constraint001  label="Attachment001"  # WARN: FeaturePython — macro-defined, semantics opaque (R4)
  Cascade = false
  Disabled = false
  Group = -> [ElementLink002,ElementLink003]
  Multiply = false
  _ConstraintType = 45
  _LinkVersion = 1
  _Parent = -> Constraints001
FEATURE [App::FeaturePython] ElementLink002  label="_Element002"  # link proxy (typed FeaturePython)
  LinkTransform = true
  LinkedObject = -> _Element002
  _LinkVersion = 1
  _Parent = -> Constraint001
FEATURE [Part::FeaturePython] _Element002  # link proxy (typed FeaturePython)
  Detach = false
  LinkTransform = true
  LinkedObject = -> Link001 [Pocket003.Edge174]
  _LinkVersion = 1
  _Parent = -> Elements001
FEATURE [App::FeaturePython] ElementLink003  label="_Element003"  # link proxy (typed FeaturePython)
  LinkTransform = true
  LinkedObject = -> _Element003
  _LinkVersion = 1
  _Parent = -> Constraint001
FEATURE [Part::FeaturePython] _Element003  # link proxy (typed FeaturePython)
  Detach = false
  LinkTransform = true
  LinkedObject = -> Link003 [Edge9]
  _LinkVersion = 1
  _Parent = -> Elements001
FEATURE [App::FeaturePython] Constraint002  label="Attachment002"  # WARN: FeaturePython — macro-defined, semantics opaque (R4)
  Cascade = false
  Disabled = false
  Group = -> [ElementLink004,ElementLink005]
  Multiply = false
  _ConstraintType = 45
  _LinkVersion = 1
  _Parent = -> Constraints001
FEATURE [App::FeaturePython] ElementLink004  label="Element006"  # link proxy (typed FeaturePython)
  LinkTransform = true
  LinkedObject = -> Element006
  _LinkVersion = 1
  _Parent = -> Constraint002
FEATURE [App::FeaturePython] ElementLink005  label="_Element004"  # link proxy (typed FeaturePython)
  LinkTransform = true
  LinkedObject = -> _Element004
  _LinkVersion = 1
  _Parent = -> Constraint002
FEATURE [Part::FeaturePython] _Element004  # link proxy (typed FeaturePython)
  Detach = false
  LinkTransform = true
  LinkedObject = -> Screw001 [Edge10]
  _LinkVersion = 1
  _Parent = -> Elements001
FEATURE [App::FeaturePython] Constraint003  label="Attachment003"  # WARN: FeaturePython — macro-defined, semantics opaque (R4)
  Cascade = false
  Disabled = false
  Group = -> [ElementLink006,ElementLink007]
  Multiply = false
  _ConstraintType = 45
  _LinkVersion = 1
  _Parent = -> Constraints001
FEATURE [App::FeaturePython] ElementLink006  label="Element007"  # link proxy (typed FeaturePython)
  LinkTransform = true
  LinkedObject = -> Element007
  _LinkVersion = 1
  _Parent = -> Constraint003
FEATURE [App::FeaturePython] ElementLink007  label="_Element005"  # link proxy (typed FeaturePython)
  LinkTransform = true
  LinkedObject = -> _Element005
  _LinkVersion = 1
  _Parent = -> Constraint003
FEATURE [Part::FeaturePython] _Element005  # link proxy (typed FeaturePython)
  Detach = false
  LinkTransform = true
  LinkedObject = -> Link002 [Edge10]
  _LinkVersion = 1
  _Parent = -> Elements001
FEATURE [Part::FeaturePython] Element008  label="motor-mate"  # link proxy (typed FeaturePython)
  Detach = false
  LinkTransform = true
  LinkedObject = -> Link001 [Pocket.Sketch005.]
  Offset = pos=(0,0,-21) rot=(0,0,1;0rad)
  Placement = pos=(0,0,-21) rot=(0,0,1;0rad)
  _LinkVersion = 1
  _Parent = -> Elements001
FEATURE [Part::FeaturePython] Element009  label="screw-mate"  # link proxy (typed FeaturePython)
  Detach = false
  LinkTransform = true
  LinkedObject = -> Link001 [Pocket.Sketch005.]
  Offset = pos=(0,0,-10) rot=(0,0,1;0rad)
  Placement = pos=(0,0,-10) rot=(0,0,1;0rad)
  _LinkVersion = 1
  _Parent = -> Elements001
FEATURE [Part::FeaturePython] Element010  label="coupling-mate"  # link proxy (typed FeaturePython)
  Detach = false
  LinkTransform = true
  LinkedObject = -> Link [Fillet.Edge170]
  _LinkVersion = 1
  _Parent = -> Elements
FEATURE [App::FeaturePython] Constraint004  label="Locked"  # WARN: FeaturePython — macro-defined, semantics opaque (R4)
  Disabled = false
  Group = -> [ElementLink008]
  _ConstraintType = 0
  _LinkVersion = 1
  _Parent = -> Constraints
FEATURE [App::FeaturePython] ElementLink008  label="coupling-mate"  # link proxy (typed FeaturePython)
  LinkTransform = true
  LinkedObject = -> Element010
  _LinkVersion = 1
  _Parent = -> Constraint004
FEATURE [App::FeaturePython] Constraint005  label="Locked001"  # WARN: FeaturePython — macro-defined, semantics opaque (R4)
  Disabled = false
  Group = -> [ElementLink009]
  _ConstraintType = 0
  _LinkVersion = 1
  _Parent = -> Constraints001
FEATURE [App::FeaturePython] ElementLink009  label="motor-mate"  # link proxy (typed FeaturePython)
  LinkTransform = true
  LinkedObject = -> Element008
  _LinkVersion = 1
  _Parent = -> Constraint005
FEATURE [App::FeaturePython] Constraint006  label="Attachment004"  # WARN: FeaturePython — macro-defined, semantics opaque (R4)
  Cascade = false
  Disabled = false
  Group = -> [ElementLink010,ElementLink011]
  Multiply = false
  _ConstraintType = 45
  _LinkVersion = 1
  _Parent = -> Constraints
FEATURE [App::FeaturePython] ElementLink010  label="_Element006"  # link proxy (typed FeaturePython)
  LinkTransform = true
  LinkedObject = -> _Element006
  _LinkVersion = 1
  _Parent = -> Constraint006
FEATURE [Part::FeaturePython] _Element006  # link proxy (typed FeaturePython)
  Detach = false
  LinkTransform = true
  LinkedObject = -> Link004 [0.Edge9]
  _LinkVersion = 1
  _Parent = -> Elements
FEATURE [App::FeaturePython] ElementLink011  label="Element"  # link proxy (typed FeaturePython)
  LinkTransform = true
  LinkedObject = -> Element
  _LinkVersion = 1
  _Parent = -> Constraint006
FEATURE [App::FeaturePython] Constraint007  label="Attachment005"  # WARN: FeaturePython — macro-defined, semantics opaque (R4)
  Cascade = false
  Disabled = false
  Group = -> [ElementLink012,ElementLink013]
  Multiply = false
  _ConstraintType = 45
  _LinkVersion = 1
  _Parent = -> Constraints
FEATURE [App::FeaturePython] ElementLink012  label="_Element007"  # link proxy (typed FeaturePython)
  LinkTransform = true
  LinkedObject = -> _Element007
  _LinkVersion = 1
  _Parent = -> Constraint007
FEATURE [Part::FeaturePython] _Element007  # link proxy (typed FeaturePython)
  Detach = false
  LinkTransform = true
  LinkedObject = -> Link004 [1.Edge9]
  _LinkVersion = 1
  _Parent = -> Elements
FEATURE [App::FeaturePython] ElementLink013  label="Element001"  # link proxy (typed FeaturePython)
  LinkTransform = true
  LinkedObject = -> Element001
  _LinkVersion = 1
  _Parent = -> Constraint007
FEATURE [App::FeaturePython] Constraint008  label="Attachment006"  # WARN: FeaturePython — macro-defined, semantics opaque (R4)
  Cascade = false
  Disabled = false
  Group = -> [ElementLink014,ElementLink015]
  Multiply = false
  _ConstraintType = 45
  _LinkVersion = 1
  _Parent = -> Constraints
FEATURE [App::FeaturePython] ElementLink014  label="_Element008"  # link proxy (typed FeaturePython)
  LinkTransform = true
  LinkedObject = -> _Element008
  _LinkVersion = 1
  _Parent = -> Constraint008
FEATURE [Part::FeaturePython] _Element008  # link proxy (typed FeaturePython)
  Detach = false
  LinkTransform = true
  LinkedObject = -> Link004 [2.Edge9]
  _LinkVersion = 1
  _Parent = -> Elements
FEATURE [App::FeaturePython] ElementLink015  label="Element002"  # link proxy (typed FeaturePython)
  LinkTransform = true
  LinkedObject = -> Element002
  _LinkVersion = 1
  _Parent = -> Constraint008
FEATURE [App::FeaturePython] Constraint009  label="Attachment007"  # WARN: FeaturePython — macro-defined, semantics opaque (R4)
  Cascade = false
  Disabled = false
  Group = -> [ElementLink016,ElementLink017]
  Multiply = false
  _ConstraintType = 45
  _LinkVersion = 1
  _Parent = -> Constraints
FEATURE [App::FeaturePython] ElementLink016  label="_Element009"  # link proxy (typed FeaturePython)
  LinkTransform = true
  LinkedObject = -> _Element009
  _LinkVersion = 1
  _Parent = -> Constraint009
FEATURE [Part::FeaturePython] _Element009  # link proxy (typed FeaturePython)
  Detach = false
  LinkTransform = true
  LinkedObject = -> Link004 [3.Edge9]
  _LinkVersion = 1
  _Parent = -> Elements
FEATURE [App::FeaturePython] ElementLink017  label="Element003"  # link proxy (typed FeaturePython)
  LinkTransform = true
  LinkedObject = -> Element003
  _LinkVersion = 1
  _Parent = -> Constraint009
---- part parts/Table.FCStd = doc fcstd_e150bc7298a9 ----
FCSTD DOCUMENT  (FreeCAD 2021.717R24301 +3842 (Git))
Label: Table
License: Creative Commons Attribution
LicenseURL: http://creativecommons.org/licenses/by/4.0/
objects: App::FeaturePython×83, Part::FeaturePython×58, App::LinkElement×24, Sketcher::SketchObject×2, App::Link×2, PartDesign::Pad×1, PartDesign::Hole×1, PartDesign::Body×1, App::DocumentObjectGroup×1
note: 65 computed .brp shape members not serialized (recipe doc carries the construction recipe); baked Part::Feature solids carry a one-line shape summary decoded from their .brp

FEATURE [Sketcher::SketchObject] Sketch
  FullyConstrained = true
  MapMode = 5
  Support = -> [XY_Plane]
  sketch-geometry (4):
    g0: LineSegment StartX=-224 StartY=415 StartZ=0 EndX=224 EndY=415 EndZ=0
    g1: LineSegment StartX=224 StartY=415 StartZ=0 EndX=224 EndY=-415 EndZ=0
    g2: LineSegment StartX=224 StartY=-415 StartZ=0 EndX=-224 EndY=-415 EndZ=0
    g3: LineSegment StartX=-224 StartY=-415 StartZ=0 EndX=-224 EndY=415 EndZ=0
  constraints (11):
    c: Coincident(g0,g1)
    c: Coincident(g1,g2)
    c: Coincident(g2,g3)
    c: Coincident(g3,g0)
    c: Horizontal(g0)
    c: Horizontal(g2)
    c: Vertical(g1)
    c: Vertical(g3)
    c: Symmetric(g1,g0,g-1)
    c: DistanceX(g0,g0) = 448
    c: DistanceY(g3,g3) = 830
FEATURE [PartDesign::Pad] Pad
  ClaimChildren = false
  Direction = (1,1,1)
  Fit = 0
  FitJoin = 0
  InnerFit = 0
  InnerFitJoin = 0
  InnerTaperAngle = 0
  InnerTaperAngleRev = 0
  Length = 15.7
  Length2 = 100
  Linearize = true
  NewSolid = false
  Profile = -> Sketch
  Refine = true
  Suppress = false
  Type = 0
  _ProfileBasedVersion = 0
FEATURE [Sketcher::SketchObject] Sketch001
  ExternalGeometry = -> [Pad]
  FullyConstrained = false
  MapMode = 5
  Placement = pos=(0,0,15.7) rot=(0,0,1;0rad)
  Support = -> [Pad]
  sketch-geometry (46):
    g0: Circle CenterX=-187.5 CenterY=376.9 CenterZ=0 NormalX=0 NormalY=0 NormalZ=1 AngleXU=0 Radius=2.5
    g1: Circle CenterX=187.5 CenterY=376.9 CenterZ=0 NormalX=0 NormalY=0 NormalZ=1 AngleXU=0 Radius=2.5
    g2: Circle CenterX=-112.5 CenterY=376.9 CenterZ=0 NormalX=0 NormalY=0 NormalZ=1 AngleXU=0 Radius=2.5
    g3: Circle CenterX=-37.5 CenterY=376.9 CenterZ=0 NormalX=0 NormalY=0 NormalZ=1 AngleXU=0 Radius=2.5
    g4: Circle CenterX=37.5 CenterY=376.9 CenterZ=0 NormalX=0 NormalY=0 NormalZ=1 AngleXU=0 Radius=2.5
    g5: Circle CenterX=112.5 CenterY=376.9 CenterZ=0 NormalX=0 NormalY=0 NormalZ=1 AngleXU=0 Radius=2.5
    g6: LineSegment [constr] StartX=-187.5 StartY=376.9 StartZ=0 EndX=-112.5 EndY=376.9 EndZ=0
    g7: LineSegment [constr] StartX=-112.5 StartY=376.9 StartZ=0 EndX=-37.5 EndY=376.9 EndZ=0
    g8: LineSegment [constr] StartX=-37.5 StartY=376.9 StartZ=0 EndX=37.5 EndY=376.9 EndZ=0
    g9: LineSegment [constr] StartX=37.5 StartY=376.9 StartZ=0 EndX=112.5 EndY=376.9 EndZ=0
    g10: LineSegment [constr] StartX=112.5 StartY=376.9 StartZ=0 EndX=187.5 EndY=376.9 EndZ=0
    g11: Circle CenterX=-187.5 CenterY=-376.9 CenterZ=0 NormalX=0 NormalY=0 NormalZ=1 AngleXU=0 Radius=2.5
    g12: Circle CenterX=187.5 CenterY=-376.9 CenterZ=0 NormalX=0 NormalY=0 NormalZ=1 AngleXU=0 Radius=2.5
    g13: Circle CenterX=-112.5 CenterY=-376.9 CenterZ=0 NormalX=0 NormalY=0 NormalZ=1 AngleXU=0 Radius=2.5
    g14: Circle CenterX=-37.5 CenterY=-376.9 CenterZ=0 NormalX=0 NormalY=0 NormalZ=1 AngleXU=0 Radius=2.5
    g15: Circle CenterX=37.5 CenterY=-376.9 CenterZ=0 NormalX=0 NormalY=0 NormalZ=1 AngleXU=0 Radius=2.5
    g16: Circle CenterX=112.5 CenterY=-376.9 CenterZ=0 NormalX=0 NormalY=0 NormalZ=1 AngleXU=0 Radius=2.5
    g17: LineSegment [constr] StartX=-187.5 StartY=-376.9 StartZ=0 EndX=-112.5 EndY=-376.9 EndZ=0
    g18: LineSegment [constr] StartX=-112.5 StartY=-376.9 StartZ=0 EndX=-37.5 EndY=-376.9 EndZ=0
    g19: LineSegment [constr] StartX=-37.5 StartY=-376.9 StartZ=0 EndX=37.5 EndY=-376.9 EndZ=0
    g20: LineSegment [constr] StartX=37.5 StartY=-376.9 StartZ=0 EndX=112.5 EndY=-376.9 EndZ=0
    g21: LineSegment [constr] StartX=112.5 StartY=-376.9 StartZ=0 EndX=187.5 EndY=-376.9 EndZ=0
    g22: Circle CenterX=-187.5 CenterY=117.165 CenterZ=0 NormalX=0 NormalY=0 NormalZ=1 AngleXU=0 Radius=2.5
    g23: Circle CenterX=187.5 CenterY=117.165 CenterZ=0 NormalX=0 NormalY=0 NormalZ=1 AngleXU=0 Radius=2.5
    g24: Circle CenterX=-112.5 CenterY=117.165 CenterZ=0 NormalX=0 NormalY=0 NormalZ=1 AngleXU=0 Radius=2.5
    g25: Circle CenterX=-37.5 CenterY=117.165 CenterZ=0 NormalX=0 NormalY=0 NormalZ=1 AngleXU=0 Radius=2.5
    g26: Circle CenterX=37.5 CenterY=117.165 CenterZ=0 NormalX=0 NormalY=0 NormalZ=1 AngleXU=0 Radius=2.5
    g27: Circle CenterX=112.5 CenterY=117.165 CenterZ=0 NormalX=0 NormalY=0 NormalZ=1 AngleXU=0 Radius=2.5
    g28: LineSegment [constr] StartX=-187.5 StartY=117.165 StartZ=0 EndX=-112.5 EndY=117.165 EndZ=0
    g29: LineSegment [constr] StartX=-112.5 StartY=117.165 StartZ=0 EndX=-37.5 EndY=117.165 EndZ=0
    g30: LineSegment [constr] StartX=-37.5 StartY=117.165 StartZ=0 EndX=37.5 EndY=117.165 EndZ=0
    g31: LineSegment [constr] StartX=37.5 StartY=117.165 StartZ=0 EndX=112.5 EndY=117.165 EndZ=0
    g32: LineSegment [constr] StartX=112.5 StartY=117.165 StartZ=0 EndX=187.5 EndY=117.165 EndZ=0
    g33: Circle CenterX=-187.5 CenterY=-142.57 CenterZ=0 NormalX=0 NormalY=0 NormalZ=1 AngleXU=0 Radius=2.5
    g34: Circle CenterX=187.5 CenterY=-142.57 CenterZ=0 NormalX=0 NormalY=0 NormalZ=1 AngleXU=0 Radius=2.5
    g35: Circle CenterX=-112.5 CenterY=-142.57 CenterZ=0 NormalX=0 NormalY=0 NormalZ=1 AngleXU=0 Radius=2.5
    g36: Circle CenterX=-37.5 CenterY=-142.57 CenterZ=0 NormalX=0 NormalY=0 NormalZ=1 AngleXU=0 Radius=2.5
    g37: Circle CenterX=37.5 CenterY=-142.57 CenterZ=0 NormalX=0 NormalY=0 NormalZ=1 AngleXU=0 Radius=2.5
    g38: Circle CenterX=112.5 CenterY=-142.57 CenterZ=0 NormalX=0 NormalY=0 NormalZ=1 AngleXU=0 Radius=2.5
    g39: LineSegment [constr] StartX=-187.5 StartY=-142.57 StartZ=0 EndX=-112.5 EndY=-142.57 EndZ=0
    g40: LineSegment [constr] StartX=-112.5 StartY=-142.57 StartZ=0 EndX=-37.5 EndY=-142.57 EndZ=0
    g41: LineSegment [constr] StartX=-37.5 StartY=-142.57 StartZ=0 EndX=37.5 EndY=-142.57 EndZ=0
    g42: LineSegment [constr] StartX=37.5 StartY=-142.57 StartZ=0 EndX=112.5 EndY=-142.57 EndZ=0
    g43: LineSegment [constr] StartX=112.5 StartY=-142.57 StartZ=0 EndX=187.5 EndY=-142.57 EndZ=0
    g44: LineSegment [constr] StartX=187.5 StartY=376.9 StartZ=0 EndX=187.5 EndY=117.165 EndZ=0
    g45: LineSegment [constr] StartX=187.5 StartY=-142.57 StartZ=0 EndX=187.5 EndY=117.165 EndZ=0
  constraints (113):
    c: Diameter(g0) = 5
    c: Symmetric(g0,g1,g-2)
    c: Equal(g0,g1)
    c: Horizontal(g5,g4)
    c: Horizontal(g4,g3)
    c: Horizontal(g3,g2)
    c: Horizontal(g2,g1)
    c: Equal(g2,g0)
    c: Equal(g0,g3)
    c: Equal(g3,g4)
    c: Equal(g4,g5)
    c: Coincident(g6,g0)
    c: Coincident(g6,g2)
    c: Coincident(g7,g2)
    c: Coincident(g7,g3)
    c: Coincident(g8,g3)
    c: Coincident(g8,g4)
    c: Coincident(g9,g4)
    c: Coincident(g9,g5)
    c: Coincident(g10,g5)
    c: Coincident(g10,g1)
    c: Equal(g10,g9)
    c: Equal(g9,g8)
    c: Equal(g8,g7)
    c: Equal(g7,g6)
    c: DistanceX(g6,g6) = 75
    c: DistanceY(g0,g-3) = 38.1
    c: Equal(g0,g11) = 5
    c: Equal(g11,g12)
    c: Horizontal(g16,g15)
    c: Horizontal(g15,g14)
    c: Horizontal(g14,g13)
    c: Horizontal(g13,g12)
    c: Equal(g13,g11)
    c: Equal(g11,g14)
    c: Equal(g14,g15)
    c: Equal(g15,g16)
    c: Coincident(g17,g11)
    c: Coincident(g17,g13)
    c: Coincident(g18,g13)
    c: Coincident(g18,g14)
    c: Coincident(g19,g14)
    c: Coincident(g19,g15)
    c: Coincident(g20,g15)
    c: Coincident(g20,g16)
    c: Coincident(g21,g16)
    c: Coincident(g21,g12)
    c: Equal(g21,g20)
    c: Equal(g20,g19)
    c: Equal(g19,g18)
    c: Equal(g18,g17)
    c: Equal(g0,g22) = 5
    c: Equal(g22,g23)
    c: Horizontal(g27,g26)
    c: Horizontal(g26,g25)
    c: Horizontal(g25,g24)
    c: Horizontal(g24,g23)
    c: Equal(g24,g22)
    c: Equal(g22,g25)
    c: Equal(g25,g26)
    c: Equal(g26,g27)
    c: Coincident(g28,g22)
    c: Coincident(g28,g24)
    c: Coincident(g29,g24)
    c: Coincident(g29,g25)
    c: Coincident(g30,g25)
    c: Coincident(g30,g26)
    c: Coincident(g31,g26)
    c: Coincident(g31,g27)
    c: Coincident(g32,g27)
    c: Coincident(g32,g23)
    c: Equal(g32,g31)
    c: Equal(g31,g30)
    c: Equal(g30,g29)
    c: Equal(g29,g28)
    c: Equal(g6,g28) = 75
    c: Equal(g33,g34)
    c: Horizontal(g38,g37)
    c: Horizontal(g37,g36)
    c: Horizontal(g36,g35)
    c: Horizontal(g35,g34)
    c: Equal(g35,g33)
    c: Equal(g33,g36)
    c: Equal(g36,g37)
    c: Equal(g37,g38)
    c: Coincident(g39,g33)
    c: Coincident(g39,g35)
    c: Coincident(g40,g35)
    c: Coincident(g40,g36)
    c: Coincident(g41,g36)
    c: Coincident(g41,g37)
    c: Coincident(g42,g37)
    c: Coincident(g42,g38)
    c: Coincident(g43,g38)
    c: Coincident(g43,g34)
    c: Equal(g43,g42)
    c: Equal(g42,g41)
    c: Equal(g41,g40)
    c: Equal(g40,g39)
    c: Vertical(g11,g33)
    c: Vertical(g33,g22)
    c: Symmetric(g11,g0,g-1)
    c: Horizontal(g39)
    c: Horizontal(g28)
    c: DistanceY(g34,g1) = 519.47
    c: Coincident(g44,g1)
    c: Coincident(g44,g23)
    c: Coincident(g45,g34)
    c: Coincident(g45,g23)
    c: Vertical(g45)
    c: Symmetric(g12,g11,g-2)
    c: Equal(g45,g44)
    c: DistanceX(g-3,g0) = 36.5
FEATURE [App::Link] Link001  label="Link001(Table plate PP)"
  AutoLinkLabel = true
  AutoPlacement = true
  LinkedObject = -> Body
  SyncGroupVisibility = false
  _LinkVersion = 1
FEATURE [PartDesign::Hole] Hole
  BaseFeature = -> Pad
  ClaimChildren = false
  CustomThreadClearance = 0
  Depth = 25
  DepthType = 0
  Diameter = 5
  DrillForDepth = false
  DrillPoint = 1
  DrillPointAngle = 118
  Fit = 0
  FitJoin = 0
  HoleCutCountersinkAngle = 90
  HoleCutCustomValues = false
  HoleCutDepth = 5
  HoleCutDiameter = 15
  HoleCutType = 1
  InnerFit = 0
  InnerFitJoin = 0
  ModelThread = false
  NewSolid = false
  Profile = -> Sketch001
  Refine = true
  Suppress = false
  Tapered = false
  TaperedAngle = 90
  ThreadClass = 0
  ThreadDepth = 23.5
  ThreadDepthType = 0
  ThreadDirection = 0
  ThreadFit = 0
  ThreadSize = 0
  ThreadType = 0
  Threaded = false
  UseCustomThreadClearance = false
  _ProfileBasedVersion = 0
FEATURE [PartDesign::Body] Body  label="Table plate PP"
  AutoGroupSolids = false
  ExportMode = 0
  Group = -> [Sketch,Pad,Sketch001,Hole]
  Origin = -> Origin
  Tip = -> Hole
  _ExportChildren = -> [Pad,Hole]
  _GroupVersion = 1
FEATURE [Part::FeaturePython] Screw  label="#10x3/4in-Screw"  # Fasteners workbench fastener (typed FeaturePython)
  Placement = pos=(0,0,47) rot=(0,0,1;0rad)
  diameter = 9
  invert = false
  length = 5
  lengthCustom = 19.05
  matchOuter = false
  offset = 0
  thread = false
  type = 4
FEATURE [Part::FeaturePython] Washer  label="#10-Washer"  # Fasteners workbench fastener (typed FeaturePython)
  Placement = pos=(0,0,45.984) rot=(0,0,1;0rad)
  diameter = 9
  invert = false
  matchOuter = false
  offset = 0
  type = 1
FEATURE [Part::FeaturePython] Parts001  # WARN: FeaturePython — macro-defined, semantics opaque (R4)
  Group = -> [Screw,Washer]
  GroupMode = 0
  _LinkVersion = 1
FEATURE [App::LinkElement] Link_i0
  LinkPlacement = pos=(-187.5,-376.9,-35.284) rot=(0,0,1;0rad)
  LinkedObject = -> Assembly001
  Placement = pos=(-187.5,-376.9,-35.284) rot=(0,0,1;0rad)
  _LinkVersion = 1
FEATURE [App::LinkElement] Link_i1
  LinkPlacement = pos=(-112.5,-376.9,-35.284) rot=(0,0,1;0rad)
  LinkedObject = -> Assembly001
  Placement = pos=(-112.5,-376.9,-35.284) rot=(0,0,1;0rad)
  _LinkVersion = 1
FEATURE [App::LinkElement] Link_i2
  LinkPlacement = pos=(-37.5,-376.9,-35.284) rot=(0,0,1;0rad)
  LinkedObject = -> Assembly001
  Placement = pos=(-37.5,-376.9,-35.284) rot=(0,0,1;0rad)
  _LinkVersion = 1
FEATURE [App::LinkElement] Link_i3
  LinkPlacement = pos=(37.5,-376.9,-35.284) rot=(0,0,1;0rad)
  LinkedObject = -> Assembly001
  Placement = pos=(37.5,-376.9,-35.284) rot=(0,0,1;0rad)
  _LinkVersion = 1
FEATURE [App::LinkElement] Link_i4
  LinkPlacement = pos=(112.5,-376.9,-35.284) rot=(0,0,1;0rad)
  LinkedObject = -> Assembly001
  Placement = pos=(112.5,-376.9,-35.284) rot=(0,0,1;0rad)
  _LinkVersion = 1
FEATURE [App::LinkElement] Link_i5
  LinkPlacement = pos=(187.5,-376.9,-35.284) rot=(0,0,1;0rad)
  LinkedObject = -> Assembly001
  Placement = pos=(187.5,-376.9,-35.284) rot=(0,0,1;0rad)
  _LinkVersion = 1
FEATURE [App::LinkElement] Link_i6
  LinkPlacement = pos=(-187.5,-142.57,-35.284) rot=(0,0,1;0rad)
  LinkedObject = -> Assembly001
  Placement = pos=(-187.5,-142.57,-35.284) rot=(0,0,1;0rad)
  _LinkVersion = 1
FEATURE [App::LinkElement] Link_i7
  LinkPlacement = pos=(-112.5,-142.57,-35.284) rot=(0,0,1;0rad)
  LinkedObject = -> Assembly001
  Placement = pos=(-112.5,-142.57,-35.284) rot=(0,0,1;0rad)
  _LinkVersion = 1
FEATURE [App::LinkElement] Link_i8
  LinkPlacement = pos=(-37.5,-142.57,-35.284) rot=(0,0,1;0rad)
  LinkedObject = -> Assembly001
  Placement = pos=(-37.5,-142.57,-35.284) rot=(0,0,1;0rad)
  _LinkVersion = 1
FEATURE [App::LinkElement] Link_i9
  LinkPlacement = pos=(37.5,-142.57,-35.284) rot=(0,0,1;0rad)
  LinkedObject = -> Assembly001
  Placement = pos=(37.5,-142.57,-35.284) rot=(0,0,1;0rad)
  _LinkVersion = 1
FEATURE [App::LinkElement] Link_i10
  LinkPlacement = pos=(112.5,-142.57,-35.284) rot=(0,0,1;0rad)
  LinkedObject = -> Assembly001
  Placement = pos=(112.5,-142.57,-35.284) rot=(0,0,1;0rad)
  _LinkVersion = 1
FEATURE [App::LinkElement] Link_i11
  LinkPlacement = pos=(187.5,-142.57,-35.284) rot=(0,0,1;0rad)
  LinkedObject = -> Assembly001
  Placement = pos=(187.5,-142.57,-35.284) rot=(0,0,1;0rad)
  _LinkVersion = 1
FEATURE [App::LinkElement] Link_i12
  LinkPlacement = pos=(-187.5,117.165,-35.284) rot=(0,0,1;0rad)
  LinkedObject = -> Assembly001
  Placement = pos=(-187.5,117.165,-35.284) rot=(0,0,1;0rad)
  _LinkVersion = 1
FEATURE [App::LinkElement] Link_i13
  LinkPlacement = pos=(-112.5,117.165,-35.284) rot=(0,0,1;0rad)
  LinkedObject = -> Assembly001
  Placement = pos=(-112.5,117.165,-35.284) rot=(0,0,1;0rad)
  _LinkVersion = 1
FEATURE [App::LinkElement] Link_i14
  LinkPlacement = pos=(-37.5,117.165,-35.284) rot=(0,0,1;0rad)
  LinkedObject = -> Assembly001
  Placement = pos=(-37.5,117.165,-35.284) rot=(0,0,1;0rad)
  _LinkVersion = 1
FEATURE [App::LinkElement] Link_i15
  LinkPlacement = pos=(37.5,117.165,-35.284) rot=(0,0,1;0rad)
  LinkedObject = -> Assembly001
  Placement = pos=(37.5,117.165,-35.284) rot=(0,0,1;0rad)
  _LinkVersion = 1
FEATURE [App::LinkElement] Link_i16
  LinkPlacement = pos=(112.5,117.165,-35.284) rot=(0,0,1;0rad)
  LinkedObject = -> Assembly001
  Placement = pos=(112.5,117.165,-35.284) rot=(0,0,1;0rad)
  _LinkVersion = 1
FEATURE [App::LinkElement] Link_i17
  LinkPlacement = pos=(187.5,117.165,-35.284) rot=(0,0,1;0rad)
  LinkedObject = -> Assembly001
  Placement = pos=(187.5,117.165,-35.284) rot=(0,0,1;0rad)
  _LinkVersion = 1
FEATURE [App::LinkElement] Link_i18
  LinkPlacement = pos=(-187.5,376.9,-35.284) rot=(0,0,1;0rad)
  LinkedObject = -> Assembly001
  Placement = pos=(-187.5,376.9,-35.284) rot=(0,0,1;0rad)
  _LinkVersion = 1
FEATURE [App::LinkElement] Link_i19
  LinkPlacement = pos=(-112.5,376.9,-35.284) rot=(0,0,1;0rad)
  LinkedObject = -> Assembly001
  Placement = pos=(-112.5,376.9,-35.284) rot=(0,0,1;0rad)
  _LinkVersion = 1
FEATURE [App::LinkElement] Link_i20
  LinkPlacement = pos=(-37.5,376.9,-35.284) rot=(0,0,1;0rad)
  LinkedObject = -> Assembly001
  Placement = pos=(-37.5,376.9,-35.284) rot=(0,0,1;0rad)
  _LinkVersion = 1
FEATURE [App::LinkElement] Link_i21
  LinkPlacement = pos=(37.5,376.9,-35.284) rot=(0,0,1;0rad)
  LinkedObject = -> Assembly001
  Placement = pos=(37.5,376.9,-35.284) rot=(0,0,1;0rad)
  _LinkVersion = 1
FEATURE [App::LinkElement] Link_i22
  LinkPlacement = pos=(112.5,376.9,-35.284) rot=(0,0,1;0rad)
  LinkedObject = -> Assembly001
  Placement = pos=(112.5,376.9,-35.284) rot=(0,0,1;0rad)
  _LinkVersion = 1
FEATURE [App::LinkElement] Link_i23
  LinkPlacement = pos=(187.5,376.9,-35.284) rot=(0,0,1;0rad)
  LinkedObject = -> Assembly001
  Placement = pos=(187.5,376.9,-35.284) rot=(0,0,1;0rad)
  _LinkVersion = 1
FEATURE [App::Link] Link  label="10x3/4 screw and washer 24 ct"
  AutoLinkLabel = true
  AutoPlacement = true
  ElementCount = 24
  ElementList = -> [Link_i0,Link_i1,Link_i2,Link_i3,Link_i4,Link_i5,Link_i6,Link_i7,Link_i8,Link_i9,Link_i10,Link_i11,Link_i12,Link_i13,Link_i14,Link_i15,Link_i16,Link_i17,Link_i18,Link_i19,Link_i20,Link_i21,Link_i22,Link_i23]
  LinkedObject = -> Assembly001
  SyncGroupVisibility = false
  _LinkVersion = 1
FEATURE [Part::FeaturePython] Parts  # WARN: FeaturePython — macro-defined, semantics opaque (R4)
  Group = -> [Link001,Link]
  GroupMode = 0
  _LinkVersion = 1
FEATURE [Part::FeaturePython] Assembly  label="PP Table Assembly"  # WARN: FeaturePython — macro-defined, semantics opaque (R4)
  AutoRelax = true
  BuildShape = 0
  Freeze = false
  Group = -> [Constraints,Elements,Parts]
  Verbose = false
  _LinkVersion = 1
  _SolverType = 1
  _Version = 1
FEATURE [App::FeaturePython] Constraints  # WARN: FeaturePython — macro-defined, semantics opaque (R4)
  Group = -> [Constraint,Constraint003,Constraint004,Constraint005,Constraint006,Constraint007,Constraint008,Constraint009,Constraint010,Constraint011,Constraint012,Constraint013,Constraint014,Constraint015,Constraint016,Constraint017,Constraint018,Constraint019,Constraint020,Constraint021,Constraint022,Constraint023,Constraint024,Constraint025,Constraint026]
  _LinkVersion = 1
  _Version = 1
FEATURE [App::FeaturePython] Elements  # WARN: FeaturePython — macro-defined, semantics opaque (R4)
  Group = -> [Element,_Element002,_Element003,_Element004,_Element005,_Element006,_Element007,_Element008,_Element009,_Element010,_Element011,_Element012,_Element013,_Element014,_Element015,_Element016,_Element017,_Element018,_Element019,_Element020,_Element021,_Element022,_Element023,_Element024,_Element025,_Element026,_Element027,_Element028,_Element029,_Element030,_Element031,_Element032,_Element033,+16 more]
  _LinkVersion = 1
FEATURE [Part::FeaturePython] Element  label="frame mate"  # link proxy (typed FeaturePython)
  Detach = false
  LinkTransform = true
  LinkedObject = -> Link001 [Hole.Edge12]
  _LinkVersion = 1
  _Parent = -> Elements
FEATURE [App::FeaturePython] Constraint  label="Locked"  # WARN: FeaturePython — macro-defined, semantics opaque (R4)
  Disabled = false
  Group = -> [ElementLink]
  _ConstraintType = 0
  _LinkVersion = 1
  _Parent = -> Constraints
FEATURE [App::FeaturePython] ElementLink  label="frame mate"  # link proxy (typed FeaturePython)
  LinkTransform = true
  LinkedObject = -> Element
  _LinkVersion = 1
  _Parent = -> Constraint
FEATURE [App::DocumentObjectGroup] Group  label="Components"
  ExportMode = 1
  Group = -> [Body,Assembly001]
  _GroupVersion = 1
FEATURE [Part::FeaturePython] Assembly001  label="10x3/4 screw and washer Assembly"  # WARN: FeaturePython — macro-defined, semantics opaque (R4)
  AutoRelax = true
  BuildShape = 0
  Freeze = false
  Group = -> [Constraints001,Elements001,Parts001]
  Verbose = false
  _LinkVersion = 1
  _SolverType = 1
  _Version = 1
FEATURE [App::FeaturePython] Constraints001  # WARN: FeaturePython — macro-defined, semantics opaque (R4)
  Group = -> [Constraint001,Constraint002]
  _LinkVersion = 1
  _Version = 1
FEATURE [App::FeaturePython] Elements001  # WARN: FeaturePython — macro-defined, semantics opaque (R4)
  Group = -> [_Element,_Element001,Element001]
  _LinkVersion = 1
FEATURE [App::FeaturePython] Constraint001  label="Locked001"  # WARN: FeaturePython — macro-defined, semantics opaque (R4)
  Disabled = false
  Group = -> [ElementLink001]
  _ConstraintType = 0
  _LinkVersion = 1
  _Parent = -> Constraints001
FEATURE [App::FeaturePython] ElementLink001  label="_Element"  # link proxy (typed FeaturePython)
  LinkTransform = true
  LinkedObject = -> _Element
  _LinkVersion = 1
  _Parent = -> Constraint001
FEATURE [Part::FeaturePython] _Element  # link proxy (typed FeaturePython)
  Detach = false
  LinkTransform = true
  LinkedObject = -> Screw [Edge4]
  _LinkVersion = 1
  _Parent = -> Elements001
FEATURE [App::FeaturePython] Constraint002  label="Attachment"  # WARN: FeaturePython — macro-defined, semantics opaque (R4)
  Cascade = false
  Disabled = false
  Group = -> [ElementLink002,ElementLink003]
  Multiply = false
  _ConstraintType = 45
  _LinkVersion = 1
  _Parent = -> Constraints001
FEATURE [App::FeaturePython] ElementLink002  label="_Element001"  # link proxy (typed FeaturePython)
  LinkTransform = true
  LinkedObject = -> _Element001
  _LinkVersion = 1
  _Parent = -> Constraint002
FEATURE [Part::FeaturePython] _Element001  # link proxy (typed FeaturePython)
  Detach = false
  LinkTransform = true
  LinkedObject = -> Washer [Edge1]
  _LinkVersion = 1
  _Parent = -> Elements001
FEATURE [App::FeaturePython] ElementLink003  label="_Element"  # link proxy (typed FeaturePython)
  LinkTransform = true
  LinkedObject = -> _Element
  _LinkVersion = 1
  _Parent = -> Constraint002
FEATURE [Part::FeaturePython] Element001  label="mate"  # link proxy (typed FeaturePython)
  Detach = false
  LinkTransform = true
  LinkedObject = -> Washer [Edge5]
  _LinkVersion = 1
  _Parent = -> Elements001
FEATURE [App::FeaturePython] Constraint003  label="Attachment001"  # WARN: FeaturePython — macro-defined, semantics opaque (R4)
  Cascade = false
  Disabled = false
  Group = -> [ElementLink004,ElementLink005]
  Multiply = false
  _ConstraintType = 45
  _LinkVersion = 1
  _Parent = -> Constraints
FEATURE [App::FeaturePython] ElementLink004  label="_Element002"  # link proxy (typed FeaturePython)
  LinkTransform = true
  LinkedObject = -> _Element002
  _LinkVersion = 1
  _Parent = -> Constraint003
FEATURE [Part::FeaturePython] _Element002  # link proxy (typed FeaturePython)
  Detach = false
  LinkTransform = true
  LinkedObject = -> Link [Link_i0.1.$mate.]
  _LinkVersion = 1
  _Parent = -> Elements
FEATURE [App::FeaturePython] ElementLink005  label="_Element003"  # link proxy (typed FeaturePython)
  LinkTransform = true
  LinkedObject = -> _Element003
  _LinkVersion = 1
  _Parent = -> Constraint003
FEATURE [Part::FeaturePython] _Element003  # link proxy (typed FeaturePython)
  Detach = false
  LinkTransform = true
  LinkedObject = -> Link001 [Hole.Edge109]
  _LinkVersion = 1
  _Parent = -> Elements
FEATURE [App::FeaturePython] Constraint004  label="Attachment002"  # WARN: FeaturePython — macro-defined, semantics opaque (R4)
  Cascade = false
  Disabled = false
  Group = -> [ElementLink006,ElementLink007]
  Multiply = false
  _ConstraintType = 45
  _LinkVersion = 1
  _Parent = -> Constraints
FEATURE [App::FeaturePython] ElementLink006  label="_Element004"  # link proxy (typed FeaturePython)
  LinkTransform = true
  LinkedObject = -> _Element004
  _LinkVersion = 1
  _Parent = -> Constraint004
FEATURE [Part::FeaturePython] _Element004  # link proxy (typed FeaturePython)
  Detach = false
  LinkTransform = true
  LinkedObject = -> Link [Link_i1.1.$mate.]
  _LinkVersion = 1
  _Parent = -> Elements
FEATURE [App::FeaturePython] ElementLink007  label="_Element005"  # link proxy (typed FeaturePython)
  LinkTransform = true
  LinkedObject = -> _Element005
  _LinkVersion = 1
  _Parent = -> Constraint004
FEATURE [Part::FeaturePython] _Element005  # link proxy (typed FeaturePython)
  Detach = false
  LinkTransform = true
  LinkedObject = -> Link001 [Hole.Edge111]
  _LinkVersion = 1
  _Parent = -> Elements
FEATURE [App::FeaturePython] Constraint005  label="Attachment003"  # WARN: FeaturePython — macro-defined, semantics opaque (R4)
  Cascade = false
  Disabled = false
  Group = -> [ElementLink008,ElementLink009]
  Multiply = false
  _ConstraintType = 45
  _LinkVersion = 1
  _Parent = -> Constraints
FEATURE [App::FeaturePython] ElementLink008  label="_Element006"  # link proxy (typed FeaturePython)
  LinkTransform = true
  LinkedObject = -> _Element006
  _LinkVersion = 1
  _Parent = -> Constraint005
FEATURE [Part::FeaturePython] _Element006  # link proxy (typed FeaturePython)
  Detach = false
  LinkTransform = true
  LinkedObject = -> Link [Link_i2.1.$mate.]
  _LinkVersion = 1
  _Parent = -> Elements
FEATURE [App::FeaturePython] ElementLink009  label="_Element007"  # link proxy (typed FeaturePython)
  LinkTransform = true
  LinkedObject = -> _Element007
  _LinkVersion = 1
  _Parent = -> Constraint005
FEATURE [Part::FeaturePython] _Element007  # link proxy (typed FeaturePython)
  Detach = false
  LinkTransform = true
  LinkedObject = -> Link001 [Hole.Edge113]
  _LinkVersion = 1
  _Parent = -> Elements
FEATURE [App::FeaturePython] Constraint006  label="Attachment004"  # WARN: FeaturePython — macro-defined, semantics opaque (R4)
  Cascade = false
  Disabled = false
  Group = -> [ElementLink010,ElementLink011]
  Multiply = false
  _ConstraintType = 45
  _LinkVersion = 1
  _Parent = -> Constraints
FEATURE [App::FeaturePython] ElementLink010  label="_Element008"  # link proxy (typed FeaturePython)
  LinkTransform = true
  LinkedObject = -> _Element008
  _LinkVersion = 1
  _Parent = -> Constraint006
FEATURE [Part::FeaturePython] _Element008  # link proxy (typed FeaturePython)
  Detach = false
  LinkTransform = true
  LinkedObject = -> Link [Link_i3.1.$mate.]
  _LinkVersion = 1
  _Parent = -> Elements
FEATURE [App::FeaturePython] ElementLink011  label="_Element009"  # link proxy (typed FeaturePython)
  LinkTransform = true
  LinkedObject = -> _Element009
  _LinkVersion = 1
  _Parent = -> Constraint006
FEATURE [Part::FeaturePython] _Element009  # link proxy (typed FeaturePython)
  Detach = false
  LinkTransform = true
  LinkedObject = -> Link001 [Hole.Edge121]
  _LinkVersion = 1
  _Parent = -> Elements
FEATURE [App::FeaturePython] Constraint007  label="Attachment005"  # WARN: FeaturePython — macro-defined, semantics opaque (R4)
  Cascade = false
  Disabled = false
  Group = -> [ElementLink012,ElementLink013]
  Multiply = false
  _ConstraintType = 45
  _LinkVersion = 1
  _Parent = -> Constraints
FEATURE [App::FeaturePython] ElementLink012  label="_Element010"  # link proxy (typed FeaturePython)
  LinkTransform = true
  LinkedObject = -> _Element010
  _LinkVersion = 1
  _Parent = -> Constraint007
FEATURE [Part::FeaturePython] _Element010  # link proxy (typed FeaturePython)
  Detach = false
  LinkTransform = true
  LinkedObject = -> Link [Link_i4.1.$mate.]
  _LinkVersion = 1
  _Parent = -> Elements
FEATURE [App::FeaturePython] ElementLink013  label="_Element011"  # link proxy (typed FeaturePython)
  LinkTransform = true
  LinkedObject = -> _Element011
  _LinkVersion = 1
  _Parent = -> Constraint007
FEATURE [Part::FeaturePython] _Element011  # link proxy (typed FeaturePython)
  Detach = false
  LinkTransform = true
  LinkedObject = -> Link001 [Hole.Edge123]
  _LinkVersion = 1
  _Parent = -> Elements
FEATURE [App::FeaturePython] Constraint008  label="Attachment006"  # WARN: FeaturePython — macro-defined, semantics opaque (R4)
  Cascade = false
  Disabled = false
  Group = -> [ElementLink014,ElementLink015]
  Multiply = false
  _ConstraintType = 45
  _LinkVersion = 1
  _Parent = -> Constraints
FEATURE [App::FeaturePython] ElementLink014  label="_Element012"  # link proxy (typed FeaturePython)
  LinkTransform = true
  LinkedObject = -> _Element012
  _LinkVersion = 1
  _Parent = -> Constraint008
FEATURE [Part::FeaturePython] _Element012  # link proxy (typed FeaturePython)
  Detach = false
  LinkTransform = true
  LinkedObject = -> Link [Link_i5.1.$mate.]
  _LinkVersion = 1
  _Parent = -> Elements
FEATURE [App::FeaturePython] ElementLink015  label="_Element013"  # link proxy (typed FeaturePython)
  LinkTransform = true
  LinkedObject = -> _Element013
  _LinkVersion = 1
  _Parent = -> Constraint008
FEATURE [Part::FeaturePython] _Element013  # link proxy (typed FeaturePython)
  Detach = false
  LinkTransform = true
  LinkedObject = -> Link001 [Hole.Edge125]
  _LinkVersion = 1
  _Parent = -> Elements
FEATURE [App::FeaturePython] Constraint009  label="Attachment007"  # WARN: FeaturePython — macro-defined, semantics opaque (R4)
  Cascade = false
  Disabled = false
  Group = -> [ElementLink016,ElementLink017]
  Multiply = false
  _ConstraintType = 45
  _LinkVersion = 1
  _Parent = -> Constraints
FEATURE [App::FeaturePython] ElementLink016  label="_Element014"  # link proxy (typed FeaturePython)
  LinkTransform = true
  LinkedObject = -> _Element014
  _LinkVersion = 1
  _Parent = -> Constraint009
FEATURE [Part::FeaturePython] _Element014  # link proxy (typed FeaturePython)
  Detach = false
  LinkTransform = true
  LinkedObject = -> Link [Link_i6.1.$mate.]
  _LinkVersion = 1
  _Parent = -> Elements
FEATURE [App::FeaturePython] ElementLink017  label="_Element015"  # link proxy (typed FeaturePython)
  LinkTransform = true
  LinkedObject = -> _Element015
  _LinkVersion = 1
  _Parent = -> Constraint009
FEATURE [Part::FeaturePython] _Element015  # link proxy (typed FeaturePython)
  Detach = false
  LinkTransform = true
  LinkedObject = -> Link001 [Hole.Edge115]
  _LinkVersion = 1
  _Parent = -> Elements
FEATURE [App::FeaturePython] Constraint010  label="Attachment008"  # WARN: FeaturePython — macro-defined, semantics opaque (R4)
  Cascade = false
  Disabled = false
  Group = -> [ElementLink018,ElementLink019]
  Multiply = false
  _ConstraintType = 45
  _LinkVersion = 1
  _Parent = -> Constraints
FEATURE [App::FeaturePython] ElementLink018  label="_Element016"  # link proxy (typed FeaturePython)
  LinkTransform = true
  LinkedObject = -> _Element016
  _LinkVersion = 1
  _Parent = -> Constraint010
FEATURE [Part::FeaturePython] _Element016  # link proxy (typed FeaturePython)
  Detach = false
  LinkTransform = true
  LinkedObject = -> Link [Link_i7.1.$mate.]
  _LinkVersion = 1
  _Parent = -> Elements
FEATURE [App::FeaturePython] ElementLink019  label="_Element017"  # link proxy (typed FeaturePython)
  LinkTransform = true
  LinkedObject = -> _Element017
  _LinkVersion = 1
  _Parent = -> Constraint010
FEATURE [Part::FeaturePython] _Element017  # link proxy (typed FeaturePython)
  Detach = false
  LinkTransform = true
  LinkedObject = -> Link001 [Hole.Edge117]
  _LinkVersion = 1
  _Parent = -> Elements
FEATURE [App::FeaturePython] Constraint011  label="Attachment009"  # WARN: FeaturePython — macro-defined, semantics opaque (R4)
  Cascade = false
  Disabled = false
  Group = -> [ElementLink020,ElementLink021]
  Multiply = false
  _ConstraintType = 45
  _LinkVersion = 1
  _Parent = -> Constraints
FEATURE [App::FeaturePython] ElementLink020  label="_Element018"  # link proxy (typed FeaturePython)
  LinkTransform = true
  LinkedObject = -> _Element018
  _LinkVersion = 1
  _Parent = -> Constraint011
FEATURE [Part::FeaturePython] _Element018  # link proxy (typed FeaturePython)
  Detach = false
  LinkTransform = true
  LinkedObject = -> Link [Link_i8.1.$mate.]
  _LinkVersion = 1
  _Parent = -> Elements
FEATURE [App::FeaturePython] ElementLink021  label="_Element019"  # link proxy (typed FeaturePython)
  LinkTransform = true
  LinkedObject = -> _Element019
  _LinkVersion = 1
  _Parent = -> Constraint011
FEATURE [Part::FeaturePython] _Element019  # link proxy (typed FeaturePython)
  Detach = false
  LinkTransform = true
  LinkedObject = -> Link001 [Hole.Edge119]
  _LinkVersion = 1
  _Parent = -> Elements
FEATURE [App::FeaturePython] Constraint012  label="Attachment010"  # WARN: FeaturePython — macro-defined, semantics opaque (R4)
  Cascade = false
  Disabled = false
  Group = -> [ElementLink022,ElementLink023]
  Multiply = false
  _ConstraintType = 45
  _LinkVersion = 1
  _Parent = -> Constraints
FEATURE [App::FeaturePython] ElementLink022  label="_Element020"  # link proxy (typed FeaturePython)
  LinkTransform = true
  LinkedObject = -> _Element020
  _LinkVersion = 1
  _Parent = -> Constraint012
FEATURE [Part::FeaturePython] _Element020  # link proxy (typed FeaturePython)
  Detach = false
  LinkTransform = true
  LinkedObject = -> Link001 [Hole.Edge127]
  _LinkVersion = 1
  _Parent = -> Elements
FEATURE [App::FeaturePython] ElementLink023  label="_Element021"  # link proxy (typed FeaturePython)
  LinkTransform = true
  LinkedObject = -> _Element021
  _LinkVersion = 1
  _Parent = -> Constraint012
FEATURE [Part::FeaturePython] _Element021  # link proxy (typed FeaturePython)
  Detach = false
  LinkTransform = true
  LinkedObject = -> Link [Link_i9.1.$mate.]
  _LinkVersion = 1
  _Parent = -> Elements
FEATURE [App::FeaturePython] Constraint013  label="Attachment011"  # WARN: FeaturePython — macro-defined, semantics opaque (R4)
  Cascade = false
  Disabled = false
  Group = -> [ElementLink024,ElementLink025]
  Multiply = false
  _ConstraintType = 45
  _LinkVersion = 1
  _Parent = -> Constraints
FEATURE [App::FeaturePython] ElementLink024  label="_Element022"  # link proxy (typed FeaturePython)
  LinkTransform = true
  LinkedObject = -> _Element022
  _LinkVersion = 1
  _Parent = -> Constraint013
FEATURE [Part::FeaturePython] _Element022  # link proxy (typed FeaturePython)
  Detach = false
  LinkTransform = true
  LinkedObject = -> Link001 [Hole.Edge129]
  _LinkVersion = 1
  _Parent = -> Elements
FEATURE [App::FeaturePython] ElementLink025  label="_Element023"  # link proxy (typed FeaturePython)
  LinkTransform = true
  LinkedObject = -> _Element023
  _LinkVersion = 1
  _Parent = -> Constraint013
FEATURE [Part::FeaturePython] _Element023  # link proxy (typed FeaturePython)
  Detach = false
  LinkTransform = true
  LinkedObject = -> Link [Link_i10.1.$mate.]
  _LinkVersion = 1
  _Parent = -> Elements
FEATURE [App::FeaturePython] Constraint014  label="Attachment012"  # WARN: FeaturePython — macro-defined, semantics opaque (R4)
  Cascade = false
  Disabled = false
  Group = -> [ElementLink026,ElementLink027]
  Multiply = false
  _ConstraintType = 45
  _LinkVersion = 1
  _Parent = -> Constraints
FEATURE [App::FeaturePython] ElementLink026  label="_Element024"  # link proxy (typed FeaturePython)
  LinkTransform = true
  LinkedObject = -> _Element024
  _LinkVersion = 1
  _Parent = -> Constraint014
FEATURE [Part::FeaturePython] _Element024  # link proxy (typed FeaturePython)
  Detach = false
  LinkTransform = true
  LinkedObject = -> Link001 [Hole.Edge131]
  _LinkVersion = 1
  _Parent = -> Elements
FEATURE [App::FeaturePython] ElementLink027  label="_Element025"  # link proxy (typed FeaturePython)
  LinkTransform = true
  LinkedObject = -> _Element025
  _LinkVersion = 1
  _Parent = -> Constraint014
FEATURE [Part::FeaturePython] _Element025  # link proxy (typed FeaturePython)
  Detach = false
  LinkTransform = true
  LinkedObject = -> Link [Link_i11.1.$mate.]
  _LinkVersion = 1
  _Parent = -> Elements
FEATURE [App::FeaturePython] Constraint015  label="Attachment013"  # WARN: FeaturePython — macro-defined, semantics opaque (R4)
  Cascade = false
  Disabled = false
  Group = -> [ElementLink028,ElementLink029]
  Multiply = false
  _ConstraintType = 45
  _LinkVersion = 1
  _Parent = -> Constraints
FEATURE [App::FeaturePython] ElementLink028  label="_Element026"  # link proxy (typed FeaturePython)
  LinkTransform = true
  LinkedObject = -> _Element026
  _LinkVersion = 1
  _Parent = -> Constraint015
FEATURE [Part::FeaturePython] _Element026  # link proxy (typed FeaturePython)
  Detach = false
  LinkTransform = true
  LinkedObject = -> Link001 [Hole.Edge133]
  _LinkVersion = 1
  _Parent = -> Elements
FEATURE [App::FeaturePython] ElementLink029  label="_Element027"  # link proxy (typed FeaturePython)
  LinkTransform = true
  LinkedObject = -> _Element027
  _LinkVersion = 1
  _Parent = -> Constraint015
FEATURE [Part::FeaturePython] _Element027  # link proxy (typed FeaturePython)
  Detach = false
  LinkTransform = true
  LinkedObject = -> Link [Link_i12.1.$mate.]
  _LinkVersion = 1
  _Parent = -> Elements
FEATURE [App::FeaturePython] Constraint016  label="Attachment014"  # WARN: FeaturePython — macro-defined, semantics opaque (R4)
  Cascade = false
  Disabled = false
  Group = -> [ElementLink030,ElementLink031]
  Multiply = false
  _ConstraintType = 45
  _LinkVersion = 1
  _Parent = -> Constraints
FEATURE [App::FeaturePython] ElementLink030  label="_Element028"  # link proxy (typed FeaturePython)
  LinkTransform = true
  LinkedObject = -> _Element028
  _LinkVersion = 1
  _Parent = -> Constraint016
FEATURE [Part::FeaturePython] _Element028  # link proxy (typed FeaturePython)
  Detach = false
  LinkTransform = true
  LinkedObject = -> Link001 [Hole.Edge135]
  _LinkVersion = 1
  _Parent = -> Elements
FEATURE [App::FeaturePython] ElementLink031  label="_Element029"  # link proxy (typed FeaturePython)
  LinkTransform = true
  LinkedObject = -> _Element029
  _LinkVersion = 1
  _Parent = -> Constraint016
FEATURE [Part::FeaturePython] _Element029  # link proxy (typed FeaturePython)
  Detach = false
  LinkTransform = true
  LinkedObject = -> Link [Link_i13.1.$mate.]
  _LinkVersion = 1
  _Parent = -> Elements
FEATURE [App::FeaturePython] Constraint017  label="Attachment015"  # WARN: FeaturePython — macro-defined, semantics opaque (R4)
  Cascade = false
  Disabled = false
  Group = -> [ElementLink032,ElementLink033]
  Multiply = false
  _ConstraintType = 45
  _LinkVersion = 1
  _Parent = -> Constraints
FEATURE [App::FeaturePython] ElementLink032  label="_Element030"  # link proxy (typed FeaturePython)
  LinkTransform = true
  LinkedObject = -> _Element030
  _LinkVersion = 1
  _Parent = -> Constraint017
FEATURE [Part::FeaturePython] _Element030  # link proxy (typed FeaturePython)
  Detach = false
  LinkTransform = true
  LinkedObject = -> Link001 [Hole.Edge137]
  _LinkVersion = 1
  _Parent = -> Elements
FEATURE [App::FeaturePython] ElementLink033  label="_Element031"  # link proxy (typed FeaturePython)
  LinkTransform = true
  LinkedObject = -> _Element031
  _LinkVersion = 1
  _Parent = -> Constraint017
FEATURE [Part::FeaturePython] _Element031  # link proxy (typed FeaturePython)
  Detach = false
  LinkTransform = true
  LinkedObject = -> Link [Link_i14.1.$mate.]
  _LinkVersion = 1
  _Parent = -> Elements
FEATURE [App::FeaturePython] Constraint018  label="Attachment016"  # WARN: FeaturePython — macro-defined, semantics opaque (R4)
  Cascade = false
  Disabled = false
  Group = -> [ElementLink034,ElementLink035]
  Multiply = false
  _ConstraintType = 45
  _LinkVersion = 1
  _Parent = -> Constraints
FEATURE [App::FeaturePython] ElementLink034  label="_Element032"  # link proxy (typed FeaturePython)
  LinkTransform = true
  LinkedObject = -> _Element032
  _LinkVersion = 1
  _Parent = -> Constraint018
FEATURE [Part::FeaturePython] _Element032  # link proxy (typed FeaturePython)
  Detach = false
  LinkTransform = true
  LinkedObject = -> Link001 [Hole.Edge145]
  _LinkVersion = 1
  _Parent = -> Elements
FEATURE [App::FeaturePython] ElementLink035  label="_Element033"  # link proxy (typed FeaturePython)
  LinkTransform = true
  LinkedObject = -> _Element033
  _LinkVersion = 1
  _Parent = -> Constraint018
FEATURE [Part::FeaturePython] _Element033  # link proxy (typed FeaturePython)
  Detach = false
  LinkTransform = true
  LinkedObject = -> Link [Link_i15.1.$mate.]
  _LinkVersion = 1
  _Parent = -> Elements
FEATURE [App::FeaturePython] Constraint019  label="Attachment017"  # WARN: FeaturePython — macro-defined, semantics opaque (R4)
  Cascade = false
  Disabled = false
  Group = -> [ElementLink036,ElementLink037]
  Multiply = false
  _ConstraintType = 45
  _LinkVersion = 1
  _Parent = -> Constraints
FEATURE [App::FeaturePython] ElementLink036  label="_Element034"  # link proxy (typed FeaturePython)
  LinkTransform = true
  LinkedObject = -> _Element034
  _LinkVersion = 1
  _Parent = -> Constraint019
FEATURE [Part::FeaturePython] _Element034  # link proxy (typed FeaturePython)
  Detach = false
  LinkTransform = true
  LinkedObject = -> Link001 [Hole.Edge147]
  _LinkVersion = 1
  _Parent = -> Elements
FEATURE [App::FeaturePython] ElementLink037  label="_Element035"  # link proxy (typed FeaturePython)
  LinkTransform = true
  LinkedObject = -> _Element035
  _LinkVersion = 1
  _Parent = -> Constraint019
FEATURE [Part::FeaturePython] _Element035  # link proxy (typed FeaturePython)
  Detach = false
  LinkTransform = true
  LinkedObject = -> Link [Link_i16.1.$mate.]
  _LinkVersion = 1
  _Parent = -> Elements
FEATURE [App::FeaturePython] Constraint020  label="Attachment018"  # WARN: FeaturePython — macro-defined, semantics opaque (R4)
  Cascade = false
  Disabled = false
  Group = -> [ElementLink038,ElementLink039]
  Multiply = false
  _ConstraintType = 45
  _LinkVersion = 1
  _Parent = -> Constraints
FEATURE [App::FeaturePython] ElementLink038  label="_Element036"  # link proxy (typed FeaturePython)
  LinkTransform = true
  LinkedObject = -> _Element036
  _LinkVersion = 1
  _Parent = -> Constraint020
FEATURE [Part::FeaturePython] _Element036  # link proxy (typed FeaturePython)
  Detach = false
  LinkTransform = true
  LinkedObject = -> Link001 [Hole.Edge149]
  _LinkVersion = 1
  _Parent = -> Elements
FEATURE [App::FeaturePython] ElementLink039  label="_Element037"  # link proxy (typed FeaturePython)
  LinkTransform = true
  LinkedObject = -> _Element037
  _LinkVersion = 1
  _Parent = -> Constraint020
FEATURE [Part::FeaturePython] _Element037  # link proxy (typed FeaturePython)
  Detach = false
  LinkTransform = true
  LinkedObject = -> Link [Link_i17.1.$mate.]
  _LinkVersion = 1
  _Parent = -> Elements
FEATURE [App::FeaturePython] Constraint021  label="Attachment019"  # WARN: FeaturePython — macro-defined, semantics opaque (R4)
  Cascade = false
  Disabled = false
  Group = -> [ElementLink040,ElementLink041]
  Multiply = false
  _ConstraintType = 45
  _LinkVersion = 1
  _Parent = -> Constraints
FEATURE [App::FeaturePython] ElementLink040  label="_Element038"  # link proxy (typed FeaturePython)
  LinkTransform = true
  LinkedObject = -> _Element038
  _LinkVersion = 1
  _Parent = -> Constraint021
FEATURE [Part::FeaturePython] _Element038  # link proxy (typed FeaturePython)
  Detach = false
  LinkTransform = true
  LinkedObject = -> Link001 [Hole.Edge139]
  _LinkVersion = 1
  _Parent = -> Elements
FEATURE [App::FeaturePython] ElementLink041  label="_Element039"  # link proxy (typed FeaturePython)
  LinkTransform = true
  LinkedObject = -> _Element039
  _LinkVersion = 1
  _Parent = -> Constraint021
FEATURE [Part::FeaturePython] _Element039  # link proxy (typed FeaturePython)
  Detach = false
  LinkTransform = true
  LinkedObject = -> Link [Link_i18.1.$mate.]
  _LinkVersion = 1
  _Parent = -> Elements
FEATURE [App::FeaturePython] Constraint022  label="Attachment020"  # WARN: FeaturePython — macro-defined, semantics opaque (R4)
  Cascade = false
  Disabled = false
  Group = -> [ElementLink042,ElementLink043]
  Multiply = false
  _ConstraintType = 45
  _LinkVersion = 1
  _Parent = -> Constraints
FEATURE [App::FeaturePython] ElementLink042  label="_Element040"  # link proxy (typed FeaturePython)
  LinkTransform = true
  LinkedObject = -> _Element040
  _LinkVersion = 1
  _Parent = -> Constraint022
FEATURE [Part::FeaturePython] _Element040  # link proxy (typed FeaturePython)
  Detach = false
  LinkTransform = true
  LinkedObject = -> Link001 [Hole.Edge141]
  _LinkVersion = 1
  _Parent = -> Elements
FEATURE [App::FeaturePython] ElementLink043  label="_Element041"  # link proxy (typed FeaturePython)
  LinkTransform = true
  LinkedObject = -> _Element041
  _LinkVersion = 1
  _Parent = -> Constraint022
FEATURE [Part::FeaturePython] _Element041  # link proxy (typed FeaturePython)
  Detach = false
  LinkTransform = true
  LinkedObject = -> Link [Link_i19.1.$mate.]
  _LinkVersion = 1
  _Parent = -> Elements
FEATURE [App::FeaturePython] Constraint023  label="Attachment021"  # WARN: FeaturePython — macro-defined, semantics opaque (R4)
  Cascade = false
  Disabled = false
  Group = -> [ElementLink044,ElementLink045]
  Multiply = false
  _ConstraintType = 45
  _LinkVersion = 1
  _Parent = -> Constraints
FEATURE [App::FeaturePython] ElementLink044  label="_Element042"  # link proxy (typed FeaturePython)
  LinkTransform = true
  LinkedObject = -> _Element042
  _LinkVersion = 1
  _Parent = -> Constraint023
FEATURE [Part::FeaturePython] _Element042  # link proxy (typed FeaturePython)
  Detach = false
  LinkTransform = true
  LinkedObject = -> Link001 [Hole.Edge143]
  _LinkVersion = 1
  _Parent = -> Elements
FEATURE [App::FeaturePython] ElementLink045  label="_Element043"  # link proxy (typed FeaturePython)
  LinkTransform = true
  LinkedObject = -> _Element043
  _LinkVersion = 1
  _Parent = -> Constraint023
FEATURE [Part::FeaturePython] _Element043  # link proxy (typed FeaturePython)
  Detach = false
  LinkTransform = true
  LinkedObject = -> Link [Link_i20.1.$mate.]
  _LinkVersion = 1
  _Parent = -> Elements
FEATURE [App::FeaturePython] Constraint024  label="Attachment022"  # WARN: FeaturePython — macro-defined, semantics opaque (R4)
  Cascade = false
  Disabled = false
  Group = -> [ElementLink046,ElementLink047]
  Multiply = false
  _ConstraintType = 45
  _LinkVersion = 1
  _Parent = -> Constraints
FEATURE [App::FeaturePython] ElementLink046  label="_Element044"  # link proxy (typed FeaturePython)
  LinkTransform = true
  LinkedObject = -> _Element044
  _LinkVersion = 1
  _Parent = -> Constraint024
FEATURE [Part::FeaturePython] _Element044  # link proxy (typed FeaturePython)
  Detach = false
  LinkTransform = true
  LinkedObject = -> Link001 [Hole.Edge151]
  _LinkVersion = 1
  _Parent = -> Elements
FEATURE [App::FeaturePython] ElementLink047  label="_Element045"  # link proxy (typed FeaturePython)
  LinkTransform = true
  LinkedObject = -> _Element045
  _LinkVersion = 1
  _Parent = -> Constraint024
FEATURE [Part::FeaturePython] _Element045  # link proxy (typed FeaturePython)
  Detach = false
  LinkTransform = true
  LinkedObject = -> Link [Link_i21.1.$mate.]
  _LinkVersion = 1
  _Parent = -> Elements
FEATURE [App::FeaturePython] Constraint025  label="Attachment023"  # WARN: FeaturePython — macro-defined, semantics opaque (R4)
  Cascade = false
  Disabled = false
  Group = -> [ElementLink048,ElementLink049]
  Multiply = false
  _ConstraintType = 45
  _LinkVersion = 1
  _Parent = -> Constraints
FEATURE [App::FeaturePython] ElementLink048  label="_Element046"  # link proxy (typed FeaturePython)
  LinkTransform = true
  LinkedObject = -> _Element046
  _LinkVersion = 1
  _Parent = -> Constraint025
FEATURE [Part::FeaturePython] _Element046  # link proxy (typed FeaturePython)
  Detach = false
  LinkTransform = true
  LinkedObject = -> Link001 [Hole.Edge153]
  _LinkVersion = 1
  _Parent = -> Elements
FEATURE [App::FeaturePython] ElementLink049  label="_Element047"  # link proxy (typed FeaturePython)
  LinkTransform = true
  LinkedObject = -> _Element047
  _LinkVersion = 1
  _Parent = -> Constraint025
FEATURE [Part::FeaturePython] _Element047  # link proxy (typed FeaturePython)
  Detach = false
  LinkTransform = true
  LinkedObject = -> Link [Link_i22.1.$mate.]
  _LinkVersion = 1
  _Parent = -> Elements
FEATURE [App::FeaturePython] Constraint026  label="Attachment024"  # WARN: FeaturePython — macro-defined, semantics opaque (R4)
  Cascade = false
  Disabled = false
  Group = -> [ElementLink050,ElementLink051]
  Multiply = false
  _ConstraintType = 45
  _LinkVersion = 1
  _Parent = -> Constraints
FEATURE [App::FeaturePython] ElementLink050  label="_Element048"  # link proxy (typed FeaturePython)
  LinkTransform = true
  LinkedObject = -> _Element048
  _LinkVersion = 1
  _Parent = -> Constraint026
FEATURE [Part::FeaturePython] _Element048  # link proxy (typed FeaturePython)
  Detach = false
  LinkTransform = true
  LinkedObject = -> Link001 [Hole.Edge155]
  _LinkVersion = 1
  _Parent = -> Elements
FEATURE [App::FeaturePython] ElementLink051  label="_Element049"  # link proxy (typed FeaturePython)
  LinkTransform = true
  LinkedObject = -> _Element049
  _LinkVersion = 1
  _Parent = -> Constraint026
FEATURE [Part::FeaturePython] _Element049  # link proxy (typed FeaturePython)
  Detach = false
  LinkTransform = true
  LinkedObject = -> Link [Link_i23.1.$mate.]
  _LinkVersion = 1
  _Parent = -> Elements
